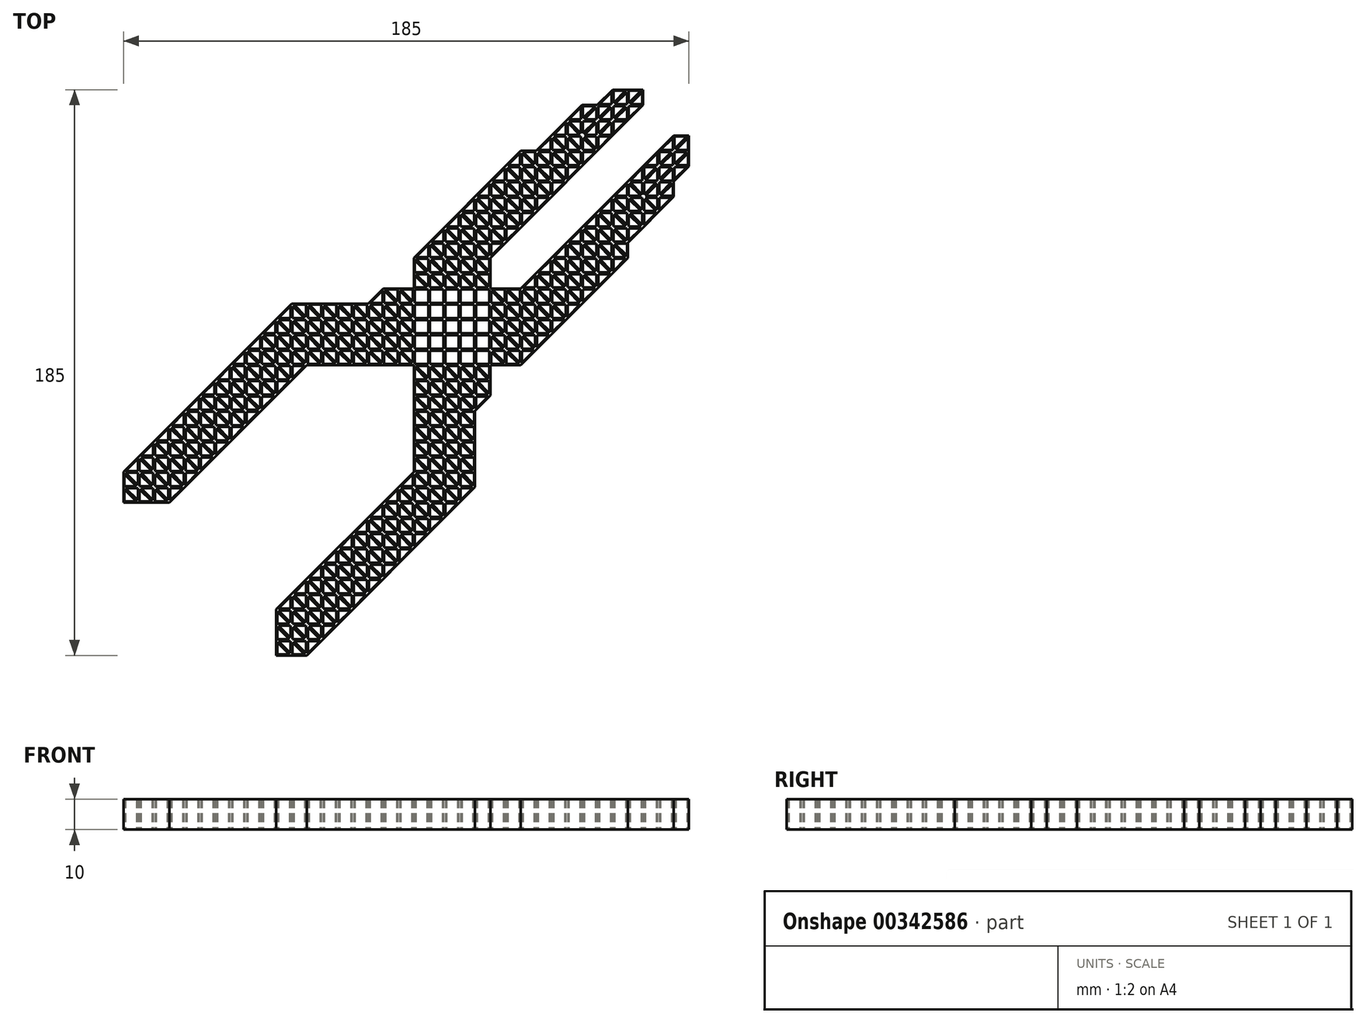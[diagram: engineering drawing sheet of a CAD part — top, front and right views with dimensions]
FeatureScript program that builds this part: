
annotation { "Feature Type Name" : "Feature", "Feature Type Description" : "" }
export const myFeature = defineFeature(function(context is Context, id is Id, definition is map)
    precondition{}
    {
        {
            var Q0;
            Q0=qCreatedBy(makeId("Top.planeOp"),FACE);
            var sketch = newSketch(context, id + "F0", { "sketchPlane" : qUnion([Q0])});
            skLineSegment(sketch, "E0", {"start": v(-41.78, -87.8) * mm, "end": v(-37.8, -87.8) * mm});
            skLineSegment(sketch, "E1", {"start": v(-37.8, -87.8) * mm, "end": v(-37.8, -91.78) * mm});
            skLineSegment(sketch, "E2", {"start": v(-37.8, -91.78) * mm, "end": v(-41.78, -87.8) * mm});
            skLineSegment(sketch, "E3", {"start": v(-86.78, -37.8) * mm, "end": v(-82.8, -37.8) * mm});
            skLineSegment(sketch, "E4", {"start": v(-82.8, -37.8) * mm, "end": v(-82.8, -41.78) * mm});
            skLineSegment(sketch, "E5", {"start": v(-82.8, -41.78) * mm, "end": v(-86.78, -37.8) * mm});
            skLineSegment(sketch, "E6", {"start": v(-91.78, -37.8) * mm, "end": v(-87.8, -37.8) * mm});
            skLineSegment(sketch, "E7", {"start": v(-87.8, -37.8) * mm, "end": v(-87.8, -41.78) * mm});
            skLineSegment(sketch, "E8", {"start": v(-87.8, -41.78) * mm, "end": v(-91.78, -37.8) * mm});
            skLineSegment(sketch, "E9", {"start": v(-33.22, 17.8) * mm, "end": v(-37.2, 17.8) * mm});
            skLineSegment(sketch, "E10", {"start": v(-37.2, 17.8) * mm, "end": v(-37.2, 21.78) * mm});
            skLineSegment(sketch, "E11", {"start": v(-37.2, 21.78) * mm, "end": v(-33.22, 17.8) * mm});
            skLineSegment(sketch, "E12", {"start": v(-18.22, 17.8) * mm, "end": v(-22.2, 17.8) * mm});
            skLineSegment(sketch, "E13", {"start": v(-22.2, 17.8) * mm, "end": v(-22.2, 21.78) * mm});
            skLineSegment(sketch, "E14", {"start": v(-22.2, 21.78) * mm, "end": v(-18.22, 17.8) * mm});
            skLineSegment(sketch, "E15", {"start": v(-3.22, 22.8) * mm, "end": v(-7.2, 22.8) * mm});
            skLineSegment(sketch, "E16", {"start": v(-7.2, 22.8) * mm, "end": v(-7.2, 26.78) * mm});
            skLineSegment(sketch, "E17", {"start": v(-7.2, 26.78) * mm, "end": v(-3.22, 22.8) * mm});
            skLineSegment(sketch, "E18", {"start": v(41.78, 67.8) * mm, "end": v(37.8, 67.8) * mm});
            skLineSegment(sketch, "E19", {"start": v(37.8, 67.8) * mm, "end": v(37.8, 71.78) * mm});
            skLineSegment(sketch, "E20", {"start": v(37.8, 71.78) * mm, "end": v(41.78, 67.8) * mm});
            skLineSegment(sketch, "E21", {"start": v(77.2, 87.8) * mm, "end": v(73.22, 87.8) * mm});
            skLineSegment(sketch, "E22", {"start": v(73.22, 87.8) * mm, "end": v(77.2, 91.78) * mm});
            skLineSegment(sketch, "E23", {"start": v(77.2, 91.78) * mm, "end": v(77.2, 87.8) * mm});
            skLineSegment(sketch, "E24", {"start": v(68.22, 82.8) * mm, "end": v(72.2, 86.78) * mm});
            skLineSegment(sketch, "E25", {"start": v(72.2, 86.78) * mm, "end": v(72.2, 82.8) * mm});
            skLineSegment(sketch, "E26", {"start": v(72.2, 82.8) * mm, "end": v(68.22, 82.8) * mm});
            skLineSegment(sketch, "E27", {"start": v(36.78, 22.8) * mm, "end": v(32.8, 22.8) * mm});
            skLineSegment(sketch, "E28", {"start": v(32.8, 22.8) * mm, "end": v(32.8, 26.78) * mm});
            skLineSegment(sketch, "E29", {"start": v(32.8, 26.78) * mm, "end": v(36.78, 22.8) * mm});
            skLineSegment(sketch, "E30", {"start": v(67.2, 33.22) * mm, "end": v(63.22, 37.2) * mm});
            skLineSegment(sketch, "E31", {"start": v(63.22, 37.2) * mm, "end": v(67.2, 37.2) * mm});
            skLineSegment(sketch, "E32", {"start": v(67.2, 37.2) * mm, "end": v(67.2, 33.22) * mm});
            skLineSegment(sketch, "E33", {"start": v(57.2, 23.22) * mm, "end": v(53.22, 27.2) * mm});
            skLineSegment(sketch, "E34", {"start": v(53.22, 27.2) * mm, "end": v(57.2, 27.2) * mm});
            skLineSegment(sketch, "E35", {"start": v(57.2, 27.2) * mm, "end": v(57.2, 23.22) * mm});
            skLineSegment(sketch, "E36", {"start": v(52.2, 18.22) * mm, "end": v(48.22, 22.2) * mm});
            skLineSegment(sketch, "E37", {"start": v(48.22, 22.2) * mm, "end": v(52.2, 22.2) * mm});
            skLineSegment(sketch, "E38", {"start": v(52.2, 22.2) * mm, "end": v(52.2, 18.22) * mm});
            skLineSegment(sketch, "E39", {"start": v(47.2, 13.22) * mm, "end": v(43.22, 17.2) * mm});
            skLineSegment(sketch, "E40", {"start": v(43.22, 17.2) * mm, "end": v(47.2, 17.2) * mm});
            skLineSegment(sketch, "E41", {"start": v(47.2, 17.2) * mm, "end": v(47.2, 13.22) * mm});
            skLineSegment(sketch, "E42", {"start": v(38.22, 12.2) * mm, "end": v(42.2, 12.2) * mm});
            skLineSegment(sketch, "E43", {"start": v(42.2, 12.2) * mm, "end": v(42.2, 8.22) * mm});
            skLineSegment(sketch, "E44", {"start": v(42.2, 8.22) * mm, "end": v(38.22, 12.2) * mm});
            skLineSegment(sketch, "E45", {"start": v(28.22, 7.2) * mm, "end": v(32.2, 7.2) * mm});
            skLineSegment(sketch, "E46", {"start": v(32.2, 7.2) * mm, "end": v(32.2, 5) * mm});
            skLineSegment(sketch, "E47", {"start": v(32.2, 5) * mm, "end": v(32.2, 3.22) * mm});
            skLineSegment(sketch, "E48", {"start": v(32.2, 3.22) * mm, "end": v(28.22, 7.2) * mm});
            skLineSegment(sketch, "E49", {"start": v(18.22, -32.8) * mm, "end": v(22.2, -32.8) * mm});
            skLineSegment(sketch, "E50", {"start": v(22.2, -32.8) * mm, "end": v(22.2, -36.78) * mm});
            skLineSegment(sketch, "E51", {"start": v(22.2, -36.78) * mm, "end": v(18.22, -32.8) * mm});
            skLineSegment(sketch, "E52", {"start": v(12.2, -46.78) * mm, "end": v(8.22, -42.8) * mm});
            skLineSegment(sketch, "E53", {"start": v(8.22, -42.8) * mm, "end": v(12.2, -42.8) * mm});
            skLineSegment(sketch, "E54", {"start": v(12.2, -42.8) * mm, "end": v(12.2, -46.78) * mm});
            skLineSegment(sketch, "E55", {"start": v(-7.8, -66.78) * mm, "end": v(-11.78, -62.8) * mm});
            skLineSegment(sketch, "E56", {"start": v(-11.78, -62.8) * mm, "end": v(-7.8, -62.8) * mm});
            skLineSegment(sketch, "E57", {"start": v(-7.8, -62.8) * mm, "end": v(-7.8, -66.78) * mm});
            skLineSegment(sketch, "E58", {"start": v(-21.78, -72.8) * mm, "end": v(-20, -72.8) * mm});
            skLineSegment(sketch, "E59", {"start": v(-20, -72.8) * mm, "end": v(-17.8, -72.8) * mm});
            skLineSegment(sketch, "E60", {"start": v(-17.8, -72.8) * mm, "end": v(-17.8, -76.78) * mm});
            skLineSegment(sketch, "E61", {"start": v(-17.8, -76.78) * mm, "end": v(-21.78, -72.8) * mm});
            skLineSegment(sketch, "E62", {"start": v(-27.8, -86.78) * mm, "end": v(-31.78, -82.8) * mm});
            skLineSegment(sketch, "E63", {"start": v(-31.78, -82.8) * mm, "end": v(-27.8, -82.8) * mm});
            skLineSegment(sketch, "E64", {"start": v(-27.8, -82.8) * mm, "end": v(-27.8, -86.78) * mm});
            skLineSegment(sketch, "E65", {"start": v(-32.8, 3.22) * mm, "end": v(-36.78, 7.2) * mm});
            skLineSegment(sketch, "E66", {"start": v(-36.78, 7.2) * mm, "end": v(-32.8, 7.2) * mm});
            skLineSegment(sketch, "E67", {"start": v(-32.8, 7.2) * mm, "end": v(-32.8, 3.22) * mm});
            skLineSegment(sketch, "E68", {"start": v(-47.8, -11.78) * mm, "end": v(-51.78, -7.8) * mm});
            skLineSegment(sketch, "E69", {"start": v(-51.78, -7.8) * mm, "end": v(-47.8, -7.8) * mm});
            skLineSegment(sketch, "E70", {"start": v(-47.8, -7.8) * mm, "end": v(-47.8, -11.78) * mm});
            skLineSegment(sketch, "E71", {"start": v(-92.2, -33.22) * mm, "end": v(-88.22, -37.2) * mm});
            skLineSegment(sketch, "E72", {"start": v(-88.22, -37.2) * mm, "end": v(-92.2, -37.2) * mm});
            skLineSegment(sketch, "E73", {"start": v(-92.2, -37.2) * mm, "end": v(-92.2, -33.22) * mm});
            skLineSegment(sketch, "E74", {"start": v(-83.22, -32.2) * mm, "end": v(-87.2, -32.2) * mm});
            skLineSegment(sketch, "E75", {"start": v(-87.2, -32.2) * mm, "end": v(-87.2, -28.22) * mm});
            skLineSegment(sketch, "E76", {"start": v(-87.2, -28.22) * mm, "end": v(-83.22, -32.2) * mm});
            skLineSegment(sketch, "E77", {"start": v(-77.2, -18.22) * mm, "end": v(-73.22, -22.2) * mm});
            skLineSegment(sketch, "E78", {"start": v(-73.22, -22.2) * mm, "end": v(-77.2, -22.2) * mm});
            skLineSegment(sketch, "E79", {"start": v(-77.2, -22.2) * mm, "end": v(-77.2, -18.22) * mm});
            skLineSegment(sketch, "E80", {"start": v(-63.22, -12.2) * mm, "end": v(-67.2, -12.2) * mm});
            skLineSegment(sketch, "E81", {"start": v(-67.2, -12.2) * mm, "end": v(-67.2, -8.22) * mm});
            skLineSegment(sketch, "E82", {"start": v(-67.2, -8.22) * mm, "end": v(-63.22, -12.2) * mm});
            skLineSegment(sketch, "E83", {"start": v(-43.22, 7.8) * mm, "end": v(-47.2, 7.8) * mm});
            skLineSegment(sketch, "E84", {"start": v(-47.2, 7.8) * mm, "end": v(-47.2, 11.78) * mm});
            skLineSegment(sketch, "E85", {"start": v(-47.2, 11.78) * mm, "end": v(-43.22, 7.8) * mm});
            skLineSegment(sketch, "E86", {"start": v(-38.22, 12.8) * mm, "end": v(-42.2, 12.8) * mm});
            skLineSegment(sketch, "E87", {"start": v(-42.2, 12.8) * mm, "end": v(-42.2, 16.78) * mm});
            skLineSegment(sketch, "E88", {"start": v(-42.2, 16.78) * mm, "end": v(-38.22, 12.8) * mm});
            skLineSegment(sketch, "E89", {"start": v(6.78, 32.8) * mm, "end": v(5, 32.8) * mm});
            skLineSegment(sketch, "E90", {"start": v(5, 32.8) * mm, "end": v(2.8, 32.8) * mm});
            skLineSegment(sketch, "E91", {"start": v(2.8, 32.8) * mm, "end": v(2.8, 36.78) * mm});
            skLineSegment(sketch, "E92", {"start": v(2.8, 36.78) * mm, "end": v(6.78, 32.8) * mm});
            skLineSegment(sketch, "E93", {"start": v(11.78, 37.8) * mm, "end": v(7.8, 37.8) * mm});
            skLineSegment(sketch, "E94", {"start": v(7.8, 37.8) * mm, "end": v(7.8, 41.78) * mm});
            skLineSegment(sketch, "E95", {"start": v(7.8, 41.78) * mm, "end": v(11.78, 37.8) * mm});
            skLineSegment(sketch, "E96", {"start": v(16.78, 42.8) * mm, "end": v(12.8, 42.8) * mm});
            skLineSegment(sketch, "E97", {"start": v(12.8, 42.8) * mm, "end": v(12.8, 46.78) * mm});
            skLineSegment(sketch, "E98", {"start": v(12.8, 46.78) * mm, "end": v(16.78, 42.8) * mm});
            skLineSegment(sketch, "E99", {"start": v(21.78, 47.8) * mm, "end": v(17.8, 47.8) * mm});
            skLineSegment(sketch, "E100", {"start": v(17.8, 47.8) * mm, "end": v(17.8, 51.78) * mm});
            skLineSegment(sketch, "E101", {"start": v(17.8, 51.78) * mm, "end": v(21.78, 47.8) * mm});
            skLineSegment(sketch, "E102", {"start": v(31.78, 57.8) * mm, "end": v(27.8, 57.8) * mm});
            skLineSegment(sketch, "E103", {"start": v(27.8, 57.8) * mm, "end": v(27.8, 61.78) * mm});
            skLineSegment(sketch, "E104", {"start": v(27.8, 61.78) * mm, "end": v(31.78, 57.8) * mm});
            skLineSegment(sketch, "E105", {"start": v(56.78, 77.8) * mm, "end": v(52.8, 77.8) * mm});
            skLineSegment(sketch, "E106", {"start": v(52.8, 77.8) * mm, "end": v(52.8, 81.78) * mm});
            skLineSegment(sketch, "E107", {"start": v(52.8, 81.78) * mm, "end": v(56.78, 77.8) * mm});
            skLineSegment(sketch, "E108", {"start": v(62.2, 73.22) * mm, "end": v(58.22, 77.2) * mm});
            skLineSegment(sketch, "E109", {"start": v(58.22, 77.2) * mm, "end": v(62.2, 77.2) * mm});
            skLineSegment(sketch, "E110", {"start": v(62.2, 77.2) * mm, "end": v(62.2, 73.22) * mm});
            skLineSegment(sketch, "E111", {"start": v(52.2, 63.22) * mm, "end": v(48.22, 67.2) * mm});
            skLineSegment(sketch, "E112", {"start": v(48.22, 67.2) * mm, "end": v(52.2, 67.2) * mm});
            skLineSegment(sketch, "E113", {"start": v(52.2, 67.2) * mm, "end": v(52.2, 63.22) * mm});
            skLineSegment(sketch, "E114", {"start": v(43.22, 62.2) * mm, "end": v(47.2, 62.2) * mm});
            skLineSegment(sketch, "E115", {"start": v(47.2, 62.2) * mm, "end": v(47.2, 58.22) * mm});
            skLineSegment(sketch, "E116", {"start": v(47.2, 58.22) * mm, "end": v(43.22, 62.2) * mm});
            skLineSegment(sketch, "E117", {"start": v(42.2, 53.22) * mm, "end": v(38.22, 57.2) * mm});
            skLineSegment(sketch, "E118", {"start": v(38.22, 57.2) * mm, "end": v(42.2, 57.2) * mm});
            skLineSegment(sketch, "E119", {"start": v(42.2, 57.2) * mm, "end": v(42.2, 53.22) * mm});
            skLineSegment(sketch, "E120", {"start": v(32.2, 43.22) * mm, "end": v(28.22, 47.2) * mm});
            skLineSegment(sketch, "E121", {"start": v(28.22, 47.2) * mm, "end": v(32.2, 47.2) * mm});
            skLineSegment(sketch, "E122", {"start": v(32.2, 47.2) * mm, "end": v(32.2, 43.22) * mm});
            skLineSegment(sketch, "E123", {"start": v(46.78, 27.8) * mm, "end": v(42.8, 27.8) * mm});
            skLineSegment(sketch, "E124", {"start": v(42.8, 27.8) * mm, "end": v(42.8, 31.78) * mm});
            skLineSegment(sketch, "E125", {"start": v(42.8, 31.78) * mm, "end": v(46.78, 27.8) * mm});
            skLineSegment(sketch, "E126", {"start": v(56.78, 37.8) * mm, "end": v(52.8, 37.8) * mm});
            skLineSegment(sketch, "E127", {"start": v(52.8, 37.8) * mm, "end": v(52.8, 41.78) * mm});
            skLineSegment(sketch, "E128", {"start": v(52.8, 41.78) * mm, "end": v(56.78, 37.8) * mm});
            skLineSegment(sketch, "E129", {"start": v(61.78, 42.8) * mm, "end": v(57.8, 42.8) * mm});
            skLineSegment(sketch, "E130", {"start": v(57.8, 42.8) * mm, "end": v(57.8, 46.78) * mm});
            skLineSegment(sketch, "E131", {"start": v(57.8, 46.78) * mm, "end": v(61.78, 42.8) * mm});
            skLineSegment(sketch, "E132", {"start": v(62.8, 51.78) * mm, "end": v(66.78, 47.8) * mm});
            skLineSegment(sketch, "E133", {"start": v(66.78, 47.8) * mm, "end": v(62.8, 47.8) * mm});
            skLineSegment(sketch, "E134", {"start": v(62.8, 47.8) * mm, "end": v(62.8, 51.78) * mm});
            skLineSegment(sketch, "E135", {"start": v(76.78, 57.8) * mm, "end": v(72.8, 57.8) * mm});
            skLineSegment(sketch, "E136", {"start": v(72.8, 57.8) * mm, "end": v(72.8, 61.78) * mm});
            skLineSegment(sketch, "E137", {"start": v(72.8, 61.78) * mm, "end": v(76.78, 57.8) * mm});
            skLineSegment(sketch, "E138", {"start": v(5, -22.8) * mm, "end": v(7.2, -22.8) * mm});
            skLineSegment(sketch, "E139", {"start": v(7.2, -22.8) * mm, "end": v(7.2, -26.78) * mm});
            skLineSegment(sketch, "E140", {"start": v(7.2, -26.78) * mm, "end": v(3.22, -22.8) * mm});
            skLineSegment(sketch, "E141", {"start": v(3.22, -22.8) * mm, "end": v(5, -22.8) * mm});
            skLineSegment(sketch, "E142", {"start": v(5, -7.8) * mm, "end": v(7.2, -7.8) * mm});
            skLineSegment(sketch, "E143", {"start": v(7.2, -7.8) * mm, "end": v(7.2, -11.78) * mm});
            skLineSegment(sketch, "E144", {"start": v(7.2, -11.78) * mm, "end": v(3.22, -7.8) * mm});
            skLineSegment(sketch, "E145", {"start": v(3.22, -7.8) * mm, "end": v(5, -7.8) * mm});
            skLineSegment(sketch, "E146", {"start": v(-2.8, 8.22) * mm, "end": v(-6.78, 12.2) * mm});
            skLineSegment(sketch, "E147", {"start": v(-6.78, 12.2) * mm, "end": v(-2.8, 12.2) * mm});
            skLineSegment(sketch, "E148", {"start": v(-2.8, 12.2) * mm, "end": v(-2.8, 8.22) * mm});
            skLineSegment(sketch, "E149", {"start": v(-17.8, 8.22) * mm, "end": v(-21.78, 12.2) * mm});
            skLineSegment(sketch, "E150", {"start": v(-21.78, 12.2) * mm, "end": v(-17.8, 12.2) * mm});
            skLineSegment(sketch, "E151", {"start": v(-17.8, 12.2) * mm, "end": v(-17.8, 8.22) * mm});
            skLineSegment(sketch, "E152", {"start": v(-77.8, -36.78) * mm, "end": v(-81.78, -32.8) * mm});
            skLineSegment(sketch, "E153", {"start": v(-81.78, -32.8) * mm, "end": v(-77.8, -32.8) * mm});
            skLineSegment(sketch, "E154", {"start": v(-77.8, -32.8) * mm, "end": v(-77.8, -36.78) * mm});
            skLineSegment(sketch, "E155", {"start": v(-86.78, -32.8) * mm, "end": v(-82.8, -32.8) * mm});
            skLineSegment(sketch, "E156", {"start": v(-82.8, -32.8) * mm, "end": v(-82.8, -36.78) * mm});
            skLineSegment(sketch, "E157", {"start": v(-82.8, -36.78) * mm, "end": v(-86.78, -32.8) * mm});
            skLineSegment(sketch, "E158", {"start": v(-82.2, -28.22) * mm, "end": v(-78.22, -32.2) * mm});
            skLineSegment(sketch, "E159", {"start": v(-78.22, -32.2) * mm, "end": v(-82.2, -32.2) * mm});
            skLineSegment(sketch, "E160", {"start": v(-82.2, -32.2) * mm, "end": v(-82.2, -28.22) * mm});
            skLineSegment(sketch, "E161", {"start": v(-62.8, -16.78) * mm, "end": v(-66.78, -12.8) * mm});
            skLineSegment(sketch, "E162", {"start": v(-66.78, -12.8) * mm, "end": v(-62.8, -12.8) * mm});
            skLineSegment(sketch, "E163", {"start": v(-62.8, -12.8) * mm, "end": v(-62.8, -16.78) * mm});
            skLineSegment(sketch, "E164", {"start": v(-63.22, -17.2) * mm, "end": v(-65, -17.2) * mm});
            skLineSegment(sketch, "E165", {"start": v(-65, -17.2) * mm, "end": v(-67.2, -17.2) * mm});
            skLineSegment(sketch, "E166", {"start": v(-67.2, -17.2) * mm, "end": v(-67.2, -13.22) * mm});
            skLineSegment(sketch, "E167", {"start": v(-67.2, -13.22) * mm, "end": v(-63.22, -17.2) * mm});
            skLineSegment(sketch, "E168", {"start": v(-77.8, -31.78) * mm, "end": v(-81.78, -27.8) * mm});
            skLineSegment(sketch, "E169", {"start": v(-81.78, -27.8) * mm, "end": v(-77.8, -27.8) * mm});
            skLineSegment(sketch, "E170", {"start": v(-77.8, -27.8) * mm, "end": v(-77.8, -31.78) * mm});
            skLineSegment(sketch, "E171", {"start": v(-77.2, -32.2) * mm, "end": v(-77.2, -28.22) * mm});
            skLineSegment(sketch, "E172", {"start": v(-77.2, -28.22) * mm, "end": v(-73.23, -32.2) * mm});
            skLineSegment(sketch, "E173", {"start": v(-73.23, -32.2) * mm, "end": v(-77.2, -32.2) * mm});
            skLineSegment(sketch, "E174", {"start": v(-77.2, -23.22) * mm, "end": v(-73.22, -27.2) * mm});
            skLineSegment(sketch, "E175", {"start": v(-73.22, -27.2) * mm, "end": v(-77.2, -27.2) * mm});
            skLineSegment(sketch, "E176", {"start": v(-77.2, -27.2) * mm, "end": v(-77.2, -23.22) * mm});
            skLineSegment(sketch, "E177", {"start": v(-76.78, -22.8) * mm, "end": v(-72.8, -22.8) * mm});
            skLineSegment(sketch, "E178", {"start": v(-72.8, -22.8) * mm, "end": v(-72.8, -26.78) * mm});
            skLineSegment(sketch, "E179", {"start": v(-72.8, -26.78) * mm, "end": v(-76.78, -22.8) * mm});
            skLineSegment(sketch, "E180", {"start": v(-67.2, -22.2) * mm, "end": v(-67.2, -18.22) * mm});
            skLineSegment(sketch, "E181", {"start": v(-67.2, -18.22) * mm, "end": v(-63.22, -22.2) * mm});
            skLineSegment(sketch, "E182", {"start": v(-63.22, -22.2) * mm, "end": v(-67.2, -22.2) * mm});
            skLineSegment(sketch, "E183", {"start": v(-67.8, -16.78) * mm, "end": v(-71.78, -12.8) * mm});
            skLineSegment(sketch, "E184", {"start": v(-71.78, -12.8) * mm, "end": v(-67.8, -12.8) * mm});
            skLineSegment(sketch, "E185", {"start": v(-67.8, -12.8) * mm, "end": v(-67.8, -16.78) * mm});
            skLineSegment(sketch, "E186", {"start": v(-67.8, -17.8) * mm, "end": v(-67.8, -21.78) * mm});
            skLineSegment(sketch, "E187", {"start": v(-67.8, -21.78) * mm, "end": v(-71.78, -17.8) * mm});
            skLineSegment(sketch, "E188", {"start": v(-71.78, -17.8) * mm, "end": v(-67.8, -17.8) * mm});
            skLineSegment(sketch, "E189", {"start": v(-77.8, -26.78) * mm, "end": v(-81.78, -22.8) * mm});
            skLineSegment(sketch, "E190", {"start": v(-81.78, -22.8) * mm, "end": v(-77.8, -22.8) * mm});
            skLineSegment(sketch, "E191", {"start": v(-77.8, -22.8) * mm, "end": v(-77.8, -26.78) * mm});
            skLineSegment(sketch, "E192", {"start": v(-78.22, -27.2) * mm, "end": v(-82.2, -27.2) * mm});
            skLineSegment(sketch, "E193", {"start": v(-82.2, -27.2) * mm, "end": v(-82.2, -23.22) * mm});
            skLineSegment(sketch, "E194", {"start": v(-82.2, -23.22) * mm, "end": v(-78.22, -27.2) * mm});
            skLineSegment(sketch, "E195", {"start": v(-87.8, -36.78) * mm, "end": v(-91.78, -32.8) * mm});
            skLineSegment(sketch, "E196", {"start": v(-91.78, -32.8) * mm, "end": v(-87.8, -32.8) * mm});
            skLineSegment(sketch, "E197", {"start": v(-87.8, -32.8) * mm, "end": v(-87.8, -36.78) * mm});
            skLineSegment(sketch, "E198", {"start": v(-72.8, -31.78) * mm, "end": v(-76.78, -27.8) * mm});
            skLineSegment(sketch, "E199", {"start": v(-76.78, -27.8) * mm, "end": v(-72.8, -27.8) * mm});
            skLineSegment(sketch, "E200", {"start": v(-72.8, -27.8) * mm, "end": v(-72.8, -31.78) * mm});
            skLineSegment(sketch, "E201", {"start": v(-72.2, -23.22) * mm, "end": v(-68.22, -27.2) * mm});
            skLineSegment(sketch, "E202", {"start": v(-68.22, -27.2) * mm, "end": v(-72.2, -27.2) * mm});
            skLineSegment(sketch, "E203", {"start": v(-72.2, -27.2) * mm, "end": v(-72.2, -23.22) * mm});
            skLineSegment(sketch, "E204", {"start": v(-71.78, -22.8) * mm, "end": v(-67.8, -22.8) * mm});
            skLineSegment(sketch, "E205", {"start": v(-67.8, -22.8) * mm, "end": v(-67.8, -26.78) * mm});
            skLineSegment(sketch, "E206", {"start": v(-67.8, -26.78) * mm, "end": v(-71.78, -22.8) * mm});
            skLineSegment(sketch, "E207", {"start": v(-62.8, -22.8) * mm, "end": v(-62.8, -26.78) * mm});
            skLineSegment(sketch, "E208", {"start": v(-62.8, -26.78) * mm, "end": v(-66.78, -22.8) * mm});
            skLineSegment(sketch, "E209", {"start": v(-66.78, -22.8) * mm, "end": v(-62.8, -22.8) * mm});
            skLineSegment(sketch, "E210", {"start": v(-62.8, -21.78) * mm, "end": v(-66.78, -17.8) * mm});
            skLineSegment(sketch, "E211", {"start": v(-66.78, -17.8) * mm, "end": v(-65, -17.8) * mm});
            skLineSegment(sketch, "E212", {"start": v(-65, -17.8) * mm, "end": v(-62.8, -17.8) * mm});
            skLineSegment(sketch, "E213", {"start": v(-62.8, -17.8) * mm, "end": v(-62.8, -21.78) * mm});
            skLineSegment(sketch, "E214", {"start": v(-62.2, -13.22) * mm, "end": v(-58.22, -17.2) * mm});
            skLineSegment(sketch, "E215", {"start": v(-58.22, -17.2) * mm, "end": v(-62.2, -17.2) * mm});
            skLineSegment(sketch, "E216", {"start": v(-62.2, -17.2) * mm, "end": v(-62.2, -13.22) * mm});
            skLineSegment(sketch, "E217", {"start": v(-62.2, -8.22) * mm, "end": v(-58.22, -12.2) * mm});
            skLineSegment(sketch, "E218", {"start": v(-58.22, -12.2) * mm, "end": v(-62.2, -12.2) * mm});
            skLineSegment(sketch, "E219", {"start": v(-62.2, -12.2) * mm, "end": v(-62.2, -8.22) * mm});
            skLineSegment(sketch, "E220", {"start": v(-33.22, 12.8) * mm, "end": v(-37.2, 12.8) * mm});
            skLineSegment(sketch, "E221", {"start": v(-37.2, 12.8) * mm, "end": v(-37.2, 16.78) * mm});
            skLineSegment(sketch, "E222", {"start": v(-37.2, 16.78) * mm, "end": v(-33.22, 12.8) * mm});
            skLineSegment(sketch, "E223", {"start": v(-3.22, 17.8) * mm, "end": v(-7.2, 17.8) * mm});
            skLineSegment(sketch, "E224", {"start": v(-7.2, 17.8) * mm, "end": v(-7.2, 21.78) * mm});
            skLineSegment(sketch, "E225", {"start": v(-7.2, 21.78) * mm, "end": v(-3.22, 17.8) * mm});
            skLineSegment(sketch, "E226", {"start": v(58.22, 77.8) * mm, "end": v(62.2, 81.78) * mm});
            skLineSegment(sketch, "E227", {"start": v(62.2, 81.78) * mm, "end": v(62.2, 77.8) * mm});
            skLineSegment(sketch, "E228", {"start": v(62.2, 77.8) * mm, "end": v(58.22, 77.8) * mm});
            skLineSegment(sketch, "E229", {"start": v(47.8, 71.78) * mm, "end": v(51.78, 67.8) * mm});
            skLineSegment(sketch, "E230", {"start": v(51.78, 67.8) * mm, "end": v(47.8, 67.8) * mm});
            skLineSegment(sketch, "E231", {"start": v(47.8, 67.8) * mm, "end": v(47.8, 71.78) * mm});
            skLineSegment(sketch, "E232", {"start": v(52.8, 76.78) * mm, "end": v(56.78, 72.8) * mm});
            skLineSegment(sketch, "E233", {"start": v(56.78, 72.8) * mm, "end": v(52.8, 72.8) * mm});
            skLineSegment(sketch, "E234", {"start": v(52.8, 72.8) * mm, "end": v(52.8, 76.78) * mm});
            skLineSegment(sketch, "E235", {"start": v(53.22, 77.2) * mm, "end": v(57.2, 77.2) * mm});
            skLineSegment(sketch, "E236", {"start": v(57.2, 77.2) * mm, "end": v(57.2, 73.22) * mm});
            skLineSegment(sketch, "E237", {"start": v(57.2, 73.22) * mm, "end": v(53.22, 77.2) * mm});
            skLineSegment(sketch, "E238", {"start": v(61.78, 82.2) * mm, "end": v(57.8, 78.22) * mm});
            skLineSegment(sketch, "E239", {"start": v(57.8, 78.22) * mm, "end": v(57.8, 82.2) * mm});
            skLineSegment(sketch, "E240", {"start": v(57.8, 82.2) * mm, "end": v(61.78, 82.2) * mm});
            skLineSegment(sketch, "E241", {"start": v(52.2, 73.22) * mm, "end": v(48.22, 77.2) * mm});
            skLineSegment(sketch, "E242", {"start": v(48.22, 77.2) * mm, "end": v(52.2, 77.2) * mm});
            skLineSegment(sketch, "E243", {"start": v(52.2, 77.2) * mm, "end": v(52.2, 73.22) * mm});
            skLineSegment(sketch, "E244", {"start": v(47.2, 68.22) * mm, "end": v(43.22, 72.2) * mm});
            skLineSegment(sketch, "E245", {"start": v(43.22, 72.2) * mm, "end": v(47.2, 72.2) * mm});
            skLineSegment(sketch, "E246", {"start": v(47.2, 72.2) * mm, "end": v(47.2, 68.22) * mm});
            skLineSegment(sketch, "E247", {"start": v(47.2, 63.22) * mm, "end": v(43.22, 67.2) * mm});
            skLineSegment(sketch, "E248", {"start": v(43.22, 67.2) * mm, "end": v(47.2, 67.2) * mm});
            skLineSegment(sketch, "E249", {"start": v(47.2, 67.2) * mm, "end": v(47.2, 63.22) * mm});
            skLineSegment(sketch, "E250", {"start": v(27.8, 51.78) * mm, "end": v(31.78, 47.8) * mm});
            skLineSegment(sketch, "E251", {"start": v(31.78, 47.8) * mm, "end": v(27.8, 47.8) * mm});
            skLineSegment(sketch, "E252", {"start": v(27.8, 47.8) * mm, "end": v(27.8, 51.78) * mm});
            skLineSegment(sketch, "E253", {"start": v(32.8, 56.78) * mm, "end": v(36.78, 52.8) * mm});
            skLineSegment(sketch, "E254", {"start": v(36.78, 52.8) * mm, "end": v(32.8, 52.8) * mm});
            skLineSegment(sketch, "E255", {"start": v(32.8, 52.8) * mm, "end": v(32.8, 56.78) * mm});
            skLineSegment(sketch, "E256", {"start": v(33.22, 57.2) * mm, "end": v(37.2, 57.2) * mm});
            skLineSegment(sketch, "E257", {"start": v(37.2, 57.2) * mm, "end": v(37.2, 53.22) * mm});
            skLineSegment(sketch, "E258", {"start": v(37.2, 53.22) * mm, "end": v(33.22, 57.2) * mm});
            skLineSegment(sketch, "E259", {"start": v(37.8, 61.78) * mm, "end": v(41.78, 57.8) * mm});
            skLineSegment(sketch, "E260", {"start": v(41.78, 57.8) * mm, "end": v(37.8, 57.8) * mm});
            skLineSegment(sketch, "E261", {"start": v(37.8, 57.8) * mm, "end": v(37.8, 61.78) * mm});
            skLineSegment(sketch, "E262", {"start": v(46.78, 62.8) * mm, "end": v(42.8, 62.8) * mm});
            skLineSegment(sketch, "E263", {"start": v(42.8, 62.8) * mm, "end": v(42.8, 66.78) * mm});
            skLineSegment(sketch, "E264", {"start": v(42.8, 66.78) * mm, "end": v(46.78, 62.8) * mm});
            skLineSegment(sketch, "E265", {"start": v(37.2, 62.2) * mm, "end": v(37.2, 58.22) * mm});
            skLineSegment(sketch, "E266", {"start": v(37.2, 58.22) * mm, "end": v(33.22, 62.2) * mm});
            skLineSegment(sketch, "E267", {"start": v(33.22, 62.2) * mm, "end": v(37.2, 62.2) * mm});
            skLineSegment(sketch, "E268", {"start": v(32.2, 53.22) * mm, "end": v(28.22, 57.2) * mm});
            skLineSegment(sketch, "E269", {"start": v(28.22, 57.2) * mm, "end": v(32.2, 57.2) * mm});
            skLineSegment(sketch, "E270", {"start": v(32.2, 57.2) * mm, "end": v(32.2, 53.22) * mm});
            skLineSegment(sketch, "E271", {"start": v(27.2, 52.2) * mm, "end": v(27.2, 48.22) * mm});
            skLineSegment(sketch, "E272", {"start": v(27.2, 48.22) * mm, "end": v(23.22, 52.2) * mm});
            skLineSegment(sketch, "E273", {"start": v(23.22, 52.2) * mm, "end": v(27.2, 52.2) * mm});
            skLineSegment(sketch, "E274", {"start": v(27.2, 43.22) * mm, "end": v(23.22, 47.2) * mm});
            skLineSegment(sketch, "E275", {"start": v(23.22, 47.2) * mm, "end": v(27.2, 47.2) * mm});
            skLineSegment(sketch, "E276", {"start": v(27.2, 47.2) * mm, "end": v(27.2, 43.22) * mm});
            skLineSegment(sketch, "E277", {"start": v(27.2, 38.22) * mm, "end": v(23.22, 42.2) * mm});
            skLineSegment(sketch, "E278", {"start": v(23.22, 42.2) * mm, "end": v(27.2, 42.2) * mm});
            skLineSegment(sketch, "E279", {"start": v(27.2, 42.2) * mm, "end": v(27.2, 38.22) * mm});
            skLineSegment(sketch, "E280", {"start": v(36.78, 17.8) * mm, "end": v(32.8, 17.8) * mm});
            skLineSegment(sketch, "E281", {"start": v(32.8, 17.8) * mm, "end": v(32.8, 21.78) * mm});
            skLineSegment(sketch, "E282", {"start": v(32.8, 21.78) * mm, "end": v(36.78, 17.8) * mm});
            skLineSegment(sketch, "E283", {"start": v(42.2, 23.22) * mm, "end": v(38.22, 27.2) * mm});
            skLineSegment(sketch, "E284", {"start": v(38.22, 27.2) * mm, "end": v(42.2, 27.2) * mm});
            skLineSegment(sketch, "E285", {"start": v(42.2, 27.2) * mm, "end": v(42.2, 23.22) * mm});
            skLineSegment(sketch, "E286", {"start": v(33.22, 17.2) * mm, "end": v(37.2, 17.2) * mm});
            skLineSegment(sketch, "E287", {"start": v(37.2, 17.2) * mm, "end": v(37.2, 13.22) * mm});
            skLineSegment(sketch, "E288", {"start": v(37.2, 13.22) * mm, "end": v(33.22, 17.2) * mm});
            skLineSegment(sketch, "E289", {"start": v(-2.2, -47.2) * mm, "end": v(-2.2, -43.22) * mm});
            skLineSegment(sketch, "E290", {"start": v(-2.2, -43.22) * mm, "end": v(1.78, -47.2) * mm});
            skLineSegment(sketch, "E291", {"start": v(1.78, -47.2) * mm, "end": v(-2.2, -47.2) * mm});
            skLineSegment(sketch, "E292", {"start": v(-2.8, -51.78) * mm, "end": v(-6.78, -47.8) * mm});
            skLineSegment(sketch, "E293", {"start": v(-6.78, -47.8) * mm, "end": v(-2.8, -47.8) * mm});
            skLineSegment(sketch, "E294", {"start": v(-2.8, -47.8) * mm, "end": v(-2.8, -51.78) * mm});
            skLineSegment(sketch, "E295", {"start": v(2.2, -47.8) * mm, "end": v(2.2, -51.78) * mm});
            skLineSegment(sketch, "E296", {"start": v(2.2, -51.78) * mm, "end": v(-1.78, -47.8) * mm});
            skLineSegment(sketch, "E297", {"start": v(-1.78, -47.8) * mm, "end": v(2.2, -47.8) * mm});
            skLineSegment(sketch, "E298", {"start": v(2.8, -47.2) * mm, "end": v(2.8, -43.22) * mm});
            skLineSegment(sketch, "E299", {"start": v(2.8, -43.22) * mm, "end": v(6.78, -47.2) * mm});
            skLineSegment(sketch, "E300", {"start": v(6.78, -47.2) * mm, "end": v(5, -47.2) * mm});
            skLineSegment(sketch, "E301", {"start": v(5, -47.2) * mm, "end": v(2.8, -47.2) * mm});
            skLineSegment(sketch, "E302", {"start": v(3.22, -42.8) * mm, "end": v(7.2, -42.8) * mm});
            skLineSegment(sketch, "E303", {"start": v(7.2, -42.8) * mm, "end": v(7.2, -46.78) * mm});
            skLineSegment(sketch, "E304", {"start": v(7.2, -46.78) * mm, "end": v(3.22, -42.8) * mm});
            skLineSegment(sketch, "E305", {"start": v(7.2, -36.78) * mm, "end": v(3.22, -32.8) * mm});
            skLineSegment(sketch, "E306", {"start": v(3.22, -32.8) * mm, "end": v(7.2, -32.8) * mm});
            skLineSegment(sketch, "E307", {"start": v(7.2, -32.8) * mm, "end": v(7.2, -36.78) * mm});
            skLineSegment(sketch, "E308", {"start": v(7.2, -37.8) * mm, "end": v(7.2, -41.78) * mm});
            skLineSegment(sketch, "E309", {"start": v(7.2, -41.78) * mm, "end": v(3.22, -37.8) * mm});
            skLineSegment(sketch, "E310", {"start": v(3.22, -37.8) * mm, "end": v(7.2, -37.8) * mm});
            skLineSegment(sketch, "E311", {"start": v(7.8, -38.22) * mm, "end": v(11.78, -42.2) * mm});
            skLineSegment(sketch, "E312", {"start": v(11.78, -42.2) * mm, "end": v(7.8, -42.2) * mm});
            skLineSegment(sketch, "E313", {"start": v(7.8, -42.2) * mm, "end": v(7.8, -38.22) * mm});
            skLineSegment(sketch, "E314", {"start": v(-27.2, 16.78) * mm, "end": v(-23.22, 12.8) * mm});
            skLineSegment(sketch, "E315", {"start": v(-23.22, 12.8) * mm, "end": v(-27.2, 12.8) * mm});
            skLineSegment(sketch, "E316", {"start": v(-27.2, 12.8) * mm, "end": v(-27.2, 16.78) * mm});
            skLineSegment(sketch, "E317", {"start": v(-26.78, 17.2) * mm, "end": v(-22.8, 17.2) * mm});
            skLineSegment(sketch, "E318", {"start": v(-22.8, 17.2) * mm, "end": v(-22.8, 13.22) * mm});
            skLineSegment(sketch, "E319", {"start": v(-22.8, 13.22) * mm, "end": v(-26.78, 17.2) * mm});
            skLineSegment(sketch, "E320", {"start": v(-27.8, 13.22) * mm, "end": v(-31.78, 17.2) * mm});
            skLineSegment(sketch, "E321", {"start": v(-31.78, 17.2) * mm, "end": v(-27.8, 17.2) * mm});
            skLineSegment(sketch, "E322", {"start": v(-27.8, 17.2) * mm, "end": v(-27.8, 13.22) * mm});
            skLineSegment(sketch, "E323", {"start": v(-22.2, 16.78) * mm, "end": v(-18.22, 12.8) * mm});
            skLineSegment(sketch, "E324", {"start": v(-18.22, 12.8) * mm, "end": v(-22.2, 12.8) * mm});
            skLineSegment(sketch, "E325", {"start": v(-22.2, 12.8) * mm, "end": v(-22.2, 16.78) * mm});
            skLineSegment(sketch, "E326", {"start": v(-21.78, 17.2) * mm, "end": v(-17.8, 17.2) * mm});
            skLineSegment(sketch, "E327", {"start": v(-17.8, 17.2) * mm, "end": v(-17.8, 13.22) * mm});
            skLineSegment(sketch, "E328", {"start": v(-17.8, 13.22) * mm, "end": v(-21.78, 17.2) * mm});
            skLineSegment(sketch, "E329", {"start": v(-17.2, 16.78) * mm, "end": v(-13.22, 12.8) * mm});
            skLineSegment(sketch, "E330", {"start": v(-13.22, 12.8) * mm, "end": v(-17.2, 12.8) * mm});
            skLineSegment(sketch, "E331", {"start": v(-17.2, 12.8) * mm, "end": v(-17.2, 16.78) * mm});
            skLineSegment(sketch, "E332", {"start": v(12.8, 36.78) * mm, "end": v(16.78, 32.8) * mm});
            skLineSegment(sketch, "E333", {"start": v(16.78, 32.8) * mm, "end": v(12.8, 32.8) * mm});
            skLineSegment(sketch, "E334", {"start": v(12.8, 32.8) * mm, "end": v(12.8, 36.78) * mm});
            skLineSegment(sketch, "E335", {"start": v(-6.78, 17.2) * mm, "end": v(-2.8, 17.2) * mm});
            skLineSegment(sketch, "E336", {"start": v(-2.8, 17.2) * mm, "end": v(-2.8, 13.22) * mm});
            skLineSegment(sketch, "E337", {"start": v(-2.8, 13.22) * mm, "end": v(-6.78, 17.2) * mm});
            skLineSegment(sketch, "E338", {"start": v(-11.78, 17.2) * mm, "end": v(-7.8, 17.2) * mm});
            skLineSegment(sketch, "E339", {"start": v(-7.8, 17.2) * mm, "end": v(-7.8, 13.22) * mm});
            skLineSegment(sketch, "E340", {"start": v(-7.8, 13.22) * mm, "end": v(-11.78, 17.2) * mm});
            skLineSegment(sketch, "E341", {"start": v(2.2, 17.2) * mm, "end": v(2.2, 13.22) * mm});
            skLineSegment(sketch, "E342", {"start": v(2.2, 13.22) * mm, "end": v(-1.78, 17.2) * mm});
            skLineSegment(sketch, "E343", {"start": v(-1.78, 17.2) * mm, "end": v(2.2, 17.2) * mm});
            skLineSegment(sketch, "E344", {"start": v(2.8, 17.2) * mm, "end": v(7.2, 17.2) * mm});
            skLineSegment(sketch, "E345", {"start": v(7.2, 17.2) * mm, "end": v(7.2, 12.8) * mm});
            skLineSegment(sketch, "E346", {"start": v(7.2, 12.8) * mm, "end": v(2.8, 12.8) * mm});
            skLineSegment(sketch, "E347", {"start": v(2.8, 12.8) * mm, "end": v(2.8, 17.2) * mm});
            skLineSegment(sketch, "E348", {"start": v(22.2, 7.8) * mm, "end": v(17.8, 7.8) * mm});
            skLineSegment(sketch, "E349", {"start": v(17.8, 7.8) * mm, "end": v(17.8, 12.2) * mm});
            skLineSegment(sketch, "E350", {"start": v(17.8, 12.2) * mm, "end": v(22.2, 12.2) * mm});
            skLineSegment(sketch, "E351", {"start": v(22.2, 12.2) * mm, "end": v(22.2, 7.8) * mm});
            skLineSegment(sketch, "E352", {"start": v(12.8, -13.22) * mm, "end": v(16.78, -17.2) * mm});
            skLineSegment(sketch, "E353", {"start": v(16.78, -17.2) * mm, "end": v(12.8, -17.2) * mm});
            skLineSegment(sketch, "E354", {"start": v(12.8, -17.2) * mm, "end": v(12.8, -13.22) * mm});
            skLineSegment(sketch, "E355", {"start": v(12.8, -18.22) * mm, "end": v(16.78, -22.2) * mm});
            skLineSegment(sketch, "E356", {"start": v(16.78, -22.2) * mm, "end": v(12.8, -22.2) * mm});
            skLineSegment(sketch, "E357", {"start": v(12.8, -22.2) * mm, "end": v(12.8, -18.22) * mm});
            skLineSegment(sketch, "E358", {"start": v(12.8, -23.22) * mm, "end": v(16.78, -27.2) * mm});
            skLineSegment(sketch, "E359", {"start": v(16.78, -27.2) * mm, "end": v(12.8, -27.2) * mm});
            skLineSegment(sketch, "E360", {"start": v(12.8, -27.2) * mm, "end": v(12.8, -25.27) * mm});
            skLineSegment(sketch, "E361", {"start": v(12.8, -25.27) * mm, "end": v(12.8, -23.22) * mm});
            skLineSegment(sketch, "E362", {"start": v(17.2, -27.8) * mm, "end": v(17.2, -31.78) * mm});
            skLineSegment(sketch, "E363", {"start": v(17.2, -31.78) * mm, "end": v(13.22, -27.8) * mm});
            skLineSegment(sketch, "E364", {"start": v(13.22, -27.8) * mm, "end": v(17.2, -27.8) * mm});
            skLineSegment(sketch, "E365", {"start": v(13.22, -22.8) * mm, "end": v(17.2, -22.8) * mm});
            skLineSegment(sketch, "E366", {"start": v(17.2, -22.8) * mm, "end": v(17.2, -26.78) * mm});
            skLineSegment(sketch, "E367", {"start": v(17.2, -26.78) * mm, "end": v(13.22, -22.8) * mm});
            skLineSegment(sketch, "E368", {"start": v(13.22, -17.8) * mm, "end": v(17.2, -17.8) * mm});
            skLineSegment(sketch, "E369", {"start": v(17.2, -17.8) * mm, "end": v(17.2, -21.78) * mm});
            skLineSegment(sketch, "E370", {"start": v(17.2, -21.78) * mm, "end": v(13.22, -17.8) * mm});
            skLineSegment(sketch, "E371", {"start": v(13.22, -12.8) * mm, "end": v(17.2, -12.8) * mm});
            skLineSegment(sketch, "E372", {"start": v(17.2, -12.8) * mm, "end": v(17.2, -16.78) * mm});
            skLineSegment(sketch, "E373", {"start": v(17.2, -16.78) * mm, "end": v(13.22, -12.8) * mm});
            skLineSegment(sketch, "E374", {"start": v(17.2, -11.78) * mm, "end": v(13.22, -7.8) * mm});
            skLineSegment(sketch, "E375", {"start": v(13.22, -7.8) * mm, "end": v(17.2, -7.8) * mm});
            skLineSegment(sketch, "E376", {"start": v(17.2, -7.8) * mm, "end": v(17.2, -11.78) * mm});
            skLineSegment(sketch, "E377", {"start": v(7.8, 22.2) * mm, "end": v(12.2, 22.2) * mm});
            skLineSegment(sketch, "E378", {"start": v(12.2, 22.2) * mm, "end": v(12.2, 17.8) * mm});
            skLineSegment(sketch, "E379", {"start": v(12.2, 17.8) * mm, "end": v(7.8, 17.8) * mm});
            skLineSegment(sketch, "E380", {"start": v(7.8, 17.8) * mm, "end": v(7.8, 22.2) * mm});
            skLineSegment(sketch, "E381", {"start": v(22.2, 12.8) * mm, "end": v(17.8, 12.8) * mm});
            skLineSegment(sketch, "E382", {"start": v(17.8, 12.8) * mm, "end": v(17.8, 17.2) * mm});
            skLineSegment(sketch, "E383", {"start": v(17.8, 17.2) * mm, "end": v(22.2, 17.2) * mm});
            skLineSegment(sketch, "E384", {"start": v(22.2, 17.2) * mm, "end": v(22.2, 12.8) * mm});
            skLineSegment(sketch, "E385", {"start": v(17.2, 2.8) * mm, "end": v(12.8, 2.8) * mm});
            skLineSegment(sketch, "E386", {"start": v(12.8, 2.8) * mm, "end": v(12.8, 7.2) * mm});
            skLineSegment(sketch, "E387", {"start": v(12.8, 7.2) * mm, "end": v(17.2, 7.2) * mm});
            skLineSegment(sketch, "E388", {"start": v(17.2, 7.2) * mm, "end": v(17.2, 2.8) * mm});
            skLineSegment(sketch, "E389", {"start": v(7.8, 17.2) * mm, "end": v(12.2, 17.2) * mm});
            skLineSegment(sketch, "E390", {"start": v(12.2, 17.2) * mm, "end": v(12.2, 12.8) * mm});
            skLineSegment(sketch, "E391", {"start": v(12.2, 12.8) * mm, "end": v(7.8, 12.8) * mm});
            skLineSegment(sketch, "E392", {"start": v(7.8, 12.8) * mm, "end": v(7.8, 17.2) * mm});
            skLineSegment(sketch, "E393", {"start": v(12.8, 27.2) * mm, "end": v(17.2, 27.2) * mm});
            skLineSegment(sketch, "E394", {"start": v(17.2, 27.2) * mm, "end": v(17.2, 22.8) * mm});
            skLineSegment(sketch, "E395", {"start": v(17.2, 22.8) * mm, "end": v(12.8, 22.8) * mm});
            skLineSegment(sketch, "E396", {"start": v(12.8, 22.8) * mm, "end": v(12.8, 27.2) * mm});
            skLineSegment(sketch, "E397", {"start": v(22.2, 17.8) * mm, "end": v(17.8, 17.8) * mm});
            skLineSegment(sketch, "E398", {"start": v(17.8, 17.8) * mm, "end": v(17.8, 22.2) * mm});
            skLineSegment(sketch, "E399", {"start": v(17.8, 22.2) * mm, "end": v(22.2, 22.2) * mm});
            skLineSegment(sketch, "E400", {"start": v(22.2, 22.2) * mm, "end": v(22.2, 17.8) * mm});
            skLineSegment(sketch, "E401", {"start": v(17.2, 7.8) * mm, "end": v(12.8, 7.8) * mm});
            skLineSegment(sketch, "E402", {"start": v(12.8, 7.8) * mm, "end": v(12.8, 12.2) * mm});
            skLineSegment(sketch, "E403", {"start": v(12.8, 12.2) * mm, "end": v(17.2, 12.2) * mm});
            skLineSegment(sketch, "E404", {"start": v(17.2, 12.2) * mm, "end": v(17.2, 7.8) * mm});
            skLineSegment(sketch, "E405", {"start": v(12.8, 22.2) * mm, "end": v(17.2, 22.2) * mm});
            skLineSegment(sketch, "E406", {"start": v(17.2, 22.2) * mm, "end": v(17.2, 17.8) * mm});
            skLineSegment(sketch, "E407", {"start": v(17.2, 17.8) * mm, "end": v(12.8, 17.8) * mm});
            skLineSegment(sketch, "E408", {"start": v(12.8, 17.8) * mm, "end": v(12.8, 22.2) * mm});
            skLineSegment(sketch, "E409", {"start": v(17.2, 12.8) * mm, "end": v(12.8, 12.8) * mm});
            skLineSegment(sketch, "E410", {"start": v(12.8, 12.8) * mm, "end": v(12.8, 17.2) * mm});
            skLineSegment(sketch, "E411", {"start": v(12.8, 17.2) * mm, "end": v(17.2, 17.2) * mm});
            skLineSegment(sketch, "E412", {"start": v(17.2, 17.2) * mm, "end": v(17.2, 12.8) * mm});
            skLineSegment(sketch, "E413", {"start": v(17.8, 22.8) * mm, "end": v(17.8, 27.2) * mm});
            skLineSegment(sketch, "E414", {"start": v(17.8, 27.2) * mm, "end": v(22.2, 27.2) * mm});
            skLineSegment(sketch, "E415", {"start": v(22.2, 27.2) * mm, "end": v(22.2, 22.8) * mm});
            skLineSegment(sketch, "E416", {"start": v(22.2, 22.8) * mm, "end": v(17.8, 22.8) * mm});
            skLineSegment(sketch, "E417", {"start": v(7.8, 12.2) * mm, "end": v(12.2, 12.2) * mm});
            skLineSegment(sketch, "E418", {"start": v(12.2, 12.2) * mm, "end": v(12.2, 7.8) * mm});
            skLineSegment(sketch, "E419", {"start": v(12.2, 7.8) * mm, "end": v(7.8, 7.8) * mm});
            skLineSegment(sketch, "E420", {"start": v(7.8, 7.8) * mm, "end": v(7.8, 12.2) * mm});
            skLineSegment(sketch, "E421", {"start": v(17.2, 2.2) * mm, "end": v(17.2, -1.78) * mm});
            skLineSegment(sketch, "E422", {"start": v(17.2, -1.78) * mm, "end": v(13.22, 2.2) * mm});
            skLineSegment(sketch, "E423", {"start": v(13.22, 2.2) * mm, "end": v(17.2, 2.2) * mm});
            skLineSegment(sketch, "E424", {"start": v(22.8, 22.2) * mm, "end": v(27.2, 22.2) * mm});
            skLineSegment(sketch, "E425", {"start": v(27.2, 22.2) * mm, "end": v(27.2, 17.8) * mm});
            skLineSegment(sketch, "E426", {"start": v(27.2, 17.8) * mm, "end": v(22.8, 17.8) * mm});
            skLineSegment(sketch, "E427", {"start": v(22.8, 17.8) * mm, "end": v(22.8, 22.2) * mm});
            skLineSegment(sketch, "E428", {"start": v(22.8, 22.8) * mm, "end": v(22.8, 27.2) * mm});
            skLineSegment(sketch, "E429", {"start": v(22.8, 27.2) * mm, "end": v(27.2, 27.2) * mm});
            skLineSegment(sketch, "E430", {"start": v(27.2, 27.2) * mm, "end": v(27.2, 22.8) * mm});
            skLineSegment(sketch, "E431", {"start": v(27.2, 22.8) * mm, "end": v(22.8, 22.8) * mm});
            skLineSegment(sketch, "E432", {"start": v(17.2, 28.22) * mm, "end": v(13.22, 32.2) * mm});
            skLineSegment(sketch, "E433", {"start": v(13.22, 32.2) * mm, "end": v(17.2, 32.2) * mm});
            skLineSegment(sketch, "E434", {"start": v(17.2, 32.2) * mm, "end": v(17.2, 28.22) * mm});
            skLineSegment(sketch, "E435", {"start": v(7.8, 27.2) * mm, "end": v(12.2, 27.2) * mm});
            skLineSegment(sketch, "E436", {"start": v(12.2, 27.2) * mm, "end": v(12.2, 22.8) * mm});
            skLineSegment(sketch, "E437", {"start": v(12.2, 22.8) * mm, "end": v(7.8, 22.8) * mm});
            skLineSegment(sketch, "E438", {"start": v(7.8, 22.8) * mm, "end": v(7.8, 27.2) * mm});
            skLineSegment(sketch, "E439", {"start": v(12.2, 7.2) * mm, "end": v(12.2, 2.8) * mm});
            skLineSegment(sketch, "E440", {"start": v(12.2, 2.8) * mm, "end": v(7.8, 2.8) * mm});
            skLineSegment(sketch, "E441", {"start": v(7.8, 2.8) * mm, "end": v(7.8, 7.2) * mm});
            skLineSegment(sketch, "E442", {"start": v(7.8, 7.2) * mm, "end": v(12.2, 7.2) * mm});
            skLineSegment(sketch, "E443", {"start": v(12.8, 1.78) * mm, "end": v(16.78, -2.2) * mm});
            skLineSegment(sketch, "E444", {"start": v(16.78, -2.2) * mm, "end": v(12.8, -2.2) * mm});
            skLineSegment(sketch, "E445", {"start": v(12.8, -2.2) * mm, "end": v(12.8, 1.78) * mm});
            skLineSegment(sketch, "E446", {"start": v(17.2, -2.8) * mm, "end": v(17.2, -6.78) * mm});
            skLineSegment(sketch, "E447", {"start": v(17.2, -6.78) * mm, "end": v(13.22, -2.8) * mm});
            skLineSegment(sketch, "E448", {"start": v(13.22, -2.8) * mm, "end": v(17.2, -2.8) * mm});
            skLineSegment(sketch, "E449", {"start": v(12.8, -3.22) * mm, "end": v(16.78, -7.2) * mm});
            skLineSegment(sketch, "E450", {"start": v(16.78, -7.2) * mm, "end": v(12.8, -7.2) * mm});
            skLineSegment(sketch, "E451", {"start": v(12.8, -7.2) * mm, "end": v(12.8, -3.22) * mm});
            skLineSegment(sketch, "E452", {"start": v(12.8, -8.22) * mm, "end": v(16.78, -12.2) * mm});
            skLineSegment(sketch, "E453", {"start": v(16.78, -12.2) * mm, "end": v(12.8, -12.2) * mm});
            skLineSegment(sketch, "E454", {"start": v(12.8, -12.2) * mm, "end": v(12.8, -10.27) * mm});
            skLineSegment(sketch, "E455", {"start": v(12.8, -10.27) * mm, "end": v(12.8, -8.22) * mm});
            skLineSegment(sketch, "E456", {"start": v(12.2, -12.8) * mm, "end": v(12.2, -16.78) * mm});
            skLineSegment(sketch, "E457", {"start": v(12.2, -16.78) * mm, "end": v(8.22, -12.8) * mm});
            skLineSegment(sketch, "E458", {"start": v(8.22, -12.8) * mm, "end": v(12.2, -12.8) * mm});
            skLineSegment(sketch, "E459", {"start": v(12.2, -21.78) * mm, "end": v(8.22, -17.8) * mm});
            skLineSegment(sketch, "E460", {"start": v(8.22, -17.8) * mm, "end": v(12.2, -17.8) * mm});
            skLineSegment(sketch, "E461", {"start": v(12.2, -17.8) * mm, "end": v(12.2, -21.78) * mm});
            skLineSegment(sketch, "E462", {"start": v(12.2, -25) * mm, "end": v(12.2, -26.78) * mm});
            skLineSegment(sketch, "E463", {"start": v(12.2, -26.78) * mm, "end": v(8.22, -22.8) * mm});
            skLineSegment(sketch, "E464", {"start": v(8.22, -22.8) * mm, "end": v(12.2, -22.8) * mm});
            skLineSegment(sketch, "E465", {"start": v(12.2, -22.8) * mm, "end": v(12.2, -25) * mm});
            skLineSegment(sketch, "E466", {"start": v(12.8, -28.22) * mm, "end": v(16.78, -32.2) * mm});
            skLineSegment(sketch, "E467", {"start": v(16.78, -32.2) * mm, "end": v(12.8, -32.2) * mm});
            skLineSegment(sketch, "E468", {"start": v(12.8, -32.2) * mm, "end": v(12.8, -30.27) * mm});
            skLineSegment(sketch, "E469", {"start": v(12.8, -30.27) * mm, "end": v(12.8, -28.22) * mm});
            skLineSegment(sketch, "E470", {"start": v(17.8, -8.22) * mm, "end": v(21.78, -12.2) * mm});
            skLineSegment(sketch, "E471", {"start": v(21.78, -12.2) * mm, "end": v(17.8, -12.2) * mm});
            skLineSegment(sketch, "E472", {"start": v(17.8, -12.2) * mm, "end": v(17.8, -8.22) * mm});
            skLineSegment(sketch, "E473", {"start": v(22.2, 2.8) * mm, "end": v(17.8, 2.8) * mm});
            skLineSegment(sketch, "E474", {"start": v(17.8, 2.8) * mm, "end": v(17.8, 7.2) * mm});
            skLineSegment(sketch, "E475", {"start": v(17.8, 7.2) * mm, "end": v(22.2, 7.2) * mm});
            skLineSegment(sketch, "E476", {"start": v(22.2, 7.2) * mm, "end": v(22.2, 2.8) * mm});
            skLineSegment(sketch, "E477", {"start": v(22.8, 17.2) * mm, "end": v(27.2, 17.2) * mm});
            skLineSegment(sketch, "E478", {"start": v(27.2, 17.2) * mm, "end": v(27.2, 12.8) * mm});
            skLineSegment(sketch, "E479", {"start": v(27.2, 12.8) * mm, "end": v(22.8, 12.8) * mm});
            skLineSegment(sketch, "E480", {"start": v(22.8, 12.8) * mm, "end": v(22.8, 17.2) * mm});
            skLineSegment(sketch, "E481", {"start": v(17.8, 27.8) * mm, "end": v(17.8, 31.78) * mm});
            skLineSegment(sketch, "E482", {"start": v(17.8, 31.78) * mm, "end": v(21.78, 27.8) * mm});
            skLineSegment(sketch, "E483", {"start": v(21.78, 27.8) * mm, "end": v(17.8, 27.8) * mm});
            skLineSegment(sketch, "E484", {"start": v(17.8, 36.78) * mm, "end": v(21.78, 32.8) * mm});
            skLineSegment(sketch, "E485", {"start": v(21.78, 32.8) * mm, "end": v(17.8, 32.8) * mm});
            skLineSegment(sketch, "E486", {"start": v(17.8, 32.8) * mm, "end": v(17.8, 36.78) * mm});
            skLineSegment(sketch, "E487", {"start": v(17.8, 41.78) * mm, "end": v(21.78, 37.8) * mm});
            skLineSegment(sketch, "E488", {"start": v(21.78, 37.8) * mm, "end": v(17.8, 37.8) * mm});
            skLineSegment(sketch, "E489", {"start": v(17.8, 37.8) * mm, "end": v(17.8, 41.78) * mm});
            skLineSegment(sketch, "E490", {"start": v(12.8, 31.78) * mm, "end": v(16.78, 27.8) * mm});
            skLineSegment(sketch, "E491", {"start": v(16.78, 27.8) * mm, "end": v(12.8, 27.8) * mm});
            skLineSegment(sketch, "E492", {"start": v(12.8, 27.8) * mm, "end": v(12.8, 29.73) * mm});
            skLineSegment(sketch, "E493", {"start": v(12.8, 29.73) * mm, "end": v(12.8, 31.78) * mm});
            skLineSegment(sketch, "E494", {"start": v(7.2, 17.8) * mm, "end": v(2.8, 17.8) * mm});
            skLineSegment(sketch, "E495", {"start": v(2.8, 17.8) * mm, "end": v(2.8, 22.2) * mm});
            skLineSegment(sketch, "E496", {"start": v(2.8, 22.2) * mm, "end": v(7.2, 22.2) * mm});
            skLineSegment(sketch, "E497", {"start": v(7.2, 22.2) * mm, "end": v(7.2, 17.8) * mm});
            skLineSegment(sketch, "E498", {"start": v(-12.8, 13.22) * mm, "end": v(-16.78, 17.2) * mm});
            skLineSegment(sketch, "E499", {"start": v(-16.78, 17.2) * mm, "end": v(-12.8, 17.2) * mm});
            skLineSegment(sketch, "E500", {"start": v(-12.8, 17.2) * mm, "end": v(-12.8, 13.22) * mm});
            skLineSegment(sketch, "E501", {"start": v(-12.2, 16.78) * mm, "end": v(-8.22, 12.8) * mm});
            skLineSegment(sketch, "E502", {"start": v(-8.22, 12.8) * mm, "end": v(-12.2, 12.8) * mm});
            skLineSegment(sketch, "E503", {"start": v(-12.2, 12.8) * mm, "end": v(-12.2, 16.78) * mm});
            skLineSegment(sketch, "E504", {"start": v(-7.2, 16.78) * mm, "end": v(-3.22, 12.8) * mm});
            skLineSegment(sketch, "E505", {"start": v(-3.22, 12.8) * mm, "end": v(-7.2, 12.8) * mm});
            skLineSegment(sketch, "E506", {"start": v(-7.2, 12.8) * mm, "end": v(-7.2, 16.78) * mm});
            skLineSegment(sketch, "E507", {"start": v(-2.2, 16.78) * mm, "end": v(1.78, 12.8) * mm});
            skLineSegment(sketch, "E508", {"start": v(1.78, 12.8) * mm, "end": v(-2.2, 12.8) * mm});
            skLineSegment(sketch, "E509", {"start": v(-2.2, 12.8) * mm, "end": v(-2.2, 16.78) * mm});
            skLineSegment(sketch, "E510", {"start": v(2.8, 12.2) * mm, "end": v(7.2, 12.2) * mm});
            skLineSegment(sketch, "E511", {"start": v(7.2, 12.2) * mm, "end": v(7.2, 7.8) * mm});
            skLineSegment(sketch, "E512", {"start": v(7.2, 7.8) * mm, "end": v(2.8, 7.8) * mm});
            skLineSegment(sketch, "E513", {"start": v(2.8, 7.8) * mm, "end": v(2.8, 12.2) * mm});
            skLineSegment(sketch, "E514", {"start": v(12.2, 2.2) * mm, "end": v(12.2, -1.78) * mm});
            skLineSegment(sketch, "E515", {"start": v(12.2, -1.78) * mm, "end": v(8.22, 2.2) * mm});
            skLineSegment(sketch, "E516", {"start": v(8.22, 2.2) * mm, "end": v(12.2, 2.2) * mm});
            skLineSegment(sketch, "E517", {"start": v(12.2, -6.78) * mm, "end": v(8.22, -2.8) * mm});
            skLineSegment(sketch, "E518", {"start": v(8.22, -2.8) * mm, "end": v(12.2, -2.8) * mm});
            skLineSegment(sketch, "E519", {"start": v(12.2, -2.8) * mm, "end": v(12.2, -6.78) * mm});
            skLineSegment(sketch, "E520", {"start": v(12.2, -10) * mm, "end": v(12.2, -11.78) * mm});
            skLineSegment(sketch, "E521", {"start": v(12.2, -11.78) * mm, "end": v(8.22, -7.8) * mm});
            skLineSegment(sketch, "E522", {"start": v(8.22, -7.8) * mm, "end": v(12.2, -7.8) * mm});
            skLineSegment(sketch, "E523", {"start": v(12.2, -7.8) * mm, "end": v(12.2, -10) * mm});
            skLineSegment(sketch, "E524", {"start": v(11.78, -12.2) * mm, "end": v(7.8, -12.2) * mm});
            skLineSegment(sketch, "E525", {"start": v(7.8, -12.2) * mm, "end": v(7.8, -8.22) * mm});
            skLineSegment(sketch, "E526", {"start": v(7.8, -8.22) * mm, "end": v(11.78, -12.2) * mm});
            skLineSegment(sketch, "E527", {"start": v(7.8, -13.22) * mm, "end": v(11.78, -17.2) * mm});
            skLineSegment(sketch, "E528", {"start": v(11.78, -17.2) * mm, "end": v(7.8, -17.2) * mm});
            skLineSegment(sketch, "E529", {"start": v(7.8, -17.2) * mm, "end": v(7.8, -13.22) * mm});
            skLineSegment(sketch, "E530", {"start": v(7.8, -18.22) * mm, "end": v(11.78, -22.2) * mm});
            skLineSegment(sketch, "E531", {"start": v(11.78, -22.2) * mm, "end": v(7.8, -22.2) * mm});
            skLineSegment(sketch, "E532", {"start": v(7.8, -22.2) * mm, "end": v(7.8, -18.22) * mm});
            skLineSegment(sketch, "E533", {"start": v(11.78, -27.2) * mm, "end": v(7.8, -27.2) * mm});
            skLineSegment(sketch, "E534", {"start": v(7.8, -27.2) * mm, "end": v(7.8, -23.22) * mm});
            skLineSegment(sketch, "E535", {"start": v(7.8, -23.22) * mm, "end": v(11.78, -27.2) * mm});
            skLineSegment(sketch, "E536", {"start": v(12.2, -27.8) * mm, "end": v(12.2, -30) * mm});
            skLineSegment(sketch, "E537", {"start": v(12.2, -30) * mm, "end": v(12.2, -31.78) * mm});
            skLineSegment(sketch, "E538", {"start": v(12.2, -31.78) * mm, "end": v(8.22, -27.8) * mm});
            skLineSegment(sketch, "E539", {"start": v(8.22, -27.8) * mm, "end": v(12.2, -27.8) * mm});
            skLineSegment(sketch, "E540", {"start": v(11.78, -37.2) * mm, "end": v(7.8, -37.2) * mm});
            skLineSegment(sketch, "E541", {"start": v(7.8, -37.2) * mm, "end": v(7.8, -33.22) * mm});
            skLineSegment(sketch, "E542", {"start": v(7.8, -33.22) * mm, "end": v(11.78, -37.2) * mm});
            skLineSegment(sketch, "E543", {"start": v(8.22, -32.8) * mm, "end": v(12.2, -32.8) * mm});
            skLineSegment(sketch, "E544", {"start": v(12.2, -32.8) * mm, "end": v(12.2, -36.78) * mm});
            skLineSegment(sketch, "E545", {"start": v(12.2, -36.78) * mm, "end": v(8.22, -32.8) * mm});
            skLineSegment(sketch, "E546", {"start": v(12.8, -37.2) * mm, "end": v(12.8, -33.22) * mm});
            skLineSegment(sketch, "E547", {"start": v(12.8, -33.22) * mm, "end": v(16.78, -37.2) * mm});
            skLineSegment(sketch, "E548", {"start": v(16.78, -37.2) * mm, "end": v(12.8, -37.2) * mm});
            skLineSegment(sketch, "E549", {"start": v(18.22, -7.8) * mm, "end": v(22.2, -7.8) * mm});
            skLineSegment(sketch, "E550", {"start": v(22.2, -7.8) * mm, "end": v(22.2, -11.78) * mm});
            skLineSegment(sketch, "E551", {"start": v(22.2, -11.78) * mm, "end": v(18.22, -7.8) * mm});
            skLineSegment(sketch, "E552", {"start": v(22.8, 12.2) * mm, "end": v(27.2, 12.2) * mm});
            skLineSegment(sketch, "E553", {"start": v(27.2, 12.2) * mm, "end": v(27.2, 7.8) * mm});
            skLineSegment(sketch, "E554", {"start": v(27.2, 7.8) * mm, "end": v(22.8, 7.8) * mm});
            skLineSegment(sketch, "E555", {"start": v(22.8, 7.8) * mm, "end": v(22.8, 12.2) * mm});
            skLineSegment(sketch, "E556", {"start": v(27.8, 12.8) * mm, "end": v(27.8, 16.78) * mm});
            skLineSegment(sketch, "E557", {"start": v(27.8, 16.78) * mm, "end": v(31.78, 12.8) * mm});
            skLineSegment(sketch, "E558", {"start": v(31.78, 12.8) * mm, "end": v(30, 12.8) * mm});
            skLineSegment(sketch, "E559", {"start": v(30, 12.8) * mm, "end": v(27.8, 12.8) * mm});
            skLineSegment(sketch, "E560", {"start": v(28.22, 17.2) * mm, "end": v(32.2, 17.2) * mm});
            skLineSegment(sketch, "E561", {"start": v(32.2, 17.2) * mm, "end": v(32.2, 13.22) * mm});
            skLineSegment(sketch, "E562", {"start": v(32.2, 13.22) * mm, "end": v(28.22, 17.2) * mm});
            skLineSegment(sketch, "E563", {"start": v(42.2, 17.2) * mm, "end": v(42.2, 13.22) * mm});
            skLineSegment(sketch, "E564", {"start": v(42.2, 13.22) * mm, "end": v(38.22, 17.2) * mm});
            skLineSegment(sketch, "E565", {"start": v(38.22, 17.2) * mm, "end": v(42.2, 17.2) * mm});
            skLineSegment(sketch, "E566", {"start": v(42.2, 18.22) * mm, "end": v(38.22, 22.2) * mm});
            skLineSegment(sketch, "E567", {"start": v(38.22, 22.2) * mm, "end": v(42.2, 22.2) * mm});
            skLineSegment(sketch, "E568", {"start": v(42.2, 22.2) * mm, "end": v(42.2, 18.22) * mm});
            skLineSegment(sketch, "E569", {"start": v(41.78, 17.8) * mm, "end": v(37.8, 17.8) * mm});
            skLineSegment(sketch, "E570", {"start": v(37.8, 17.8) * mm, "end": v(37.8, 21.78) * mm});
            skLineSegment(sketch, "E571", {"start": v(37.8, 21.78) * mm, "end": v(41.78, 17.8) * mm});
            skLineSegment(sketch, "E572", {"start": v(27.8, 17.8) * mm, "end": v(27.8, 21.78) * mm});
            skLineSegment(sketch, "E573", {"start": v(27.8, 21.78) * mm, "end": v(31.78, 17.8) * mm});
            skLineSegment(sketch, "E574", {"start": v(31.78, 17.8) * mm, "end": v(27.8, 17.8) * mm});
            skLineSegment(sketch, "E575", {"start": v(22.2, 28.22) * mm, "end": v(18.22, 32.2) * mm});
            skLineSegment(sketch, "E576", {"start": v(18.22, 32.2) * mm, "end": v(22.2, 32.2) * mm});
            skLineSegment(sketch, "E577", {"start": v(22.2, 32.2) * mm, "end": v(22.2, 28.22) * mm});
            skLineSegment(sketch, "E578", {"start": v(22.2, 33.22) * mm, "end": v(18.22, 37.2) * mm});
            skLineSegment(sketch, "E579", {"start": v(18.22, 37.2) * mm, "end": v(22.2, 37.2) * mm});
            skLineSegment(sketch, "E580", {"start": v(22.2, 37.2) * mm, "end": v(22.2, 33.22) * mm});
            skLineSegment(sketch, "E581", {"start": v(22.8, 46.78) * mm, "end": v(26.78, 42.8) * mm});
            skLineSegment(sketch, "E582", {"start": v(26.78, 42.8) * mm, "end": v(22.8, 42.8) * mm});
            skLineSegment(sketch, "E583", {"start": v(22.8, 42.8) * mm, "end": v(22.8, 46.78) * mm});
            skLineSegment(sketch, "E584", {"start": v(22.8, 41.78) * mm, "end": v(26.78, 37.8) * mm});
            skLineSegment(sketch, "E585", {"start": v(26.78, 37.8) * mm, "end": v(22.8, 37.8) * mm});
            skLineSegment(sketch, "E586", {"start": v(22.8, 37.8) * mm, "end": v(22.8, 41.78) * mm});
            skLineSegment(sketch, "E587", {"start": v(22.2, 43.22) * mm, "end": v(18.22, 47.2) * mm});
            skLineSegment(sketch, "E588", {"start": v(18.22, 47.2) * mm, "end": v(22.2, 47.2) * mm});
            skLineSegment(sketch, "E589", {"start": v(22.2, 47.2) * mm, "end": v(22.2, 43.22) * mm});
            skLineSegment(sketch, "E590", {"start": v(22.2, 38.22) * mm, "end": v(18.22, 42.2) * mm});
            skLineSegment(sketch, "E591", {"start": v(18.22, 42.2) * mm, "end": v(22.2, 42.2) * mm});
            skLineSegment(sketch, "E592", {"start": v(22.2, 42.2) * mm, "end": v(22.2, 38.22) * mm});
            skLineSegment(sketch, "E593", {"start": v(17.2, 42.2) * mm, "end": v(17.2, 38.22) * mm});
            skLineSegment(sketch, "E594", {"start": v(17.2, 38.22) * mm, "end": v(13.22, 42.2) * mm});
            skLineSegment(sketch, "E595", {"start": v(13.22, 42.2) * mm, "end": v(17.2, 42.2) * mm});
            skLineSegment(sketch, "E596", {"start": v(17.2, 33.22) * mm, "end": v(13.22, 37.2) * mm});
            skLineSegment(sketch, "E597", {"start": v(13.22, 37.2) * mm, "end": v(17.2, 37.2) * mm});
            skLineSegment(sketch, "E598", {"start": v(17.2, 37.2) * mm, "end": v(17.2, 33.22) * mm});
            skLineSegment(sketch, "E599", {"start": v(12.2, 33.22) * mm, "end": v(8.22, 37.2) * mm});
            skLineSegment(sketch, "E600", {"start": v(8.22, 37.2) * mm, "end": v(12.2, 37.2) * mm});
            skLineSegment(sketch, "E601", {"start": v(12.2, 37.2) * mm, "end": v(12.2, 33.22) * mm});
            skLineSegment(sketch, "E602", {"start": v(12.2, 30) * mm, "end": v(12.2, 28.22) * mm});
            skLineSegment(sketch, "E603", {"start": v(12.2, 28.22) * mm, "end": v(8.22, 32.2) * mm});
            skLineSegment(sketch, "E604", {"start": v(8.22, 32.2) * mm, "end": v(12.2, 32.2) * mm});
            skLineSegment(sketch, "E605", {"start": v(12.2, 32.2) * mm, "end": v(12.2, 30) * mm});
            skLineSegment(sketch, "E606", {"start": v(11.78, 27.8) * mm, "end": v(7.8, 27.8) * mm});
            skLineSegment(sketch, "E607", {"start": v(7.8, 27.8) * mm, "end": v(7.8, 31.78) * mm});
            skLineSegment(sketch, "E608", {"start": v(7.8, 31.78) * mm, "end": v(11.78, 27.8) * mm});
            skLineSegment(sketch, "E609", {"start": v(7.2, 27.2) * mm, "end": v(7.2, 22.8) * mm});
            skLineSegment(sketch, "E610", {"start": v(7.2, 22.8) * mm, "end": v(2.8, 22.8) * mm});
            skLineSegment(sketch, "E611", {"start": v(2.8, 22.8) * mm, "end": v(2.8, 27.2) * mm});
            skLineSegment(sketch, "E612", {"start": v(2.8, 27.2) * mm, "end": v(7.2, 27.2) * mm});
            skLineSegment(sketch, "E613", {"start": v(-2.2, 17.8) * mm, "end": v(-2.2, 20) * mm});
            skLineSegment(sketch, "E614", {"start": v(-2.2, 20) * mm, "end": v(-2.2, 21.78) * mm});
            skLineSegment(sketch, "E615", {"start": v(-2.2, 21.78) * mm, "end": v(1.78, 17.8) * mm});
            skLineSegment(sketch, "E616", {"start": v(1.78, 17.8) * mm, "end": v(-2.2, 17.8) * mm});
            skLineSegment(sketch, "E617", {"start": v(-12.2, 17.8) * mm, "end": v(-12.2, 21.78) * mm});
            skLineSegment(sketch, "E618", {"start": v(-12.2, 21.78) * mm, "end": v(-8.22, 17.8) * mm});
            skLineSegment(sketch, "E619", {"start": v(-8.22, 17.8) * mm, "end": v(-12.2, 17.8) * mm});
            skLineSegment(sketch, "E620", {"start": v(-32.2, 16.78) * mm, "end": v(-28.22, 12.8) * mm});
            skLineSegment(sketch, "E621", {"start": v(-28.22, 12.8) * mm, "end": v(-32.2, 12.8) * mm});
            skLineSegment(sketch, "E622", {"start": v(-32.2, 12.8) * mm, "end": v(-32.2, 16.78) * mm});
            skLineSegment(sketch, "E623", {"start": v(-37.8, 12.2) * mm, "end": v(-37.8, 8.22) * mm});
            skLineSegment(sketch, "E624", {"start": v(-37.8, 8.22) * mm, "end": v(-41.78, 12.2) * mm});
            skLineSegment(sketch, "E625", {"start": v(-41.78, 12.2) * mm, "end": v(-37.8, 12.2) * mm});
            skLineSegment(sketch, "E626", {"start": v(-42.8, -1.78) * mm, "end": v(-46.78, 2.2) * mm});
            skLineSegment(sketch, "E627", {"start": v(-46.78, 2.2) * mm, "end": v(-42.8, 2.2) * mm});
            skLineSegment(sketch, "E628", {"start": v(-42.8, 2.2) * mm, "end": v(-42.8, -1.78) * mm});
            skLineSegment(sketch, "E629", {"start": v(-51.78, -2.8) * mm, "end": v(-47.8, -2.8) * mm});
            skLineSegment(sketch, "E630", {"start": v(-47.8, -2.8) * mm, "end": v(-47.8, -6.78) * mm});
            skLineSegment(sketch, "E631", {"start": v(-47.8, -6.78) * mm, "end": v(-51.78, -2.8) * mm});
            skLineSegment(sketch, "E632", {"start": v(-56.78, -2.8) * mm, "end": v(-52.8, -2.8) * mm});
            skLineSegment(sketch, "E633", {"start": v(-52.8, -2.8) * mm, "end": v(-52.8, -6.78) * mm});
            skLineSegment(sketch, "E634", {"start": v(-52.8, -6.78) * mm, "end": v(-56.78, -2.8) * mm});
            skLineSegment(sketch, "E635", {"start": v(-47.8, -1.78) * mm, "end": v(-51.78, 2.2) * mm});
            skLineSegment(sketch, "E636", {"start": v(-51.78, 2.2) * mm, "end": v(-47.8, 2.2) * mm});
            skLineSegment(sketch, "E637", {"start": v(-47.8, 2.2) * mm, "end": v(-47.8, -1.78) * mm});
            skLineSegment(sketch, "E638", {"start": v(-48.23, -2.2) * mm, "end": v(-52.2, -2.2) * mm});
            skLineSegment(sketch, "E639", {"start": v(-52.2, -2.2) * mm, "end": v(-52.2, 1.78) * mm});
            skLineSegment(sketch, "E640", {"start": v(-52.2, 1.78) * mm, "end": v(-48.23, -2.2) * mm});
            skLineSegment(sketch, "E641", {"start": v(-43.22, -2.2) * mm, "end": v(-47.2, -2.2) * mm});
            skLineSegment(sketch, "E642", {"start": v(-47.2, -2.2) * mm, "end": v(-47.2, 1.78) * mm});
            skLineSegment(sketch, "E643", {"start": v(-47.2, 1.78) * mm, "end": v(-43.22, -2.2) * mm});
            skLineSegment(sketch, "E644", {"start": v(-47.2, 2.8) * mm, "end": v(-47.2, 6.78) * mm});
            skLineSegment(sketch, "E645", {"start": v(-47.2, 6.78) * mm, "end": v(-43.22, 2.8) * mm});
            skLineSegment(sketch, "E646", {"start": v(-43.22, 2.8) * mm, "end": v(-47.2, 2.8) * mm});
            skLineSegment(sketch, "E647", {"start": v(-46.78, 7.2) * mm, "end": v(-42.8, 7.2) * mm});
            skLineSegment(sketch, "E648", {"start": v(-42.8, 7.2) * mm, "end": v(-42.8, 3.22) * mm});
            skLineSegment(sketch, "E649", {"start": v(-42.8, 3.22) * mm, "end": v(-46.78, 7.2) * mm});
            skLineSegment(sketch, "E650", {"start": v(-52.8, -1.78) * mm, "end": v(-56.78, 2.2) * mm});
            skLineSegment(sketch, "E651", {"start": v(-56.78, 2.2) * mm, "end": v(-52.8, 2.2) * mm});
            skLineSegment(sketch, "E652", {"start": v(-52.8, 2.2) * mm, "end": v(-52.8, -1.78) * mm});
            skLineSegment(sketch, "E653", {"start": v(-57.8, -6.77) * mm, "end": v(-61.78, -2.8) * mm});
            skLineSegment(sketch, "E654", {"start": v(-61.78, -2.8) * mm, "end": v(-57.8, -2.8) * mm});
            skLineSegment(sketch, "E655", {"start": v(-57.8, -2.8) * mm, "end": v(-57.8, -6.77) * mm});
            skLineSegment(sketch, "E656", {"start": v(-57.8, -11.78) * mm, "end": v(-61.78, -7.8) * mm});
            skLineSegment(sketch, "E657", {"start": v(-61.78, -7.8) * mm, "end": v(-57.8, -7.8) * mm});
            skLineSegment(sketch, "E658", {"start": v(-57.8, -7.8) * mm, "end": v(-57.8, -11.78) * mm});
            skLineSegment(sketch, "E659", {"start": v(-57.2, -12.2) * mm, "end": v(-57.2, -8.22) * mm});
            skLineSegment(sketch, "E660", {"start": v(-57.2, -8.22) * mm, "end": v(-53.22, -12.2) * mm});
            skLineSegment(sketch, "E661", {"start": v(-53.22, -12.2) * mm, "end": v(-57.2, -12.2) * mm});
            skLineSegment(sketch, "E662", {"start": v(-57.2, -3.22) * mm, "end": v(-53.22, -7.2) * mm});
            skLineSegment(sketch, "E663", {"start": v(-53.22, -7.2) * mm, "end": v(-57.2, -7.2) * mm});
            skLineSegment(sketch, "E664", {"start": v(-57.2, -7.2) * mm, "end": v(-57.2, -3.22) * mm});
            skLineSegment(sketch, "E665", {"start": v(-52.2, -3.22) * mm, "end": v(-48.22, -7.2) * mm});
            skLineSegment(sketch, "E666", {"start": v(-48.22, -7.2) * mm, "end": v(-52.2, -7.2) * mm});
            skLineSegment(sketch, "E667", {"start": v(-52.2, -7.2) * mm, "end": v(-52.2, -3.22) * mm});
            skLineSegment(sketch, "E668", {"start": v(-42.2, 1.78) * mm, "end": v(-38.22, -2.2) * mm});
            skLineSegment(sketch, "E669", {"start": v(-38.22, -2.2) * mm, "end": v(-42.2, -2.2) * mm});
            skLineSegment(sketch, "E670", {"start": v(-42.2, -2.2) * mm, "end": v(-42.2, 1.78) * mm});
            skLineSegment(sketch, "E671", {"start": v(-42.2, 6.78) * mm, "end": v(-38.22, 2.8) * mm});
            skLineSegment(sketch, "E672", {"start": v(-38.22, 2.8) * mm, "end": v(-42.2, 2.8) * mm});
            skLineSegment(sketch, "E673", {"start": v(-42.2, 2.8) * mm, "end": v(-42.2, 6.78) * mm});
            skLineSegment(sketch, "E674", {"start": v(-41.78, 7.2) * mm, "end": v(-37.8, 7.2) * mm});
            skLineSegment(sketch, "E675", {"start": v(-37.8, 7.2) * mm, "end": v(-37.8, 3.22) * mm});
            skLineSegment(sketch, "E676", {"start": v(-37.8, 3.22) * mm, "end": v(-41.78, 7.2) * mm});
            skLineSegment(sketch, "E677", {"start": v(-37.2, 11.78) * mm, "end": v(-33.22, 7.8) * mm});
            skLineSegment(sketch, "E678", {"start": v(-33.22, 7.8) * mm, "end": v(-37.2, 7.8) * mm});
            skLineSegment(sketch, "E679", {"start": v(-37.2, 7.8) * mm, "end": v(-37.2, 11.78) * mm});
            skLineSegment(sketch, "E680", {"start": v(-36.78, 12.2) * mm, "end": v(-32.8, 12.2) * mm});
            skLineSegment(sketch, "E681", {"start": v(-32.8, 12.2) * mm, "end": v(-32.8, 8.22) * mm});
            skLineSegment(sketch, "E682", {"start": v(-32.8, 8.22) * mm, "end": v(-36.78, 12.2) * mm});
            skLineSegment(sketch, "E683", {"start": v(-27.8, 12.2) * mm, "end": v(-27.8, 8.22) * mm});
            skLineSegment(sketch, "E684", {"start": v(-27.8, 8.22) * mm, "end": v(-31.78, 12.2) * mm});
            skLineSegment(sketch, "E685", {"start": v(-31.78, 12.2) * mm, "end": v(-27.8, 12.2) * mm});
            skLineSegment(sketch, "E686", {"start": v(-27.2, 11.78) * mm, "end": v(-23.22, 7.8) * mm});
            skLineSegment(sketch, "E687", {"start": v(-23.22, 7.8) * mm, "end": v(-27.2, 7.8) * mm});
            skLineSegment(sketch, "E688", {"start": v(-27.2, 7.8) * mm, "end": v(-27.2, 11.78) * mm});
            skLineSegment(sketch, "E689", {"start": v(-26.78, 12.2) * mm, "end": v(-22.8, 12.2) * mm});
            skLineSegment(sketch, "E690", {"start": v(-22.8, 12.2) * mm, "end": v(-22.8, 8.22) * mm});
            skLineSegment(sketch, "E691", {"start": v(-22.8, 8.22) * mm, "end": v(-26.78, 12.2) * mm});
            skLineSegment(sketch, "E692", {"start": v(-12.8, 12.2) * mm, "end": v(-12.8, 8.22) * mm});
            skLineSegment(sketch, "E693", {"start": v(-12.8, 8.22) * mm, "end": v(-16.78, 12.2) * mm});
            skLineSegment(sketch, "E694", {"start": v(-16.78, 12.2) * mm, "end": v(-12.8, 12.2) * mm});
            skLineSegment(sketch, "E695", {"start": v(-12.2, 11.78) * mm, "end": v(-8.22, 7.8) * mm});
            skLineSegment(sketch, "E696", {"start": v(-8.22, 7.8) * mm, "end": v(-12.2, 7.8) * mm});
            skLineSegment(sketch, "E697", {"start": v(-12.2, 7.8) * mm, "end": v(-12.2, 11.78) * mm});
            skLineSegment(sketch, "E698", {"start": v(-7.8, 8.22) * mm, "end": v(-11.78, 12.2) * mm});
            skLineSegment(sketch, "E699", {"start": v(-11.78, 12.2) * mm, "end": v(-7.8, 12.2) * mm});
            skLineSegment(sketch, "E700", {"start": v(-7.8, 12.2) * mm, "end": v(-7.8, 8.22) * mm});
            skLineSegment(sketch, "E701", {"start": v(2.2, 12.2) * mm, "end": v(2.2, 8.22) * mm});
            skLineSegment(sketch, "E702", {"start": v(2.2, 8.22) * mm, "end": v(-1.78, 12.2) * mm});
            skLineSegment(sketch, "E703", {"start": v(-1.78, 12.2) * mm, "end": v(2.2, 12.2) * mm});
            skLineSegment(sketch, "E704", {"start": v(2.8, 7.2) * mm, "end": v(7.2, 7.2) * mm});
            skLineSegment(sketch, "E705", {"start": v(7.2, 7.2) * mm, "end": v(7.2, 2.8) * mm});
            skLineSegment(sketch, "E706", {"start": v(7.2, 2.8) * mm, "end": v(2.8, 2.8) * mm});
            skLineSegment(sketch, "E707", {"start": v(2.8, 2.8) * mm, "end": v(2.8, 5) * mm});
            skLineSegment(sketch, "E708", {"start": v(2.8, 5) * mm, "end": v(2.8, 7.2) * mm});
            skLineSegment(sketch, "E709", {"start": v(7.8, 1.78) * mm, "end": v(11.78, -2.2) * mm});
            skLineSegment(sketch, "E710", {"start": v(11.78, -2.2) * mm, "end": v(7.8, -2.2) * mm});
            skLineSegment(sketch, "E711", {"start": v(7.8, -2.2) * mm, "end": v(7.8, 1.78) * mm});
            skLineSegment(sketch, "E712", {"start": v(7.8, -3.22) * mm, "end": v(11.78, -7.2) * mm});
            skLineSegment(sketch, "E713", {"start": v(11.78, -7.2) * mm, "end": v(7.8, -7.2) * mm});
            skLineSegment(sketch, "E714", {"start": v(7.8, -7.2) * mm, "end": v(7.8, -3.22) * mm});
            skLineSegment(sketch, "E715", {"start": v(7.2, -12.8) * mm, "end": v(7.2, -16.78) * mm});
            skLineSegment(sketch, "E716", {"start": v(7.2, -16.78) * mm, "end": v(3.22, -12.8) * mm});
            skLineSegment(sketch, "E717", {"start": v(3.22, -12.8) * mm, "end": v(7.2, -12.8) * mm});
            skLineSegment(sketch, "E718", {"start": v(7.2, -21.78) * mm, "end": v(3.22, -17.8) * mm});
            skLineSegment(sketch, "E719", {"start": v(3.22, -17.8) * mm, "end": v(7.2, -17.8) * mm});
            skLineSegment(sketch, "E720", {"start": v(7.2, -17.8) * mm, "end": v(7.2, -21.78) * mm});
            skLineSegment(sketch, "E721", {"start": v(7.8, -28.22) * mm, "end": v(11.78, -32.2) * mm});
            skLineSegment(sketch, "E722", {"start": v(11.78, -32.2) * mm, "end": v(7.8, -32.2) * mm});
            skLineSegment(sketch, "E723", {"start": v(7.8, -32.2) * mm, "end": v(7.8, -28.22) * mm});
            skLineSegment(sketch, "E724", {"start": v(6.78, -37.2) * mm, "end": v(2.8, -37.2) * mm});
            skLineSegment(sketch, "E725", {"start": v(2.8, -37.2) * mm, "end": v(2.8, -33.22) * mm});
            skLineSegment(sketch, "E726", {"start": v(2.8, -33.22) * mm, "end": v(6.78, -37.2) * mm});
            skLineSegment(sketch, "E727", {"start": v(2.8, -38.22) * mm, "end": v(6.78, -42.2) * mm});
            skLineSegment(sketch, "E728", {"start": v(6.78, -42.2) * mm, "end": v(2.8, -42.2) * mm});
            skLineSegment(sketch, "E729", {"start": v(2.8, -42.2) * mm, "end": v(2.8, -38.22) * mm});
            skLineSegment(sketch, "E730", {"start": v(2.2, -46.78) * mm, "end": v(-1.78, -42.8) * mm});
            skLineSegment(sketch, "E731", {"start": v(-1.78, -42.8) * mm, "end": v(2.2, -42.8) * mm});
            skLineSegment(sketch, "E732", {"start": v(2.2, -42.8) * mm, "end": v(2.2, -46.78) * mm});
            skLineSegment(sketch, "E733", {"start": v(-2.8, -46.78) * mm, "end": v(-6.78, -42.8) * mm});
            skLineSegment(sketch, "E734", {"start": v(-6.78, -42.8) * mm, "end": v(-2.8, -42.8) * mm});
            skLineSegment(sketch, "E735", {"start": v(-2.8, -42.8) * mm, "end": v(-2.8, -46.78) * mm});
            skLineSegment(sketch, "E736", {"start": v(-3.22, -47.2) * mm, "end": v(-7.2, -47.2) * mm});
            skLineSegment(sketch, "E737", {"start": v(-7.2, -47.2) * mm, "end": v(-7.2, -43.22) * mm});
            skLineSegment(sketch, "E738", {"start": v(-7.2, -43.22) * mm, "end": v(-3.22, -47.2) * mm});
            skLineSegment(sketch, "E739", {"start": v(-7.2, -48.22) * mm, "end": v(-3.22, -52.2) * mm});
            skLineSegment(sketch, "E740", {"start": v(-3.22, -52.2) * mm, "end": v(-7.2, -52.2) * mm});
            skLineSegment(sketch, "E741", {"start": v(-7.2, -52.2) * mm, "end": v(-7.2, -48.22) * mm});
            skLineSegment(sketch, "E742", {"start": v(-12.2, -53.23) * mm, "end": v(-8.22, -57.2) * mm});
            skLineSegment(sketch, "E743", {"start": v(-8.22, -57.2) * mm, "end": v(-12.2, -57.2) * mm});
            skLineSegment(sketch, "E744", {"start": v(-12.2, -57.2) * mm, "end": v(-12.2, -53.23) * mm});
            skLineSegment(sketch, "E745", {"start": v(-7.8, -56.78) * mm, "end": v(-11.78, -52.8) * mm});
            skLineSegment(sketch, "E746", {"start": v(-11.78, -52.8) * mm, "end": v(-7.8, -52.8) * mm});
            skLineSegment(sketch, "E747", {"start": v(-7.8, -52.8) * mm, "end": v(-7.8, -56.78) * mm});
            skLineSegment(sketch, "E748", {"start": v(-12.2, -58.22) * mm, "end": v(-8.22, -62.2) * mm});
            skLineSegment(sketch, "E749", {"start": v(-8.22, -62.2) * mm, "end": v(-12.2, -62.2) * mm});
            skLineSegment(sketch, "E750", {"start": v(-12.2, -62.2) * mm, "end": v(-12.2, -58.22) * mm});
            skLineSegment(sketch, "E751", {"start": v(-7.2, -57.2) * mm, "end": v(-7.2, -53.22) * mm});
            skLineSegment(sketch, "E752", {"start": v(-7.2, -53.22) * mm, "end": v(-3.22, -57.2) * mm});
            skLineSegment(sketch, "E753", {"start": v(-3.22, -57.2) * mm, "end": v(-7.2, -57.2) * mm});
            skLineSegment(sketch, "E754", {"start": v(-12.2, -52.2) * mm, "end": v(-12.2, -48.22) * mm});
            skLineSegment(sketch, "E755", {"start": v(-12.2, -48.22) * mm, "end": v(-8.22, -52.2) * mm});
            skLineSegment(sketch, "E756", {"start": v(-8.22, -52.2) * mm, "end": v(-12.2, -52.2) * mm});
            skLineSegment(sketch, "E757", {"start": v(-12.8, -56.78) * mm, "end": v(-16.78, -52.8) * mm});
            skLineSegment(sketch, "E758", {"start": v(-16.78, -52.8) * mm, "end": v(-12.8, -52.8) * mm});
            skLineSegment(sketch, "E759", {"start": v(-12.8, -52.8) * mm, "end": v(-12.8, -56.78) * mm});
            skLineSegment(sketch, "E760", {"start": v(-13.22, -57.2) * mm, "end": v(-17.2, -57.2) * mm});
            skLineSegment(sketch, "E761", {"start": v(-17.2, -57.2) * mm, "end": v(-17.2, -53.22) * mm});
            skLineSegment(sketch, "E762", {"start": v(-17.2, -53.22) * mm, "end": v(-13.22, -57.2) * mm});
            skLineSegment(sketch, "E763", {"start": v(-12.8, -61.78) * mm, "end": v(-16.78, -57.8) * mm});
            skLineSegment(sketch, "E764", {"start": v(-16.78, -57.8) * mm, "end": v(-12.8, -57.8) * mm});
            skLineSegment(sketch, "E765", {"start": v(-12.8, -57.8) * mm, "end": v(-12.8, -61.78) * mm});
            skLineSegment(sketch, "E766", {"start": v(-17.2, -58.22) * mm, "end": v(-13.22, -62.2) * mm});
            skLineSegment(sketch, "E767", {"start": v(-13.22, -62.2) * mm, "end": v(-17.2, -62.2) * mm});
            skLineSegment(sketch, "E768", {"start": v(-17.2, -62.2) * mm, "end": v(-17.2, -58.22) * mm});
            skLineSegment(sketch, "E769", {"start": v(-12.8, -62.8) * mm, "end": v(-12.8, -66.78) * mm});
            skLineSegment(sketch, "E770", {"start": v(-12.8, -66.78) * mm, "end": v(-16.78, -62.8) * mm});
            skLineSegment(sketch, "E771", {"start": v(-16.78, -62.8) * mm, "end": v(-12.8, -62.8) * mm});
            skLineSegment(sketch, "E772", {"start": v(-22.8, -71.78) * mm, "end": v(-26.78, -67.8) * mm});
            skLineSegment(sketch, "E773", {"start": v(-26.78, -67.8) * mm, "end": v(-22.8, -67.8) * mm});
            skLineSegment(sketch, "E774", {"start": v(-22.8, -67.8) * mm, "end": v(-22.8, -71.78) * mm});
            skLineSegment(sketch, "E775", {"start": v(-22.2, -63.22) * mm, "end": v(-18.22, -67.2) * mm});
            skLineSegment(sketch, "E776", {"start": v(-18.22, -67.2) * mm, "end": v(-22.2, -67.2) * mm});
            skLineSegment(sketch, "E777", {"start": v(-22.2, -67.2) * mm, "end": v(-22.2, -63.22) * mm});
            skLineSegment(sketch, "E778", {"start": v(-17.8, -66.78) * mm, "end": v(-21.78, -62.8) * mm});
            skLineSegment(sketch, "E779", {"start": v(-21.78, -62.8) * mm, "end": v(-17.8, -62.8) * mm});
            skLineSegment(sketch, "E780", {"start": v(-17.8, -62.8) * mm, "end": v(-17.8, -66.78) * mm});
            skLineSegment(sketch, "E781", {"start": v(-22.8, -66.78) * mm, "end": v(-26.78, -62.8) * mm});
            skLineSegment(sketch, "E782", {"start": v(-26.78, -62.8) * mm, "end": v(-22.8, -62.8) * mm});
            skLineSegment(sketch, "E783", {"start": v(-22.8, -62.8) * mm, "end": v(-22.8, -66.78) * mm});
            skLineSegment(sketch, "E784", {"start": v(-23.22, -67.2) * mm, "end": v(-27.2, -67.2) * mm});
            skLineSegment(sketch, "E785", {"start": v(-27.2, -67.2) * mm, "end": v(-27.2, -63.22) * mm});
            skLineSegment(sketch, "E786", {"start": v(-27.2, -63.22) * mm, "end": v(-23.22, -67.2) * mm});
            skLineSegment(sketch, "E787", {"start": v(-27.2, -68.22) * mm, "end": v(-23.22, -72.2) * mm});
            skLineSegment(sketch, "E788", {"start": v(-23.22, -72.2) * mm, "end": v(-27.2, -72.2) * mm});
            skLineSegment(sketch, "E789", {"start": v(-27.2, -72.2) * mm, "end": v(-27.2, -68.22) * mm});
            skLineSegment(sketch, "E790", {"start": v(-32.2, -73.22) * mm, "end": v(-28.23, -77.2) * mm});
            skLineSegment(sketch, "E791", {"start": v(-28.23, -77.2) * mm, "end": v(-32.2, -77.2) * mm});
            skLineSegment(sketch, "E792", {"start": v(-32.2, -77.2) * mm, "end": v(-32.2, -73.22) * mm});
            skLineSegment(sketch, "E793", {"start": v(-27.8, -76.78) * mm, "end": v(-31.78, -72.8) * mm});
            skLineSegment(sketch, "E794", {"start": v(-31.78, -72.8) * mm, "end": v(-27.8, -72.8) * mm});
            skLineSegment(sketch, "E795", {"start": v(-27.8, -72.8) * mm, "end": v(-27.8, -76.78) * mm});
            skLineSegment(sketch, "E796", {"start": v(-32.2, -78.22) * mm, "end": v(-28.22, -82.2) * mm});
            skLineSegment(sketch, "E797", {"start": v(-28.22, -82.2) * mm, "end": v(-32.2, -82.2) * mm});
            skLineSegment(sketch, "E798", {"start": v(-32.2, -82.2) * mm, "end": v(-32.2, -78.22) * mm});
            skLineSegment(sketch, "E799", {"start": v(-27.2, -77.2) * mm, "end": v(-27.2, -73.22) * mm});
            skLineSegment(sketch, "E800", {"start": v(-27.2, -73.22) * mm, "end": v(-23.22, -77.2) * mm});
            skLineSegment(sketch, "E801", {"start": v(-23.22, -77.2) * mm, "end": v(-27.2, -77.2) * mm});
            skLineSegment(sketch, "E802", {"start": v(-32.2, -72.2) * mm, "end": v(-32.2, -68.22) * mm});
            skLineSegment(sketch, "E803", {"start": v(-32.2, -68.22) * mm, "end": v(-28.22, -72.2) * mm});
            skLineSegment(sketch, "E804", {"start": v(-28.22, -72.2) * mm, "end": v(-32.2, -72.2) * mm});
            skLineSegment(sketch, "E805", {"start": v(-32.8, -76.78) * mm, "end": v(-36.78, -72.8) * mm});
            skLineSegment(sketch, "E806", {"start": v(-36.78, -72.8) * mm, "end": v(-32.8, -72.8) * mm});
            skLineSegment(sketch, "E807", {"start": v(-32.8, -72.8) * mm, "end": v(-32.8, -76.78) * mm});
            skLineSegment(sketch, "E808", {"start": v(-33.22, -77.2) * mm, "end": v(-37.2, -77.2) * mm});
            skLineSegment(sketch, "E809", {"start": v(-37.2, -77.2) * mm, "end": v(-37.2, -73.22) * mm});
            skLineSegment(sketch, "E810", {"start": v(-37.2, -73.22) * mm, "end": v(-33.22, -77.2) * mm});
            skLineSegment(sketch, "E811", {"start": v(-33.23, -87.2) * mm, "end": v(-37.2, -87.2) * mm});
            skLineSegment(sketch, "E812", {"start": v(-37.2, -87.2) * mm, "end": v(-37.2, -83.22) * mm});
            skLineSegment(sketch, "E813", {"start": v(-37.2, -83.22) * mm, "end": v(-33.23, -87.2) * mm});
            skLineSegment(sketch, "E814", {"start": v(-36.78, -82.8) * mm, "end": v(-32.8, -82.8) * mm});
            skLineSegment(sketch, "E815", {"start": v(-32.8, -82.8) * mm, "end": v(-32.8, -86.78) * mm});
            skLineSegment(sketch, "E816", {"start": v(-32.8, -86.78) * mm, "end": v(-36.78, -82.8) * mm});
            skLineSegment(sketch, "E817", {"start": v(-32.8, -81.78) * mm, "end": v(-36.78, -77.8) * mm});
            skLineSegment(sketch, "E818", {"start": v(-36.78, -77.8) * mm, "end": v(-32.8, -77.8) * mm});
            skLineSegment(sketch, "E819", {"start": v(-32.8, -77.8) * mm, "end": v(-32.8, -81.78) * mm});
            skLineSegment(sketch, "E820", {"start": v(-37.2, -78.22) * mm, "end": v(-33.22, -82.2) * mm});
            skLineSegment(sketch, "E821", {"start": v(-33.22, -82.2) * mm, "end": v(-37.2, -82.2) * mm});
            skLineSegment(sketch, "E822", {"start": v(-37.2, -82.2) * mm, "end": v(-37.2, -78.22) * mm});
            skLineSegment(sketch, "E823", {"start": v(-37.8, -82.8) * mm, "end": v(-37.8, -86.78) * mm});
            skLineSegment(sketch, "E824", {"start": v(-37.8, -86.78) * mm, "end": v(-41.78, -82.8) * mm});
            skLineSegment(sketch, "E825", {"start": v(-41.78, -82.8) * mm, "end": v(-37.8, -82.8) * mm});
            skLineSegment(sketch, "E826", {"start": v(-31.78, -77.8) * mm, "end": v(-27.8, -77.8) * mm});
            skLineSegment(sketch, "E827", {"start": v(-27.8, -77.8) * mm, "end": v(-27.8, -81.78) * mm});
            skLineSegment(sketch, "E828", {"start": v(-27.8, -81.78) * mm, "end": v(-31.78, -77.8) * mm});
            skLineSegment(sketch, "E829", {"start": v(-22.8, -77.8) * mm, "end": v(-22.8, -81.78) * mm});
            skLineSegment(sketch, "E830", {"start": v(-22.8, -81.78) * mm, "end": v(-26.78, -77.8) * mm});
            skLineSegment(sketch, "E831", {"start": v(-26.78, -77.8) * mm, "end": v(-22.8, -77.8) * mm});
            skLineSegment(sketch, "E832", {"start": v(-26.78, -72.8) * mm, "end": v(-22.8, -72.8) * mm});
            skLineSegment(sketch, "E833", {"start": v(-22.8, -72.8) * mm, "end": v(-22.8, -76.78) * mm});
            skLineSegment(sketch, "E834", {"start": v(-22.8, -76.78) * mm, "end": v(-26.78, -72.8) * mm});
            skLineSegment(sketch, "E835", {"start": v(-22.2, -72.2) * mm, "end": v(-22.2, -68.22) * mm});
            skLineSegment(sketch, "E836", {"start": v(-22.2, -68.22) * mm, "end": v(-18.22, -72.2) * mm});
            skLineSegment(sketch, "E837", {"start": v(-18.22, -72.2) * mm, "end": v(-20, -72.2) * mm});
            skLineSegment(sketch, "E838", {"start": v(-20, -72.2) * mm, "end": v(-22.2, -72.2) * mm});
            skLineSegment(sketch, "E839", {"start": v(-21.78, -67.8) * mm, "end": v(-17.8, -67.8) * mm});
            skLineSegment(sketch, "E840", {"start": v(-17.8, -67.8) * mm, "end": v(-17.8, -71.78) * mm});
            skLineSegment(sketch, "E841", {"start": v(-17.8, -71.78) * mm, "end": v(-21.78, -67.8) * mm});
            skLineSegment(sketch, "E842", {"start": v(-17.2, -67.2) * mm, "end": v(-17.2, -63.22) * mm});
            skLineSegment(sketch, "E843", {"start": v(-17.2, -63.22) * mm, "end": v(-13.22, -67.2) * mm});
            skLineSegment(sketch, "E844", {"start": v(-13.22, -67.2) * mm, "end": v(-15, -67.2) * mm});
            skLineSegment(sketch, "E845", {"start": v(-15, -67.2) * mm, "end": v(-17.2, -67.2) * mm});
            skLineSegment(sketch, "E846", {"start": v(-11.78, -57.8) * mm, "end": v(-7.8, -57.8) * mm});
            skLineSegment(sketch, "E847", {"start": v(-7.8, -57.8) * mm, "end": v(-7.8, -61.78) * mm});
            skLineSegment(sketch, "E848", {"start": v(-7.8, -61.78) * mm, "end": v(-11.78, -57.8) * mm});
            skLineSegment(sketch, "E849", {"start": v(-2.8, -57.8) * mm, "end": v(-2.8, -61.78) * mm});
            skLineSegment(sketch, "E850", {"start": v(-2.8, -61.78) * mm, "end": v(-6.78, -57.8) * mm});
            skLineSegment(sketch, "E851", {"start": v(-6.78, -57.8) * mm, "end": v(-2.8, -57.8) * mm});
            skLineSegment(sketch, "E852", {"start": v(-6.78, -52.8) * mm, "end": v(-2.8, -52.8) * mm});
            skLineSegment(sketch, "E853", {"start": v(-2.8, -52.8) * mm, "end": v(-2.8, -56.78) * mm});
            skLineSegment(sketch, "E854", {"start": v(-2.8, -56.78) * mm, "end": v(-6.78, -52.8) * mm});
            skLineSegment(sketch, "E855", {"start": v(-2.2, -52.2) * mm, "end": v(-2.2, -48.22) * mm});
            skLineSegment(sketch, "E856", {"start": v(-2.2, -48.22) * mm, "end": v(1.78, -52.2) * mm});
            skLineSegment(sketch, "E857", {"start": v(1.78, -52.2) * mm, "end": v(0, -52.2) * mm});
            skLineSegment(sketch, "E858", {"start": v(0, -52.2) * mm, "end": v(-2.2, -52.2) * mm});
            skLineSegment(sketch, "E859", {"start": v(2.8, -48.22) * mm, "end": v(6.78, -52.2) * mm});
            skLineSegment(sketch, "E860", {"start": v(6.78, -52.2) * mm, "end": v(2.8, -52.2) * mm});
            skLineSegment(sketch, "E861", {"start": v(2.8, -52.2) * mm, "end": v(2.8, -48.22) * mm});
            skLineSegment(sketch, "E862", {"start": v(3.22, -47.8) * mm, "end": v(5, -47.8) * mm});
            skLineSegment(sketch, "E863", {"start": v(5, -47.8) * mm, "end": v(7.2, -47.8) * mm});
            skLineSegment(sketch, "E864", {"start": v(7.2, -47.8) * mm, "end": v(7.2, -51.78) * mm});
            skLineSegment(sketch, "E865", {"start": v(7.2, -51.78) * mm, "end": v(3.22, -47.8) * mm});
            skLineSegment(sketch, "E866", {"start": v(8.22, -37.8) * mm, "end": v(12.2, -37.8) * mm});
            skLineSegment(sketch, "E867", {"start": v(12.2, -37.8) * mm, "end": v(12.2, -41.78) * mm});
            skLineSegment(sketch, "E868", {"start": v(12.2, -41.78) * mm, "end": v(8.22, -37.8) * mm});
            skLineSegment(sketch, "E869", {"start": v(13.22, -32.8) * mm, "end": v(17.2, -32.8) * mm});
            skLineSegment(sketch, "E870", {"start": v(17.2, -32.8) * mm, "end": v(17.2, -36.78) * mm});
            skLineSegment(sketch, "E871", {"start": v(17.2, -36.78) * mm, "end": v(13.22, -32.8) * mm});
            skLineSegment(sketch, "E872", {"start": v(17.8, -32.2) * mm, "end": v(17.8, -28.22) * mm});
            skLineSegment(sketch, "E873", {"start": v(17.8, -28.22) * mm, "end": v(21.78, -32.2) * mm});
            skLineSegment(sketch, "E874", {"start": v(21.78, -32.2) * mm, "end": v(17.8, -32.2) * mm});
            skLineSegment(sketch, "E875", {"start": v(17.8, -27.2) * mm, "end": v(17.8, -23.22) * mm});
            skLineSegment(sketch, "E876", {"start": v(17.8, -23.22) * mm, "end": v(21.78, -27.2) * mm});
            skLineSegment(sketch, "E877", {"start": v(21.78, -27.2) * mm, "end": v(17.8, -27.2) * mm});
            skLineSegment(sketch, "E878", {"start": v(17.8, -18.22) * mm, "end": v(21.78, -22.2) * mm});
            skLineSegment(sketch, "E879", {"start": v(21.78, -22.2) * mm, "end": v(17.8, -22.2) * mm});
            skLineSegment(sketch, "E880", {"start": v(17.8, -22.2) * mm, "end": v(17.8, -18.22) * mm});
            skLineSegment(sketch, "E881", {"start": v(17.8, -13.22) * mm, "end": v(21.78, -17.2) * mm});
            skLineSegment(sketch, "E882", {"start": v(21.78, -17.2) * mm, "end": v(17.8, -17.2) * mm});
            skLineSegment(sketch, "E883", {"start": v(17.8, -17.2) * mm, "end": v(17.8, -13.22) * mm});
            skLineSegment(sketch, "E884", {"start": v(17.8, -7.2) * mm, "end": v(17.8, -3.22) * mm});
            skLineSegment(sketch, "E885", {"start": v(17.8, -3.22) * mm, "end": v(21.78, -7.2) * mm});
            skLineSegment(sketch, "E886", {"start": v(21.78, -7.2) * mm, "end": v(17.8, -7.2) * mm});
            skLineSegment(sketch, "E887", {"start": v(17.8, 1.78) * mm, "end": v(21.78, -2.2) * mm});
            skLineSegment(sketch, "E888", {"start": v(21.78, -2.2) * mm, "end": v(17.8, -2.2) * mm});
            skLineSegment(sketch, "E889", {"start": v(17.8, -2.2) * mm, "end": v(17.8, 1.78) * mm});
            skLineSegment(sketch, "E890", {"start": v(18.22, 2.2) * mm, "end": v(22.2, 2.2) * mm});
            skLineSegment(sketch, "E891", {"start": v(22.2, 2.2) * mm, "end": v(22.2, -1.78) * mm});
            skLineSegment(sketch, "E892", {"start": v(22.2, -1.78) * mm, "end": v(18.22, 2.2) * mm});
            skLineSegment(sketch, "E893", {"start": v(22.8, 2.8) * mm, "end": v(22.8, 7.2) * mm});
            skLineSegment(sketch, "E894", {"start": v(22.8, 7.2) * mm, "end": v(27.2, 7.2) * mm});
            skLineSegment(sketch, "E895", {"start": v(27.2, 7.2) * mm, "end": v(27.2, 2.8) * mm});
            skLineSegment(sketch, "E896", {"start": v(27.2, 2.8) * mm, "end": v(22.8, 2.8) * mm});
            skLineSegment(sketch, "E897", {"start": v(27.8, 11.78) * mm, "end": v(31.78, 7.8) * mm});
            skLineSegment(sketch, "E898", {"start": v(31.78, 7.8) * mm, "end": v(27.8, 7.8) * mm});
            skLineSegment(sketch, "E899", {"start": v(27.8, 7.8) * mm, "end": v(27.8, 11.78) * mm});
            skLineSegment(sketch, "E900", {"start": v(32.2, 8.22) * mm, "end": v(28.22, 12.2) * mm});
            skLineSegment(sketch, "E901", {"start": v(28.22, 12.2) * mm, "end": v(30, 12.2) * mm});
            skLineSegment(sketch, "E902", {"start": v(30, 12.2) * mm, "end": v(32.2, 12.2) * mm});
            skLineSegment(sketch, "E903", {"start": v(32.2, 12.2) * mm, "end": v(32.2, 8.22) * mm});
            skLineSegment(sketch, "E904", {"start": v(32.8, 16.78) * mm, "end": v(36.78, 12.8) * mm});
            skLineSegment(sketch, "E905", {"start": v(36.78, 12.8) * mm, "end": v(32.8, 12.8) * mm});
            skLineSegment(sketch, "E906", {"start": v(32.8, 12.8) * mm, "end": v(32.8, 16.78) * mm});
            skLineSegment(sketch, "E907", {"start": v(37.8, 16.78) * mm, "end": v(41.78, 12.8) * mm});
            skLineSegment(sketch, "E908", {"start": v(41.78, 12.8) * mm, "end": v(37.8, 12.8) * mm});
            skLineSegment(sketch, "E909", {"start": v(37.8, 12.8) * mm, "end": v(37.8, 16.78) * mm});
            skLineSegment(sketch, "E910", {"start": v(42.8, 21.78) * mm, "end": v(46.78, 17.8) * mm});
            skLineSegment(sketch, "E911", {"start": v(46.78, 17.8) * mm, "end": v(42.8, 17.8) * mm});
            skLineSegment(sketch, "E912", {"start": v(42.8, 17.8) * mm, "end": v(42.8, 21.78) * mm});
            skLineSegment(sketch, "E913", {"start": v(47.2, 23.22) * mm, "end": v(43.22, 27.2) * mm});
            skLineSegment(sketch, "E914", {"start": v(43.22, 27.2) * mm, "end": v(47.2, 27.2) * mm});
            skLineSegment(sketch, "E915", {"start": v(47.2, 27.2) * mm, "end": v(47.2, 23.22) * mm});
            skLineSegment(sketch, "E916", {"start": v(52.2, 27.2) * mm, "end": v(52.2, 23.22) * mm});
            skLineSegment(sketch, "E917", {"start": v(52.2, 23.22) * mm, "end": v(48.22, 27.2) * mm});
            skLineSegment(sketch, "E918", {"start": v(48.22, 27.2) * mm, "end": v(52.2, 27.2) * mm});
            skLineSegment(sketch, "E919", {"start": v(52.2, 33.22) * mm, "end": v(48.22, 37.2) * mm});
            skLineSegment(sketch, "E920", {"start": v(48.22, 37.2) * mm, "end": v(52.2, 37.2) * mm});
            skLineSegment(sketch, "E921", {"start": v(52.2, 37.2) * mm, "end": v(52.2, 33.22) * mm});
            skLineSegment(sketch, "E922", {"start": v(52.2, 28.22) * mm, "end": v(48.22, 32.2) * mm});
            skLineSegment(sketch, "E923", {"start": v(48.22, 32.2) * mm, "end": v(52.2, 32.2) * mm});
            skLineSegment(sketch, "E924", {"start": v(52.2, 32.2) * mm, "end": v(52.2, 28.22) * mm});
            skLineSegment(sketch, "E925", {"start": v(42.8, 26.78) * mm, "end": v(46.78, 22.8) * mm});
            skLineSegment(sketch, "E926", {"start": v(46.78, 22.8) * mm, "end": v(42.8, 22.8) * mm});
            skLineSegment(sketch, "E927", {"start": v(42.8, 22.8) * mm, "end": v(42.8, 26.78) * mm});
            skLineSegment(sketch, "E928", {"start": v(47.8, 26.78) * mm, "end": v(51.78, 22.8) * mm});
            skLineSegment(sketch, "E929", {"start": v(51.78, 22.8) * mm, "end": v(47.8, 22.8) * mm});
            skLineSegment(sketch, "E930", {"start": v(47.8, 22.8) * mm, "end": v(47.8, 26.78) * mm});
            skLineSegment(sketch, "E931", {"start": v(52.8, 31.78) * mm, "end": v(56.78, 27.8) * mm});
            skLineSegment(sketch, "E932", {"start": v(56.78, 27.8) * mm, "end": v(52.8, 27.8) * mm});
            skLineSegment(sketch, "E933", {"start": v(52.8, 27.8) * mm, "end": v(52.8, 31.78) * mm});
            skLineSegment(sketch, "E934", {"start": v(72.2, 53.22) * mm, "end": v(68.22, 57.2) * mm});
            skLineSegment(sketch, "E935", {"start": v(68.22, 57.2) * mm, "end": v(72.2, 57.2) * mm});
            skLineSegment(sketch, "E936", {"start": v(72.2, 57.2) * mm, "end": v(72.2, 53.22) * mm});
            skLineSegment(sketch, "E937", {"start": v(72.2, 47.2) * mm, "end": v(72.2, 43.22) * mm});
            skLineSegment(sketch, "E938", {"start": v(72.2, 43.22) * mm, "end": v(68.22, 47.2) * mm});
            skLineSegment(sketch, "E939", {"start": v(68.22, 47.2) * mm, "end": v(72.2, 47.2) * mm});
            skLineSegment(sketch, "E940", {"start": v(67.2, 43.22) * mm, "end": v(63.22, 47.2) * mm});
            skLineSegment(sketch, "E941", {"start": v(63.22, 47.2) * mm, "end": v(67.2, 47.2) * mm});
            skLineSegment(sketch, "E942", {"start": v(67.2, 47.2) * mm, "end": v(67.2, 43.22) * mm});
            skLineSegment(sketch, "E943", {"start": v(57.2, 37.2) * mm, "end": v(57.2, 33.22) * mm});
            skLineSegment(sketch, "E944", {"start": v(57.2, 33.22) * mm, "end": v(53.22, 37.2) * mm});
            skLineSegment(sketch, "E945", {"start": v(53.22, 37.2) * mm, "end": v(57.2, 37.2) * mm});
            skLineSegment(sketch, "E946", {"start": v(62.2, 38.22) * mm, "end": v(58.22, 42.2) * mm});
            skLineSegment(sketch, "E947", {"start": v(58.22, 42.2) * mm, "end": v(62.2, 42.2) * mm});
            skLineSegment(sketch, "E948", {"start": v(62.2, 42.2) * mm, "end": v(62.2, 38.22) * mm});
            skLineSegment(sketch, "E949", {"start": v(62.2, 37.2) * mm, "end": v(62.2, 33.22) * mm});
            skLineSegment(sketch, "E950", {"start": v(62.2, 33.22) * mm, "end": v(58.22, 37.2) * mm});
            skLineSegment(sketch, "E951", {"start": v(58.22, 37.2) * mm, "end": v(62.2, 37.2) * mm});
            skLineSegment(sketch, "E952", {"start": v(52.8, 36.78) * mm, "end": v(56.78, 32.8) * mm});
            skLineSegment(sketch, "E953", {"start": v(56.78, 32.8) * mm, "end": v(52.8, 32.8) * mm});
            skLineSegment(sketch, "E954", {"start": v(52.8, 32.8) * mm, "end": v(52.8, 36.78) * mm});
            skLineSegment(sketch, "E955", {"start": v(57.8, 36.78) * mm, "end": v(61.78, 32.8) * mm});
            skLineSegment(sketch, "E956", {"start": v(61.78, 32.8) * mm, "end": v(57.8, 32.8) * mm});
            skLineSegment(sketch, "E957", {"start": v(57.8, 32.8) * mm, "end": v(57.8, 36.78) * mm});
            skLineSegment(sketch, "E958", {"start": v(62.8, 41.78) * mm, "end": v(66.78, 37.8) * mm});
            skLineSegment(sketch, "E959", {"start": v(66.78, 37.8) * mm, "end": v(62.8, 37.8) * mm});
            skLineSegment(sketch, "E960", {"start": v(62.8, 37.8) * mm, "end": v(62.8, 41.78) * mm});
            skLineSegment(sketch, "E961", {"start": v(62.8, 46.78) * mm, "end": v(66.78, 42.8) * mm});
            skLineSegment(sketch, "E962", {"start": v(66.78, 42.8) * mm, "end": v(62.8, 42.8) * mm});
            skLineSegment(sketch, "E963", {"start": v(62.8, 42.8) * mm, "end": v(62.8, 46.78) * mm});
            skLineSegment(sketch, "E964", {"start": v(67.8, 46.78) * mm, "end": v(71.78, 42.8) * mm});
            skLineSegment(sketch, "E965", {"start": v(71.78, 42.8) * mm, "end": v(67.8, 42.8) * mm});
            skLineSegment(sketch, "E966", {"start": v(67.8, 42.8) * mm, "end": v(67.8, 46.78) * mm});
            skLineSegment(sketch, "E967", {"start": v(72.2, 48.22) * mm, "end": v(68.22, 52.2) * mm});
            skLineSegment(sketch, "E968", {"start": v(68.22, 52.2) * mm, "end": v(72.2, 52.2) * mm});
            skLineSegment(sketch, "E969", {"start": v(72.2, 52.2) * mm, "end": v(72.2, 48.22) * mm});
            skLineSegment(sketch, "E970", {"start": v(78.22, 57.8) * mm, "end": v(82.2, 61.78) * mm});
            skLineSegment(sketch, "E971", {"start": v(82.2, 61.78) * mm, "end": v(82.2, 57.8) * mm});
            skLineSegment(sketch, "E972", {"start": v(82.2, 57.8) * mm, "end": v(78.22, 57.8) * mm});
            skLineSegment(sketch, "E973", {"start": v(77.8, 58.22) * mm, "end": v(77.8, 62.2) * mm});
            skLineSegment(sketch, "E974", {"start": v(77.8, 62.2) * mm, "end": v(81.78, 62.2) * mm});
            skLineSegment(sketch, "E975", {"start": v(81.78, 62.2) * mm, "end": v(77.8, 58.22) * mm});
            skLineSegment(sketch, "E976", {"start": v(72.8, 56.78) * mm, "end": v(76.78, 52.8) * mm});
            skLineSegment(sketch, "E977", {"start": v(76.78, 52.8) * mm, "end": v(72.8, 52.8) * mm});
            skLineSegment(sketch, "E978", {"start": v(72.8, 52.8) * mm, "end": v(72.8, 56.78) * mm});
            skLineSegment(sketch, "E979", {"start": v(73.22, 57.2) * mm, "end": v(77.2, 57.2) * mm});
            skLineSegment(sketch, "E980", {"start": v(77.2, 57.2) * mm, "end": v(77.2, 53.22) * mm});
            skLineSegment(sketch, "E981", {"start": v(77.2, 53.22) * mm, "end": v(73.22, 57.2) * mm});
            skLineSegment(sketch, "E982", {"start": v(82.8, 67.2) * mm, "end": v(86.78, 67.2) * mm});
            skLineSegment(sketch, "E983", {"start": v(86.78, 67.2) * mm, "end": v(82.8, 63.22) * mm});
            skLineSegment(sketch, "E984", {"start": v(82.8, 63.22) * mm, "end": v(82.8, 67.2) * mm});
            skLineSegment(sketch, "E985", {"start": v(83.22, 67.8) * mm, "end": v(87.2, 71.78) * mm});
            skLineSegment(sketch, "E986", {"start": v(87.2, 71.78) * mm, "end": v(87.2, 67.8) * mm});
            skLineSegment(sketch, "E987", {"start": v(87.2, 67.8) * mm, "end": v(83.22, 67.8) * mm});
            skLineSegment(sketch, "E988", {"start": v(82.2, 62.8) * mm, "end": v(78.22, 62.8) * mm});
            skLineSegment(sketch, "E989", {"start": v(78.22, 62.8) * mm, "end": v(82.2, 66.78) * mm});
            skLineSegment(sketch, "E990", {"start": v(82.2, 66.78) * mm, "end": v(82.2, 62.8) * mm});
            skLineSegment(sketch, "E991", {"start": v(71.78, 52.8) * mm, "end": v(67.8, 52.8) * mm});
            skLineSegment(sketch, "E992", {"start": v(67.8, 52.8) * mm, "end": v(67.8, 56.78) * mm});
            skLineSegment(sketch, "E993", {"start": v(67.8, 56.78) * mm, "end": v(71.78, 52.8) * mm});
            skLineSegment(sketch, "E994", {"start": v(71.78, 47.8) * mm, "end": v(67.8, 47.8) * mm});
            skLineSegment(sketch, "E995", {"start": v(67.8, 47.8) * mm, "end": v(67.8, 51.78) * mm});
            skLineSegment(sketch, "E996", {"start": v(67.8, 51.78) * mm, "end": v(71.78, 47.8) * mm});
            skLineSegment(sketch, "E997", {"start": v(57.8, 41.78) * mm, "end": v(61.78, 37.8) * mm});
            skLineSegment(sketch, "E998", {"start": v(61.78, 37.8) * mm, "end": v(57.8, 37.8) * mm});
            skLineSegment(sketch, "E999", {"start": v(57.8, 37.8) * mm, "end": v(57.8, 41.78) * mm});
            skLineSegment(sketch, "E1000", {"start": v(51.78, 32.8) * mm, "end": v(47.8, 32.8) * mm});
            skLineSegment(sketch, "E1001", {"start": v(47.8, 32.8) * mm, "end": v(47.8, 36.78) * mm});
            skLineSegment(sketch, "E1002", {"start": v(47.8, 36.78) * mm, "end": v(51.78, 32.8) * mm});
            skLineSegment(sketch, "E1003", {"start": v(51.78, 27.8) * mm, "end": v(47.8, 27.8) * mm});
            skLineSegment(sketch, "E1004", {"start": v(47.8, 27.8) * mm, "end": v(47.8, 31.78) * mm});
            skLineSegment(sketch, "E1005", {"start": v(47.8, 31.78) * mm, "end": v(51.78, 27.8) * mm});
            skLineSegment(sketch, "E1006", {"start": v(37.8, 26.78) * mm, "end": v(41.78, 22.8) * mm});
            skLineSegment(sketch, "E1007", {"start": v(41.78, 22.8) * mm, "end": v(37.8, 22.8) * mm});
            skLineSegment(sketch, "E1008", {"start": v(37.8, 22.8) * mm, "end": v(37.8, 26.78) * mm});
            skLineSegment(sketch, "E1009", {"start": v(37.2, 18.22) * mm, "end": v(33.22, 22.2) * mm});
            skLineSegment(sketch, "E1010", {"start": v(33.22, 22.2) * mm, "end": v(37.2, 22.2) * mm});
            skLineSegment(sketch, "E1011", {"start": v(37.2, 22.2) * mm, "end": v(37.2, 18.22) * mm});
            skLineSegment(sketch, "E1012", {"start": v(32.2, 18.22) * mm, "end": v(28.22, 22.2) * mm});
            skLineSegment(sketch, "E1013", {"start": v(28.22, 22.2) * mm, "end": v(32.2, 22.2) * mm});
            skLineSegment(sketch, "E1014", {"start": v(32.2, 22.2) * mm, "end": v(32.2, 18.22) * mm});
            skLineSegment(sketch, "E1015", {"start": v(22.8, 27.8) * mm, "end": v(22.8, 31.78) * mm});
            skLineSegment(sketch, "E1016", {"start": v(22.8, 31.78) * mm, "end": v(26.78, 27.8) * mm});
            skLineSegment(sketch, "E1017", {"start": v(26.78, 27.8) * mm, "end": v(22.8, 27.8) * mm});
            skLineSegment(sketch, "E1018", {"start": v(22.8, 36.78) * mm, "end": v(26.78, 32.8) * mm});
            skLineSegment(sketch, "E1019", {"start": v(26.78, 32.8) * mm, "end": v(22.8, 32.8) * mm});
            skLineSegment(sketch, "E1020", {"start": v(22.8, 32.8) * mm, "end": v(22.8, 36.78) * mm});
            skLineSegment(sketch, "E1021", {"start": v(23.22, 37.2) * mm, "end": v(27.2, 37.2) * mm});
            skLineSegment(sketch, "E1022", {"start": v(27.2, 37.2) * mm, "end": v(27.2, 33.22) * mm});
            skLineSegment(sketch, "E1023", {"start": v(27.2, 33.22) * mm, "end": v(23.22, 37.2) * mm});
            skLineSegment(sketch, "E1024", {"start": v(28.22, 52.2) * mm, "end": v(32.2, 52.2) * mm});
            skLineSegment(sketch, "E1025", {"start": v(32.2, 52.2) * mm, "end": v(32.2, 48.22) * mm});
            skLineSegment(sketch, "E1026", {"start": v(32.2, 48.22) * mm, "end": v(28.22, 52.2) * mm});
            skLineSegment(sketch, "E1027", {"start": v(37.2, 52.2) * mm, "end": v(37.2, 48.22) * mm});
            skLineSegment(sketch, "E1028", {"start": v(37.2, 48.22) * mm, "end": v(33.22, 52.2) * mm});
            skLineSegment(sketch, "E1029", {"start": v(33.22, 52.2) * mm, "end": v(37.2, 52.2) * mm});
            skLineSegment(sketch, "E1030", {"start": v(38.22, 62.2) * mm, "end": v(42.2, 62.2) * mm});
            skLineSegment(sketch, "E1031", {"start": v(42.2, 62.2) * mm, "end": v(42.2, 58.22) * mm});
            skLineSegment(sketch, "E1032", {"start": v(42.2, 58.22) * mm, "end": v(38.22, 62.2) * mm});
            skLineSegment(sketch, "E1033", {"start": v(48.22, 72.2) * mm, "end": v(52.2, 72.2) * mm});
            skLineSegment(sketch, "E1034", {"start": v(52.2, 72.2) * mm, "end": v(52.2, 68.22) * mm});
            skLineSegment(sketch, "E1035", {"start": v(52.2, 68.22) * mm, "end": v(48.22, 72.2) * mm});
            skLineSegment(sketch, "E1036", {"start": v(57.2, 72.2) * mm, "end": v(57.2, 68.22) * mm});
            skLineSegment(sketch, "E1037", {"start": v(57.2, 68.22) * mm, "end": v(53.22, 72.2) * mm});
            skLineSegment(sketch, "E1038", {"start": v(53.22, 72.2) * mm, "end": v(57.2, 72.2) * mm});
            skLineSegment(sketch, "E1039", {"start": v(62.8, 82.2) * mm, "end": v(66.78, 82.2) * mm});
            skLineSegment(sketch, "E1040", {"start": v(66.78, 82.2) * mm, "end": v(62.8, 78.22) * mm});
            skLineSegment(sketch, "E1041", {"start": v(62.8, 78.22) * mm, "end": v(62.8, 82.2) * mm});
            skLineSegment(sketch, "E1042", {"start": v(67.8, 87.2) * mm, "end": v(71.78, 87.2) * mm});
            skLineSegment(sketch, "E1043", {"start": v(71.78, 87.2) * mm, "end": v(67.8, 83.22) * mm});
            skLineSegment(sketch, "E1044", {"start": v(67.8, 83.22) * mm, "end": v(67.8, 87.2) * mm});
            skLineSegment(sketch, "E1045", {"start": v(67.2, 82.8) * mm, "end": v(63.22, 82.8) * mm});
            skLineSegment(sketch, "E1046", {"start": v(63.22, 82.8) * mm, "end": v(67.2, 86.78) * mm});
            skLineSegment(sketch, "E1047", {"start": v(67.2, 86.78) * mm, "end": v(67.2, 82.8) * mm});
            skLineSegment(sketch, "E1048", {"start": v(58.22, 82.8) * mm, "end": v(62.2, 86.78) * mm});
            skLineSegment(sketch, "E1049", {"start": v(62.2, 86.78) * mm, "end": v(62.2, 82.8) * mm});
            skLineSegment(sketch, "E1050", {"start": v(62.2, 82.8) * mm, "end": v(58.22, 82.8) * mm});
            skLineSegment(sketch, "E1051", {"start": v(51.78, 72.8) * mm, "end": v(47.8, 72.8) * mm});
            skLineSegment(sketch, "E1052", {"start": v(47.8, 72.8) * mm, "end": v(47.8, 76.78) * mm});
            skLineSegment(sketch, "E1053", {"start": v(47.8, 76.78) * mm, "end": v(51.78, 72.8) * mm});
            skLineSegment(sketch, "E1054", {"start": v(42.8, 71.78) * mm, "end": v(46.78, 67.8) * mm});
            skLineSegment(sketch, "E1055", {"start": v(46.78, 67.8) * mm, "end": v(42.8, 67.8) * mm});
            skLineSegment(sketch, "E1056", {"start": v(42.8, 67.8) * mm, "end": v(42.8, 71.78) * mm});
            skLineSegment(sketch, "E1057", {"start": v(42.2, 63.22) * mm, "end": v(38.22, 67.2) * mm});
            skLineSegment(sketch, "E1058", {"start": v(38.22, 67.2) * mm, "end": v(42.2, 67.2) * mm});
            skLineSegment(sketch, "E1059", {"start": v(42.2, 67.2) * mm, "end": v(42.2, 63.22) * mm});
            skLineSegment(sketch, "E1060", {"start": v(41.78, 62.8) * mm, "end": v(37.8, 62.8) * mm});
            skLineSegment(sketch, "E1061", {"start": v(37.8, 62.8) * mm, "end": v(37.8, 66.78) * mm});
            skLineSegment(sketch, "E1062", {"start": v(37.8, 66.78) * mm, "end": v(41.78, 62.8) * mm});
            skLineSegment(sketch, "E1063", {"start": v(32.8, 62.8) * mm, "end": v(32.8, 66.78) * mm});
            skLineSegment(sketch, "E1064", {"start": v(32.8, 66.78) * mm, "end": v(36.78, 62.8) * mm});
            skLineSegment(sketch, "E1065", {"start": v(36.78, 62.8) * mm, "end": v(32.8, 62.8) * mm});
            skLineSegment(sketch, "E1066", {"start": v(36.78, 57.8) * mm, "end": v(32.8, 57.8) * mm});
            skLineSegment(sketch, "E1067", {"start": v(32.8, 57.8) * mm, "end": v(32.8, 61.78) * mm});
            skLineSegment(sketch, "E1068", {"start": v(32.8, 61.78) * mm, "end": v(36.78, 57.8) * mm});
            skLineSegment(sketch, "E1069", {"start": v(31.78, 52.8) * mm, "end": v(27.8, 52.8) * mm});
            skLineSegment(sketch, "E1070", {"start": v(27.8, 52.8) * mm, "end": v(27.8, 56.78) * mm});
            skLineSegment(sketch, "E1071", {"start": v(27.8, 56.78) * mm, "end": v(31.78, 52.8) * mm});
            skLineSegment(sketch, "E1072", {"start": v(22.8, 52.8) * mm, "end": v(22.8, 56.78) * mm});
            skLineSegment(sketch, "E1073", {"start": v(22.8, 56.78) * mm, "end": v(26.78, 52.8) * mm});
            skLineSegment(sketch, "E1074", {"start": v(26.78, 52.8) * mm, "end": v(22.8, 52.8) * mm});
            skLineSegment(sketch, "E1075", {"start": v(22.8, 51.78) * mm, "end": v(26.78, 47.8) * mm});
            skLineSegment(sketch, "E1076", {"start": v(26.78, 47.8) * mm, "end": v(22.8, 47.8) * mm});
            skLineSegment(sketch, "E1077", {"start": v(22.8, 47.8) * mm, "end": v(22.8, 51.78) * mm});
            skLineSegment(sketch, "E1078", {"start": v(17.8, 46.78) * mm, "end": v(21.78, 42.8) * mm});
            skLineSegment(sketch, "E1079", {"start": v(21.78, 42.8) * mm, "end": v(17.8, 42.8) * mm});
            skLineSegment(sketch, "E1080", {"start": v(17.8, 42.8) * mm, "end": v(17.8, 46.78) * mm});
            skLineSegment(sketch, "E1081", {"start": v(12.8, 41.78) * mm, "end": v(16.78, 37.8) * mm});
            skLineSegment(sketch, "E1082", {"start": v(16.78, 37.8) * mm, "end": v(12.8, 37.8) * mm});
            skLineSegment(sketch, "E1083", {"start": v(12.8, 37.8) * mm, "end": v(12.8, 41.78) * mm});
            skLineSegment(sketch, "E1084", {"start": v(7.8, 36.78) * mm, "end": v(11.78, 32.8) * mm});
            skLineSegment(sketch, "E1085", {"start": v(11.78, 32.8) * mm, "end": v(7.8, 32.8) * mm});
            skLineSegment(sketch, "E1086", {"start": v(7.8, 32.8) * mm, "end": v(7.8, 36.78) * mm});
            skLineSegment(sketch, "E1087", {"start": v(5, 32.2) * mm, "end": v(7.2, 32.2) * mm});
            skLineSegment(sketch, "E1088", {"start": v(7.2, 32.2) * mm, "end": v(7.2, 28.22) * mm});
            skLineSegment(sketch, "E1089", {"start": v(7.2, 28.22) * mm, "end": v(3.22, 32.2) * mm});
            skLineSegment(sketch, "E1090", {"start": v(3.22, 32.2) * mm, "end": v(5, 32.2) * mm});
            skLineSegment(sketch, "E1091", {"start": v(2.2, 18.22) * mm, "end": v(-1.78, 22.2) * mm});
            skLineSegment(sketch, "E1092", {"start": v(-1.78, 22.2) * mm, "end": v(2.2, 22.2) * mm});
            skLineSegment(sketch, "E1093", {"start": v(2.2, 22.2) * mm, "end": v(2.2, 18.22) * mm});
            skLineSegment(sketch, "E1094", {"start": v(-2.8, 20) * mm, "end": v(-2.8, 18.22) * mm});
            skLineSegment(sketch, "E1095", {"start": v(-2.8, 18.22) * mm, "end": v(-6.78, 22.2) * mm});
            skLineSegment(sketch, "E1096", {"start": v(-6.78, 22.2) * mm, "end": v(-2.8, 22.2) * mm});
            skLineSegment(sketch, "E1097", {"start": v(-2.8, 22.2) * mm, "end": v(-2.8, 20) * mm});
            skLineSegment(sketch, "E1098", {"start": v(-7.8, 18.22) * mm, "end": v(-11.78, 22.2) * mm});
            skLineSegment(sketch, "E1099", {"start": v(-11.78, 22.2) * mm, "end": v(-7.8, 22.2) * mm});
            skLineSegment(sketch, "E1100", {"start": v(-7.8, 22.2) * mm, "end": v(-7.8, 18.22) * mm});
            skLineSegment(sketch, "E1101", {"start": v(-32.8, 13.22) * mm, "end": v(-36.78, 17.2) * mm});
            skLineSegment(sketch, "E1102", {"start": v(-36.78, 17.2) * mm, "end": v(-32.8, 17.2) * mm});
            skLineSegment(sketch, "E1103", {"start": v(-32.8, 17.2) * mm, "end": v(-32.8, 13.22) * mm});
            skLineSegment(sketch, "E1104", {"start": v(-42.2, 11.78) * mm, "end": v(-38.22, 7.8) * mm});
            skLineSegment(sketch, "E1105", {"start": v(-38.22, 7.8) * mm, "end": v(-42.2, 7.8) * mm});
            skLineSegment(sketch, "E1106", {"start": v(-42.2, 7.8) * mm, "end": v(-42.2, 11.78) * mm});
            skLineSegment(sketch, "E1107", {"start": v(-52.2, 2.8) * mm, "end": v(-52.2, 6.78) * mm});
            skLineSegment(sketch, "E1108", {"start": v(-52.2, 6.78) * mm, "end": v(-48.22, 2.8) * mm});
            skLineSegment(sketch, "E1109", {"start": v(-48.22, 2.8) * mm, "end": v(-52.2, 2.8) * mm});
            skLineSegment(sketch, "E1110", {"start": v(-53.22, -2.2) * mm, "end": v(-57.2, -2.2) * mm});
            skLineSegment(sketch, "E1111", {"start": v(-57.2, -2.2) * mm, "end": v(-57.2, 1.78) * mm});
            skLineSegment(sketch, "E1112", {"start": v(-57.2, 1.78) * mm, "end": v(-53.22, -2.2) * mm});
            skLineSegment(sketch, "E1113", {"start": v(-58.22, -7.2) * mm, "end": v(-62.2, -7.2) * mm});
            skLineSegment(sketch, "E1114", {"start": v(-62.2, -7.2) * mm, "end": v(-62.2, -3.22) * mm});
            skLineSegment(sketch, "E1115", {"start": v(-62.2, -3.22) * mm, "end": v(-58.22, -7.2) * mm});
            skLineSegment(sketch, "E1116", {"start": v(-72.2, -13.22) * mm, "end": v(-68.22, -17.2) * mm});
            skLineSegment(sketch, "E1117", {"start": v(-68.22, -17.2) * mm, "end": v(-72.2, -17.2) * mm});
            skLineSegment(sketch, "E1118", {"start": v(-72.2, -17.2) * mm, "end": v(-72.2, -13.22) * mm});
            skLineSegment(sketch, "E1119", {"start": v(-68.22, -22.2) * mm, "end": v(-72.2, -22.2) * mm});
            skLineSegment(sketch, "E1120", {"start": v(-72.2, -22.2) * mm, "end": v(-72.2, -18.22) * mm});
            skLineSegment(sketch, "E1121", {"start": v(-72.2, -18.22) * mm, "end": v(-68.22, -22.2) * mm});
            skLineSegment(sketch, "E1122", {"start": v(-87.2, -33.23) * mm, "end": v(-83.22, -37.2) * mm});
            skLineSegment(sketch, "E1123", {"start": v(-83.22, -37.2) * mm, "end": v(-87.2, -37.2) * mm});
            skLineSegment(sketch, "E1124", {"start": v(-87.2, -37.2) * mm, "end": v(-87.2, -33.23) * mm});
            skLineSegment(sketch, "E1125", {"start": v(-82.2, -33.22) * mm, "end": v(-78.22, -37.2) * mm});
            skLineSegment(sketch, "E1126", {"start": v(-78.22, -37.2) * mm, "end": v(-82.2, -37.2) * mm});
            skLineSegment(sketch, "E1127", {"start": v(-82.2, -37.2) * mm, "end": v(-82.2, -33.22) * mm});
            skLineSegment(sketch, "E1128", {"start": v(-77.2, -37.2) * mm, "end": v(-77.2, -33.22) * mm});
            skLineSegment(sketch, "E1129", {"start": v(-77.2, -33.22) * mm, "end": v(-73.22, -37.2) * mm});
            skLineSegment(sketch, "E1130", {"start": v(-73.22, -37.2) * mm, "end": v(-77.2, -37.2) * mm});
            skLineSegment(sketch, "E1131", {"start": v(-72.8, -32.8) * mm, "end": v(-72.8, -36.78) * mm});
            skLineSegment(sketch, "E1132", {"start": v(-72.8, -36.78) * mm, "end": v(-76.78, -32.8) * mm});
            skLineSegment(sketch, "E1133", {"start": v(-76.78, -32.8) * mm, "end": v(-72.8, -32.8) * mm});
            skLineSegment(sketch, "E1134", {"start": v(-72.2, -28.22) * mm, "end": v(-68.22, -32.2) * mm});
            skLineSegment(sketch, "E1135", {"start": v(-68.22, -32.2) * mm, "end": v(-72.2, -32.2) * mm});
            skLineSegment(sketch, "E1136", {"start": v(-72.2, -32.2) * mm, "end": v(-72.2, -28.22) * mm});
            skLineSegment(sketch, "E1137", {"start": v(-67.8, -31.78) * mm, "end": v(-71.78, -27.8) * mm});
            skLineSegment(sketch, "E1138", {"start": v(-71.78, -27.8) * mm, "end": v(-67.8, -27.8) * mm});
            skLineSegment(sketch, "E1139", {"start": v(-67.8, -27.8) * mm, "end": v(-67.8, -31.78) * mm});
            skLineSegment(sketch, "E1140", {"start": v(-67.2, -23.22) * mm, "end": v(-63.22, -27.2) * mm});
            skLineSegment(sketch, "E1141", {"start": v(-63.22, -27.2) * mm, "end": v(-67.2, -27.2) * mm});
            skLineSegment(sketch, "E1142", {"start": v(-67.2, -27.2) * mm, "end": v(-67.2, -23.22) * mm});
            skLineSegment(sketch, "E1143", {"start": v(-62.2, -18.22) * mm, "end": v(-58.22, -22.2) * mm});
            skLineSegment(sketch, "E1144", {"start": v(-58.22, -22.2) * mm, "end": v(-62.2, -22.2) * mm});
            skLineSegment(sketch, "E1145", {"start": v(-62.2, -22.2) * mm, "end": v(-62.2, -18.22) * mm});
            skLineSegment(sketch, "E1146", {"start": v(-61.78, -17.8) * mm, "end": v(-57.8, -17.8) * mm});
            skLineSegment(sketch, "E1147", {"start": v(-57.8, -17.8) * mm, "end": v(-57.8, -21.78) * mm});
            skLineSegment(sketch, "E1148", {"start": v(-57.8, -21.78) * mm, "end": v(-61.78, -17.8) * mm});
            skLineSegment(sketch, "E1149", {"start": v(-57.8, -16.78) * mm, "end": v(-61.78, -12.8) * mm});
            skLineSegment(sketch, "E1150", {"start": v(-61.78, -12.8) * mm, "end": v(-57.8, -12.8) * mm});
            skLineSegment(sketch, "E1151", {"start": v(-57.8, -12.8) * mm, "end": v(-57.8, -16.78) * mm});
            skLineSegment(sketch, "E1152", {"start": v(-52.8, -12.8) * mm, "end": v(-52.8, -16.78) * mm});
            skLineSegment(sketch, "E1153", {"start": v(-52.8, -16.78) * mm, "end": v(-56.78, -12.8) * mm});
            skLineSegment(sketch, "E1154", {"start": v(-56.78, -12.8) * mm, "end": v(-52.8, -12.8) * mm});
            skLineSegment(sketch, "E1155", {"start": v(-52.8, -11.78) * mm, "end": v(-56.78, -7.8) * mm});
            skLineSegment(sketch, "E1156", {"start": v(-56.78, -7.8) * mm, "end": v(-52.8, -7.8) * mm});
            skLineSegment(sketch, "E1157", {"start": v(-52.8, -7.8) * mm, "end": v(-52.8, -11.78) * mm});
            skLineSegment(sketch, "E1158", {"start": v(-47.2, -3.22) * mm, "end": v(-43.22, -7.2) * mm});
            skLineSegment(sketch, "E1159", {"start": v(-43.22, -7.2) * mm, "end": v(-47.2, -7.2) * mm});
            skLineSegment(sketch, "E1160", {"start": v(-47.2, -7.2) * mm, "end": v(-47.2, -3.22) * mm});
            skLineSegment(sketch, "E1161", {"start": v(-46.78, -2.8) * mm, "end": v(-42.8, -2.8) * mm});
            skLineSegment(sketch, "E1162", {"start": v(-42.8, -2.8) * mm, "end": v(-42.8, -6.78) * mm});
            skLineSegment(sketch, "E1163", {"start": v(-42.8, -6.78) * mm, "end": v(-46.78, -2.8) * mm});
            skLineSegment(sketch, "E1164", {"start": v(-37.8, -1.78) * mm, "end": v(-41.78, 2.2) * mm});
            skLineSegment(sketch, "E1165", {"start": v(-41.78, 2.2) * mm, "end": v(-37.8, 2.2) * mm});
            skLineSegment(sketch, "E1166", {"start": v(-37.8, 2.2) * mm, "end": v(-37.8, -1.78) * mm});
            skLineSegment(sketch, "E1167", {"start": v(-32.2, 11.78) * mm, "end": v(-28.22, 7.8) * mm});
            skLineSegment(sketch, "E1168", {"start": v(-28.22, 7.8) * mm, "end": v(-32.2, 7.8) * mm});
            skLineSegment(sketch, "E1169", {"start": v(-32.2, 7.8) * mm, "end": v(-32.2, 11.78) * mm});
            skLineSegment(sketch, "E1170", {"start": v(-22.8, 7.2) * mm, "end": v(-22.8, 3.22) * mm});
            skLineSegment(sketch, "E1171", {"start": v(-22.8, 3.22) * mm, "end": v(-26.78, 7.2) * mm});
            skLineSegment(sketch, "E1172", {"start": v(-26.78, 7.2) * mm, "end": v(-22.8, 7.2) * mm});
            skLineSegment(sketch, "E1173", {"start": v(-22.2, 11.78) * mm, "end": v(-18.22, 7.8) * mm});
            skLineSegment(sketch, "E1174", {"start": v(-18.22, 7.8) * mm, "end": v(-22.2, 7.8) * mm});
            skLineSegment(sketch, "E1175", {"start": v(-22.2, 7.8) * mm, "end": v(-22.2, 11.78) * mm});
            skLineSegment(sketch, "E1176", {"start": v(-17.2, 11.78) * mm, "end": v(-13.22, 7.8) * mm});
            skLineSegment(sketch, "E1177", {"start": v(-13.22, 7.8) * mm, "end": v(-17.2, 7.8) * mm});
            skLineSegment(sketch, "E1178", {"start": v(-17.2, 7.8) * mm, "end": v(-17.2, 11.78) * mm});
            skLineSegment(sketch, "E1179", {"start": v(-7.8, 7.2) * mm, "end": v(-7.8, 3.22) * mm});
            skLineSegment(sketch, "E1180", {"start": v(-7.8, 3.22) * mm, "end": v(-11.78, 7.2) * mm});
            skLineSegment(sketch, "E1181", {"start": v(-11.78, 7.2) * mm, "end": v(-7.8, 7.2) * mm});
            skLineSegment(sketch, "E1182", {"start": v(-7.2, 11.78) * mm, "end": v(-3.22, 7.8) * mm});
            skLineSegment(sketch, "E1183", {"start": v(-3.22, 7.8) * mm, "end": v(-7.2, 7.8) * mm});
            skLineSegment(sketch, "E1184", {"start": v(-7.2, 7.8) * mm, "end": v(-7.2, 11.78) * mm});
            skLineSegment(sketch, "E1185", {"start": v(-2.2, 11.78) * mm, "end": v(1.78, 7.8) * mm});
            skLineSegment(sketch, "E1186", {"start": v(1.78, 7.8) * mm, "end": v(-2.2, 7.8) * mm});
            skLineSegment(sketch, "E1187", {"start": v(-2.2, 7.8) * mm, "end": v(-2.2, 11.78) * mm});
            skLineSegment(sketch, "E1188", {"start": v(7.2, 2.2) * mm, "end": v(7.2, -1.78) * mm});
            skLineSegment(sketch, "E1189", {"start": v(7.2, -1.78) * mm, "end": v(3.22, 2.2) * mm});
            skLineSegment(sketch, "E1190", {"start": v(3.22, 2.2) * mm, "end": v(7.2, 2.2) * mm});
            skLineSegment(sketch, "E1191", {"start": v(7.2, -6.78) * mm, "end": v(3.22, -2.8) * mm});
            skLineSegment(sketch, "E1192", {"start": v(3.22, -2.8) * mm, "end": v(7.2, -2.8) * mm});
            skLineSegment(sketch, "E1193", {"start": v(7.2, -2.8) * mm, "end": v(7.2, -6.78) * mm});
            skLineSegment(sketch, "E1194", {"start": v(6.78, -7.2) * mm, "end": v(5, -7.2) * mm});
            skLineSegment(sketch, "E1195", {"start": v(5, -7.2) * mm, "end": v(2.8, -7.2) * mm});
            skLineSegment(sketch, "E1196", {"start": v(2.8, -7.2) * mm, "end": v(2.8, -3.22) * mm});
            skLineSegment(sketch, "E1197", {"start": v(2.8, -3.22) * mm, "end": v(6.78, -7.2) * mm});
            skLineSegment(sketch, "E1198", {"start": v(6.78, -12.2) * mm, "end": v(2.8, -12.2) * mm});
            skLineSegment(sketch, "E1199", {"start": v(2.8, -12.2) * mm, "end": v(2.8, -8.22) * mm});
            skLineSegment(sketch, "E1200", {"start": v(2.8, -8.22) * mm, "end": v(6.78, -12.2) * mm});
            skLineSegment(sketch, "E1201", {"start": v(6.78, -17.2) * mm, "end": v(2.8, -17.2) * mm});
            skLineSegment(sketch, "E1202", {"start": v(2.8, -17.2) * mm, "end": v(2.8, -13.22) * mm});
            skLineSegment(sketch, "E1203", {"start": v(2.8, -13.22) * mm, "end": v(6.78, -17.2) * mm});
            skLineSegment(sketch, "E1204", {"start": v(6.78, -22.2) * mm, "end": v(5, -22.2) * mm});
            skLineSegment(sketch, "E1205", {"start": v(5, -22.2) * mm, "end": v(2.8, -22.2) * mm});
            skLineSegment(sketch, "E1206", {"start": v(2.8, -22.2) * mm, "end": v(2.8, -18.22) * mm});
            skLineSegment(sketch, "E1207", {"start": v(2.8, -18.22) * mm, "end": v(6.78, -22.2) * mm});
            skLineSegment(sketch, "E1208", {"start": v(6.78, -27.2) * mm, "end": v(2.8, -27.2) * mm});
            skLineSegment(sketch, "E1209", {"start": v(2.8, -27.2) * mm, "end": v(2.8, -23.22) * mm});
            skLineSegment(sketch, "E1210", {"start": v(2.8, -23.22) * mm, "end": v(6.78, -27.2) * mm});
            skLineSegment(sketch, "E1211", {"start": v(7.2, -27.8) * mm, "end": v(7.2, -31.78) * mm});
            skLineSegment(sketch, "E1212", {"start": v(7.2, -31.78) * mm, "end": v(3.22, -27.8) * mm});
            skLineSegment(sketch, "E1213", {"start": v(3.22, -27.8) * mm, "end": v(7.2, -27.8) * mm});
            skLineSegment(sketch, "E1214", {"start": v(2.2, -41.78) * mm, "end": v(-1.78, -37.8) * mm});
            skLineSegment(sketch, "E1215", {"start": v(-1.78, -37.8) * mm, "end": v(2.2, -37.8) * mm});
            skLineSegment(sketch, "E1216", {"start": v(2.2, -37.8) * mm, "end": v(2.2, -41.78) * mm});
            skLineSegment(sketch, "E1217", {"start": v(1.78, -42.2) * mm, "end": v(-2.2, -42.2) * mm});
            skLineSegment(sketch, "E1218", {"start": v(-2.2, -42.2) * mm, "end": v(-2.2, -38.22) * mm});
            skLineSegment(sketch, "E1219", {"start": v(-2.2, -38.22) * mm, "end": v(1.78, -42.2) * mm});
            skLineSegment(sketch, "E1220", {"start": v(-7.8, -51.78) * mm, "end": v(-11.78, -47.8) * mm});
            skLineSegment(sketch, "E1221", {"start": v(-11.78, -47.8) * mm, "end": v(-7.8, -47.8) * mm});
            skLineSegment(sketch, "E1222", {"start": v(-7.8, -47.8) * mm, "end": v(-7.8, -51.78) * mm});
            skLineSegment(sketch, "E1223", {"start": v(-17.8, -61.78) * mm, "end": v(-21.78, -57.8) * mm});
            skLineSegment(sketch, "E1224", {"start": v(-21.78, -57.8) * mm, "end": v(-17.8, -57.8) * mm});
            skLineSegment(sketch, "E1225", {"start": v(-17.8, -57.8) * mm, "end": v(-17.8, -61.78) * mm});
            skLineSegment(sketch, "E1226", {"start": v(-18.22, -62.2) * mm, "end": v(-22.2, -62.2) * mm});
            skLineSegment(sketch, "E1227", {"start": v(-22.2, -62.2) * mm, "end": v(-22.2, -58.23) * mm});
            skLineSegment(sketch, "E1228", {"start": v(-22.2, -58.23) * mm, "end": v(-18.22, -62.2) * mm});
            skLineSegment(sketch, "E1229", {"start": v(-27.8, -71.78) * mm, "end": v(-31.78, -67.8) * mm});
            skLineSegment(sketch, "E1230", {"start": v(-31.78, -67.8) * mm, "end": v(-27.8, -67.8) * mm});
            skLineSegment(sketch, "E1231", {"start": v(-27.8, -67.8) * mm, "end": v(-27.8, -71.78) * mm});
            skLineSegment(sketch, "E1232", {"start": v(-37.8, -81.78) * mm, "end": v(-41.78, -77.8) * mm});
            skLineSegment(sketch, "E1233", {"start": v(-41.78, -77.8) * mm, "end": v(-37.8, -77.8) * mm});
            skLineSegment(sketch, "E1234", {"start": v(-37.8, -77.8) * mm, "end": v(-37.8, -81.78) * mm});
            skLineSegment(sketch, "E1235", {"start": v(-38.22, -82.2) * mm, "end": v(-42.2, -82.2) * mm});
            skLineSegment(sketch, "E1236", {"start": v(-42.2, -82.2) * mm, "end": v(-42.2, -78.22) * mm});
            skLineSegment(sketch, "E1237", {"start": v(-42.2, -78.22) * mm, "end": v(-38.22, -82.2) * mm});
            skLineSegment(sketch, "E1238", {"start": v(-42.2, -83.22) * mm, "end": v(-38.22, -87.2) * mm});
            skLineSegment(sketch, "E1239", {"start": v(-38.22, -87.2) * mm, "end": v(-42.2, -87.2) * mm});
            skLineSegment(sketch, "E1240", {"start": v(-42.2, -87.2) * mm, "end": v(-42.2, -83.22) * mm});
            skLineSegment(sketch, "E1241", {"start": v(-27.2, -78.22) * mm, "end": v(-23.22, -82.2) * mm});
            skLineSegment(sketch, "E1242", {"start": v(-23.22, -82.2) * mm, "end": v(-27.2, -82.2) * mm});
            skLineSegment(sketch, "E1243", {"start": v(-27.2, -82.2) * mm, "end": v(-27.2, -78.22) * mm});
            skLineSegment(sketch, "E1244", {"start": v(-15, -67.8) * mm, "end": v(-12.8, -67.8) * mm});
            skLineSegment(sketch, "E1245", {"start": v(-12.8, -67.8) * mm, "end": v(-12.8, -71.78) * mm});
            skLineSegment(sketch, "E1246", {"start": v(-12.8, -71.78) * mm, "end": v(-16.78, -67.8) * mm});
            skLineSegment(sketch, "E1247", {"start": v(-16.78, -67.8) * mm, "end": v(-15, -67.8) * mm});
            skLineSegment(sketch, "E1248", {"start": v(-7.2, -58.22) * mm, "end": v(-3.22, -62.2) * mm});
            skLineSegment(sketch, "E1249", {"start": v(-3.22, -62.2) * mm, "end": v(-7.2, -62.2) * mm});
            skLineSegment(sketch, "E1250", {"start": v(-7.2, -62.2) * mm, "end": v(-7.2, -58.22) * mm});
            skLineSegment(sketch, "E1251", {"start": v(0, -52.8) * mm, "end": v(2.2, -52.8) * mm});
            skLineSegment(sketch, "E1252", {"start": v(2.2, -52.8) * mm, "end": v(2.2, -56.78) * mm});
            skLineSegment(sketch, "E1253", {"start": v(2.2, -56.78) * mm, "end": v(-1.78, -52.8) * mm});
            skLineSegment(sketch, "E1254", {"start": v(-1.78, -52.8) * mm, "end": v(0, -52.8) * mm});
            skLineSegment(sketch, "E1255", {"start": v(17.2, -37.8) * mm, "end": v(17.2, -41.78) * mm});
            skLineSegment(sketch, "E1256", {"start": v(17.2, -41.78) * mm, "end": v(13.22, -37.8) * mm});
            skLineSegment(sketch, "E1257", {"start": v(13.22, -37.8) * mm, "end": v(17.2, -37.8) * mm});
            skLineSegment(sketch, "E1258", {"start": v(18.22, -27.8) * mm, "end": v(22.2, -27.8) * mm});
            skLineSegment(sketch, "E1259", {"start": v(22.2, -27.8) * mm, "end": v(22.2, -31.78) * mm});
            skLineSegment(sketch, "E1260", {"start": v(22.2, -31.78) * mm, "end": v(18.22, -27.8) * mm});
            skLineSegment(sketch, "E1261", {"start": v(18.22, -22.8) * mm, "end": v(22.2, -22.8) * mm});
            skLineSegment(sketch, "E1262", {"start": v(22.2, -22.8) * mm, "end": v(22.2, -26.78) * mm});
            skLineSegment(sketch, "E1263", {"start": v(22.2, -26.78) * mm, "end": v(18.22, -22.8) * mm});
            skLineSegment(sketch, "E1264", {"start": v(18.22, -17.8) * mm, "end": v(22.2, -17.8) * mm});
            skLineSegment(sketch, "E1265", {"start": v(22.2, -17.8) * mm, "end": v(22.2, -21.78) * mm});
            skLineSegment(sketch, "E1266", {"start": v(22.2, -21.78) * mm, "end": v(18.22, -17.8) * mm});
            skLineSegment(sketch, "E1267", {"start": v(18.22, -12.8) * mm, "end": v(22.2, -12.8) * mm});
            skLineSegment(sketch, "E1268", {"start": v(22.2, -12.8) * mm, "end": v(22.2, -16.78) * mm});
            skLineSegment(sketch, "E1269", {"start": v(22.2, -16.78) * mm, "end": v(18.22, -12.8) * mm});
            skLineSegment(sketch, "E1270", {"start": v(22.2, -6.78) * mm, "end": v(18.22, -2.8) * mm});
            skLineSegment(sketch, "E1271", {"start": v(18.22, -2.8) * mm, "end": v(22.2, -2.8) * mm});
            skLineSegment(sketch, "E1272", {"start": v(22.2, -2.8) * mm, "end": v(22.2, -6.78) * mm});
            skLineSegment(sketch, "E1273", {"start": v(27.2, -6.78) * mm, "end": v(23.22, -2.8) * mm});
            skLineSegment(sketch, "E1274", {"start": v(23.22, -2.8) * mm, "end": v(27.2, -2.8) * mm});
            skLineSegment(sketch, "E1275", {"start": v(27.2, -2.8) * mm, "end": v(27.2, -6.78) * mm});
            skLineSegment(sketch, "E1276", {"start": v(22.8, -2.2) * mm, "end": v(22.8, 1.78) * mm});
            skLineSegment(sketch, "E1277", {"start": v(22.8, 1.78) * mm, "end": v(26.78, -2.2) * mm});
            skLineSegment(sketch, "E1278", {"start": v(26.78, -2.2) * mm, "end": v(22.8, -2.2) * mm});
            skLineSegment(sketch, "E1279", {"start": v(32.8, 11.78) * mm, "end": v(36.78, 7.8) * mm});
            skLineSegment(sketch, "E1280", {"start": v(36.78, 7.8) * mm, "end": v(32.8, 7.8) * mm});
            skLineSegment(sketch, "E1281", {"start": v(32.8, 7.8) * mm, "end": v(32.8, 11.78) * mm});
            skLineSegment(sketch, "E1282", {"start": v(37.2, 8.22) * mm, "end": v(33.22, 12.2) * mm});
            skLineSegment(sketch, "E1283", {"start": v(33.22, 12.2) * mm, "end": v(37.2, 12.2) * mm});
            skLineSegment(sketch, "E1284", {"start": v(37.2, 12.2) * mm, "end": v(37.2, 8.22) * mm});
            skLineSegment(sketch, "E1285", {"start": v(47.2, 18.22) * mm, "end": v(43.22, 22.2) * mm});
            skLineSegment(sketch, "E1286", {"start": v(43.22, 22.2) * mm, "end": v(47.2, 22.2) * mm});
            skLineSegment(sketch, "E1287", {"start": v(47.2, 22.2) * mm, "end": v(47.2, 18.22) * mm});
            skLineSegment(sketch, "E1288", {"start": v(52.8, 22.8) * mm, "end": v(52.8, 26.78) * mm});
            skLineSegment(sketch, "E1289", {"start": v(52.8, 26.78) * mm, "end": v(56.78, 22.8) * mm});
            skLineSegment(sketch, "E1290", {"start": v(56.78, 22.8) * mm, "end": v(52.8, 22.8) * mm});
            skLineSegment(sketch, "E1291", {"start": v(57.2, 28.22) * mm, "end": v(53.22, 32.2) * mm});
            skLineSegment(sketch, "E1292", {"start": v(53.22, 32.2) * mm, "end": v(57.2, 32.2) * mm});
            skLineSegment(sketch, "E1293", {"start": v(57.2, 32.2) * mm, "end": v(57.2, 28.22) * mm});
            skLineSegment(sketch, "E1294", {"start": v(62.2, 32.2) * mm, "end": v(62.2, 28.22) * mm});
            skLineSegment(sketch, "E1295", {"start": v(62.2, 28.22) * mm, "end": v(58.22, 32.2) * mm});
            skLineSegment(sketch, "E1296", {"start": v(58.22, 32.2) * mm, "end": v(62.2, 32.2) * mm});
            skLineSegment(sketch, "E1297", {"start": v(62.8, 32.8) * mm, "end": v(62.8, 36.78) * mm});
            skLineSegment(sketch, "E1298", {"start": v(62.8, 36.78) * mm, "end": v(66.78, 32.8) * mm});
            skLineSegment(sketch, "E1299", {"start": v(66.78, 32.8) * mm, "end": v(62.8, 32.8) * mm});
            skLineSegment(sketch, "E1300", {"start": v(67.2, 38.22) * mm, "end": v(63.22, 42.2) * mm});
            skLineSegment(sketch, "E1301", {"start": v(63.22, 42.2) * mm, "end": v(67.2, 42.2) * mm});
            skLineSegment(sketch, "E1302", {"start": v(67.2, 42.2) * mm, "end": v(67.2, 38.22) * mm});
            skLineSegment(sketch, "E1303", {"start": v(72.2, 42.2) * mm, "end": v(72.2, 38.22) * mm});
            skLineSegment(sketch, "E1304", {"start": v(72.2, 38.22) * mm, "end": v(68.22, 42.2) * mm});
            skLineSegment(sketch, "E1305", {"start": v(68.22, 42.2) * mm, "end": v(72.2, 42.2) * mm});
            skLineSegment(sketch, "E1306", {"start": v(77.2, 52.2) * mm, "end": v(77.2, 48.22) * mm});
            skLineSegment(sketch, "E1307", {"start": v(77.2, 48.22) * mm, "end": v(73.22, 52.2) * mm});
            skLineSegment(sketch, "E1308", {"start": v(73.22, 52.2) * mm, "end": v(77.2, 52.2) * mm});
            skLineSegment(sketch, "E1309", {"start": v(82.2, 57.2) * mm, "end": v(82.2, 53.22) * mm});
            skLineSegment(sketch, "E1310", {"start": v(82.2, 53.22) * mm, "end": v(78.22, 57.2) * mm});
            skLineSegment(sketch, "E1311", {"start": v(78.22, 57.2) * mm, "end": v(82.2, 57.2) * mm});
            skLineSegment(sketch, "E1312", {"start": v(82.8, 62.2) * mm, "end": v(86.78, 62.2) * mm});
            skLineSegment(sketch, "E1313", {"start": v(86.78, 62.2) * mm, "end": v(82.8, 58.22) * mm});
            skLineSegment(sketch, "E1314", {"start": v(82.8, 58.22) * mm, "end": v(82.8, 62.2) * mm});
            skLineSegment(sketch, "E1315", {"start": v(87.2, 62.8) * mm, "end": v(83.22, 62.8) * mm});
            skLineSegment(sketch, "E1316", {"start": v(83.22, 62.8) * mm, "end": v(87.2, 66.78) * mm});
            skLineSegment(sketch, "E1317", {"start": v(87.2, 66.78) * mm, "end": v(87.2, 62.8) * mm});
            skLineSegment(sketch, "E1318", {"start": v(87.8, 72.2) * mm, "end": v(91.78, 72.2) * mm});
            skLineSegment(sketch, "E1319", {"start": v(91.78, 72.2) * mm, "end": v(87.8, 68.22) * mm});
            skLineSegment(sketch, "E1320", {"start": v(87.8, 68.22) * mm, "end": v(87.8, 72.2) * mm});
            skLineSegment(sketch, "E1321", {"start": v(92.2, 72.8) * mm, "end": v(88.22, 72.8) * mm});
            skLineSegment(sketch, "E1322", {"start": v(88.22, 72.8) * mm, "end": v(92.2, 76.78) * mm});
            skLineSegment(sketch, "E1323", {"start": v(92.2, 76.78) * mm, "end": v(92.2, 72.8) * mm});
            skLineSegment(sketch, "E1324", {"start": v(87.8, 73.22) * mm, "end": v(87.8, 77.2) * mm});
            skLineSegment(sketch, "E1325", {"start": v(87.8, 77.2) * mm, "end": v(91.78, 77.2) * mm});
            skLineSegment(sketch, "E1326", {"start": v(91.78, 77.2) * mm, "end": v(87.8, 73.22) * mm});
            skLineSegment(sketch, "E1327", {"start": v(82.8, 68.22) * mm, "end": v(82.8, 72.2) * mm});
            skLineSegment(sketch, "E1328", {"start": v(82.8, 72.2) * mm, "end": v(86.78, 72.2) * mm});
            skLineSegment(sketch, "E1329", {"start": v(86.78, 72.2) * mm, "end": v(82.8, 68.22) * mm});
            skLineSegment(sketch, "E1330", {"start": v(77.8, 63.22) * mm, "end": v(77.8, 67.2) * mm});
            skLineSegment(sketch, "E1331", {"start": v(77.8, 67.2) * mm, "end": v(81.78, 67.2) * mm});
            skLineSegment(sketch, "E1332", {"start": v(81.78, 67.2) * mm, "end": v(77.8, 63.22) * mm});
            skLineSegment(sketch, "E1333", {"start": v(77.2, 58.22) * mm, "end": v(73.22, 62.2) * mm});
            skLineSegment(sketch, "E1334", {"start": v(73.22, 62.2) * mm, "end": v(77.2, 62.2) * mm});
            skLineSegment(sketch, "E1335", {"start": v(77.2, 62.2) * mm, "end": v(77.2, 58.22) * mm});
            skLineSegment(sketch, "E1336", {"start": v(67.2, 48.22) * mm, "end": v(63.22, 52.2) * mm});
            skLineSegment(sketch, "E1337", {"start": v(63.22, 52.2) * mm, "end": v(67.2, 52.2) * mm});
            skLineSegment(sketch, "E1338", {"start": v(67.2, 52.2) * mm, "end": v(67.2, 48.22) * mm});
            skLineSegment(sketch, "E1339", {"start": v(62.2, 43.22) * mm, "end": v(58.22, 47.2) * mm});
            skLineSegment(sketch, "E1340", {"start": v(58.22, 47.2) * mm, "end": v(62.2, 47.2) * mm});
            skLineSegment(sketch, "E1341", {"start": v(62.2, 47.2) * mm, "end": v(62.2, 43.22) * mm});
            skLineSegment(sketch, "E1342", {"start": v(57.2, 38.22) * mm, "end": v(53.22, 42.2) * mm});
            skLineSegment(sketch, "E1343", {"start": v(53.22, 42.2) * mm, "end": v(57.2, 42.2) * mm});
            skLineSegment(sketch, "E1344", {"start": v(57.2, 42.2) * mm, "end": v(57.2, 38.22) * mm});
            skLineSegment(sketch, "E1345", {"start": v(47.2, 28.22) * mm, "end": v(43.22, 32.2) * mm});
            skLineSegment(sketch, "E1346", {"start": v(43.22, 32.2) * mm, "end": v(47.2, 32.2) * mm});
            skLineSegment(sketch, "E1347", {"start": v(47.2, 32.2) * mm, "end": v(47.2, 28.22) * mm});
            skLineSegment(sketch, "E1348", {"start": v(27.8, 22.8) * mm, "end": v(27.8, 26.78) * mm});
            skLineSegment(sketch, "E1349", {"start": v(27.8, 26.78) * mm, "end": v(31.78, 22.8) * mm});
            skLineSegment(sketch, "E1350", {"start": v(31.78, 22.8) * mm, "end": v(27.8, 22.8) * mm});
            skLineSegment(sketch, "E1351", {"start": v(23.22, 32.2) * mm, "end": v(27.2, 32.2) * mm});
            skLineSegment(sketch, "E1352", {"start": v(27.2, 32.2) * mm, "end": v(27.2, 28.22) * mm});
            skLineSegment(sketch, "E1353", {"start": v(27.2, 28.22) * mm, "end": v(23.22, 32.2) * mm});
            skLineSegment(sketch, "E1354", {"start": v(27.8, 46.78) * mm, "end": v(31.78, 42.8) * mm});
            skLineSegment(sketch, "E1355", {"start": v(31.78, 42.8) * mm, "end": v(27.8, 42.8) * mm});
            skLineSegment(sketch, "E1356", {"start": v(27.8, 42.8) * mm, "end": v(27.8, 46.78) * mm});
            skLineSegment(sketch, "E1357", {"start": v(32.8, 51.78) * mm, "end": v(36.78, 47.8) * mm});
            skLineSegment(sketch, "E1358", {"start": v(36.78, 47.8) * mm, "end": v(32.8, 47.8) * mm});
            skLineSegment(sketch, "E1359", {"start": v(32.8, 47.8) * mm, "end": v(32.8, 51.78) * mm});
            skLineSegment(sketch, "E1360", {"start": v(37.8, 56.78) * mm, "end": v(41.78, 52.8) * mm});
            skLineSegment(sketch, "E1361", {"start": v(41.78, 52.8) * mm, "end": v(37.8, 52.8) * mm});
            skLineSegment(sketch, "E1362", {"start": v(37.8, 52.8) * mm, "end": v(37.8, 56.78) * mm});
            skLineSegment(sketch, "E1363", {"start": v(42.8, 61.78) * mm, "end": v(46.78, 57.8) * mm});
            skLineSegment(sketch, "E1364", {"start": v(46.78, 57.8) * mm, "end": v(42.8, 57.8) * mm});
            skLineSegment(sketch, "E1365", {"start": v(42.8, 57.8) * mm, "end": v(42.8, 61.78) * mm});
            skLineSegment(sketch, "E1366", {"start": v(47.8, 66.78) * mm, "end": v(51.78, 62.8) * mm});
            skLineSegment(sketch, "E1367", {"start": v(51.78, 62.8) * mm, "end": v(47.8, 62.8) * mm});
            skLineSegment(sketch, "E1368", {"start": v(47.8, 62.8) * mm, "end": v(47.8, 66.78) * mm});
            skLineSegment(sketch, "E1369", {"start": v(52.8, 71.78) * mm, "end": v(56.78, 67.8) * mm});
            skLineSegment(sketch, "E1370", {"start": v(56.78, 67.8) * mm, "end": v(52.8, 67.8) * mm});
            skLineSegment(sketch, "E1371", {"start": v(52.8, 67.8) * mm, "end": v(52.8, 71.78) * mm});
            skLineSegment(sketch, "E1372", {"start": v(57.8, 76.78) * mm, "end": v(61.78, 72.8) * mm});
            skLineSegment(sketch, "E1373", {"start": v(61.78, 72.8) * mm, "end": v(57.8, 72.8) * mm});
            skLineSegment(sketch, "E1374", {"start": v(57.8, 72.8) * mm, "end": v(57.8, 76.78) * mm});
            skLineSegment(sketch, "E1375", {"start": v(67.2, 81.78) * mm, "end": v(67.2, 77.8) * mm});
            skLineSegment(sketch, "E1376", {"start": v(67.2, 77.8) * mm, "end": v(63.22, 77.8) * mm});
            skLineSegment(sketch, "E1377", {"start": v(63.22, 77.8) * mm, "end": v(67.2, 81.78) * mm});
            skLineSegment(sketch, "E1378", {"start": v(72.8, 88.22) * mm, "end": v(72.8, 92.2) * mm});
            skLineSegment(sketch, "E1379", {"start": v(72.8, 92.2) * mm, "end": v(76.78, 92.2) * mm});
            skLineSegment(sketch, "E1380", {"start": v(76.78, 92.2) * mm, "end": v(72.8, 88.22) * mm});
            skLineSegment(sketch, "E1381", {"start": v(72.2, 87.8) * mm, "end": v(68.22, 87.8) * mm});
            skLineSegment(sketch, "E1382", {"start": v(68.22, 87.8) * mm, "end": v(72.2, 91.78) * mm});
            skLineSegment(sketch, "E1383", {"start": v(72.2, 91.78) * mm, "end": v(72.2, 87.8) * mm});
            skLineSegment(sketch, "E1384", {"start": v(67.8, 88.22) * mm, "end": v(67.8, 92.2) * mm});
            skLineSegment(sketch, "E1385", {"start": v(67.8, 92.2) * mm, "end": v(71.78, 92.2) * mm});
            skLineSegment(sketch, "E1386", {"start": v(71.78, 92.2) * mm, "end": v(67.8, 88.22) * mm});
            skLineSegment(sketch, "E1387", {"start": v(62.8, 83.22) * mm, "end": v(62.8, 87.2) * mm});
            skLineSegment(sketch, "E1388", {"start": v(62.8, 87.2) * mm, "end": v(66.78, 87.2) * mm});
            skLineSegment(sketch, "E1389", {"start": v(66.78, 87.2) * mm, "end": v(62.8, 83.22) * mm});
            skLineSegment(sketch, "E1390", {"start": v(57.8, 83.22) * mm, "end": v(57.8, 87.2) * mm});
            skLineSegment(sketch, "E1391", {"start": v(57.8, 87.2) * mm, "end": v(61.78, 87.2) * mm});
            skLineSegment(sketch, "E1392", {"start": v(61.78, 87.2) * mm, "end": v(57.8, 83.22) * mm});
            skLineSegment(sketch, "E1393", {"start": v(57.2, 78.22) * mm, "end": v(53.22, 82.2) * mm});
            skLineSegment(sketch, "E1394", {"start": v(53.22, 82.2) * mm, "end": v(57.2, 82.2) * mm});
            skLineSegment(sketch, "E1395", {"start": v(57.2, 82.2) * mm, "end": v(57.2, 78.22) * mm});
            skLineSegment(sketch, "E1396", {"start": v(37.2, 63.22) * mm, "end": v(33.22, 67.2) * mm});
            skLineSegment(sketch, "E1397", {"start": v(33.22, 67.2) * mm, "end": v(37.2, 67.2) * mm});
            skLineSegment(sketch, "E1398", {"start": v(37.2, 67.2) * mm, "end": v(37.2, 63.22) * mm});
            skLineSegment(sketch, "E1399", {"start": v(32.2, 58.22) * mm, "end": v(28.22, 62.2) * mm});
            skLineSegment(sketch, "E1400", {"start": v(28.22, 62.2) * mm, "end": v(32.2, 62.2) * mm});
            skLineSegment(sketch, "E1401", {"start": v(32.2, 62.2) * mm, "end": v(32.2, 58.22) * mm});
            skLineSegment(sketch, "E1402", {"start": v(27.2, 53.22) * mm, "end": v(23.22, 57.2) * mm});
            skLineSegment(sketch, "E1403", {"start": v(23.22, 57.2) * mm, "end": v(27.2, 57.2) * mm});
            skLineSegment(sketch, "E1404", {"start": v(27.2, 57.2) * mm, "end": v(27.2, 53.22) * mm});
            skLineSegment(sketch, "E1405", {"start": v(22.2, 52.2) * mm, "end": v(22.2, 48.22) * mm});
            skLineSegment(sketch, "E1406", {"start": v(22.2, 48.22) * mm, "end": v(18.22, 52.2) * mm});
            skLineSegment(sketch, "E1407", {"start": v(18.22, 52.2) * mm, "end": v(22.2, 52.2) * mm});
            skLineSegment(sketch, "E1408", {"start": v(17.2, 43.22) * mm, "end": v(13.22, 47.2) * mm});
            skLineSegment(sketch, "E1409", {"start": v(13.22, 47.2) * mm, "end": v(17.2, 47.2) * mm});
            skLineSegment(sketch, "E1410", {"start": v(17.2, 47.2) * mm, "end": v(17.2, 43.22) * mm});
            skLineSegment(sketch, "E1411", {"start": v(12.2, 38.22) * mm, "end": v(8.22, 42.2) * mm});
            skLineSegment(sketch, "E1412", {"start": v(8.22, 42.2) * mm, "end": v(12.2, 42.2) * mm});
            skLineSegment(sketch, "E1413", {"start": v(12.2, 42.2) * mm, "end": v(12.2, 38.22) * mm});
            skLineSegment(sketch, "E1414", {"start": v(7.2, 33.22) * mm, "end": v(3.22, 37.2) * mm});
            skLineSegment(sketch, "E1415", {"start": v(3.22, 37.2) * mm, "end": v(7.2, 37.2) * mm});
            skLineSegment(sketch, "E1416", {"start": v(7.2, 37.2) * mm, "end": v(7.2, 33.22) * mm});
            skLineSegment(sketch, "E1417", {"start": v(6.78, 27.8) * mm, "end": v(2.8, 27.8) * mm});
            skLineSegment(sketch, "E1418", {"start": v(2.8, 27.8) * mm, "end": v(2.8, 31.78) * mm});
            skLineSegment(sketch, "E1419", {"start": v(2.8, 31.78) * mm, "end": v(6.78, 27.8) * mm});
            skLineSegment(sketch, "E1420", {"start": v(2.2, 23.22) * mm, "end": v(-1.78, 27.2) * mm});
            skLineSegment(sketch, "E1421", {"start": v(-1.78, 27.2) * mm, "end": v(2.2, 27.2) * mm});
            skLineSegment(sketch, "E1422", {"start": v(2.2, 27.2) * mm, "end": v(2.2, 23.22) * mm});
            skLineSegment(sketch, "E1423", {"start": v(1.78, 22.8) * mm, "end": v(-2.2, 22.8) * mm});
            skLineSegment(sketch, "E1424", {"start": v(-2.2, 22.8) * mm, "end": v(-2.2, 26.78) * mm});
            skLineSegment(sketch, "E1425", {"start": v(-2.2, 26.78) * mm, "end": v(1.78, 22.8) * mm});
            skLineSegment(sketch, "E1426", {"start": v(-12.8, 18.22) * mm, "end": v(-16.78, 22.2) * mm});
            skLineSegment(sketch, "E1427", {"start": v(-16.78, 22.2) * mm, "end": v(-12.8, 22.2) * mm});
            skLineSegment(sketch, "E1428", {"start": v(-12.8, 22.2) * mm, "end": v(-12.8, 18.22) * mm});
            skLineSegment(sketch, "E1429", {"start": v(-13.22, 17.8) * mm, "end": v(-17.2, 17.8) * mm});
            skLineSegment(sketch, "E1430", {"start": v(-17.2, 17.8) * mm, "end": v(-17.2, 21.78) * mm});
            skLineSegment(sketch, "E1431", {"start": v(-17.2, 21.78) * mm, "end": v(-13.22, 17.8) * mm});
            skLineSegment(sketch, "E1432", {"start": v(-27.2, 17.8) * mm, "end": v(-27.2, 21.78) * mm});
            skLineSegment(sketch, "E1433", {"start": v(-27.2, 21.78) * mm, "end": v(-23.22, 17.8) * mm});
            skLineSegment(sketch, "E1434", {"start": v(-23.22, 17.8) * mm, "end": v(-27.2, 17.8) * mm});
            skLineSegment(sketch, "E1435", {"start": v(-27.8, 18.22) * mm, "end": v(-31.78, 22.2) * mm});
            skLineSegment(sketch, "E1436", {"start": v(-31.78, 22.2) * mm, "end": v(-27.8, 22.2) * mm});
            skLineSegment(sketch, "E1437", {"start": v(-27.8, 22.2) * mm, "end": v(-27.8, 18.22) * mm});
            skLineSegment(sketch, "E1438", {"start": v(-28.22, 17.8) * mm, "end": v(-32.2, 17.8) * mm});
            skLineSegment(sketch, "E1439", {"start": v(-32.2, 17.8) * mm, "end": v(-32.2, 21.78) * mm});
            skLineSegment(sketch, "E1440", {"start": v(-32.2, 21.78) * mm, "end": v(-28.22, 17.8) * mm});
            skLineSegment(sketch, "E1441", {"start": v(-37.8, 13.22) * mm, "end": v(-41.78, 17.2) * mm});
            skLineSegment(sketch, "E1442", {"start": v(-41.78, 17.2) * mm, "end": v(-37.8, 17.2) * mm});
            skLineSegment(sketch, "E1443", {"start": v(-37.8, 17.2) * mm, "end": v(-37.8, 13.22) * mm});
            skLineSegment(sketch, "E1444", {"start": v(-42.8, 8.22) * mm, "end": v(-46.78, 12.2) * mm});
            skLineSegment(sketch, "E1445", {"start": v(-46.78, 12.2) * mm, "end": v(-42.8, 12.2) * mm});
            skLineSegment(sketch, "E1446", {"start": v(-42.8, 12.2) * mm, "end": v(-42.8, 8.22) * mm});
            skLineSegment(sketch, "E1447", {"start": v(-47.8, 3.22) * mm, "end": v(-51.78, 7.2) * mm});
            skLineSegment(sketch, "E1448", {"start": v(-51.78, 7.2) * mm, "end": v(-47.8, 7.2) * mm});
            skLineSegment(sketch, "E1449", {"start": v(-47.8, 7.2) * mm, "end": v(-47.8, 3.22) * mm});
            skLineSegment(sketch, "E1450", {"start": v(-52.8, 2.8) * mm, "end": v(-56.78, 2.8) * mm});
            skLineSegment(sketch, "E1451", {"start": v(-56.78, 2.8) * mm, "end": v(-52.8, 6.78) * mm});
            skLineSegment(sketch, "E1452", {"start": v(-52.8, 6.78) * mm, "end": v(-52.8, 2.8) * mm});
            skLineSegment(sketch, "E1453", {"start": v(-62.8, -11.78) * mm, "end": v(-66.78, -7.8) * mm});
            skLineSegment(sketch, "E1454", {"start": v(-66.78, -7.8) * mm, "end": v(-62.8, -7.8) * mm});
            skLineSegment(sketch, "E1455", {"start": v(-62.8, -7.8) * mm, "end": v(-62.8, -11.78) * mm});
            skLineSegment(sketch, "E1456", {"start": v(-72.8, -21.78) * mm, "end": v(-76.78, -17.8) * mm});
            skLineSegment(sketch, "E1457", {"start": v(-76.78, -17.8) * mm, "end": v(-72.8, -17.8) * mm});
            skLineSegment(sketch, "E1458", {"start": v(-72.8, -17.8) * mm, "end": v(-72.8, -21.78) * mm});
            skLineSegment(sketch, "E1459", {"start": v(-82.8, -31.78) * mm, "end": v(-86.78, -27.8) * mm});
            skLineSegment(sketch, "E1460", {"start": v(-86.78, -27.8) * mm, "end": v(-82.8, -27.8) * mm});
            skLineSegment(sketch, "E1461", {"start": v(-82.8, -27.8) * mm, "end": v(-82.8, -31.78) * mm});
            skLineSegment(sketch, "E1462", {"start": v(-77.8, -37.8) * mm, "end": v(-77.8, -41.78) * mm});
            skLineSegment(sketch, "E1463", {"start": v(-77.8, -41.78) * mm, "end": v(-81.78, -37.8) * mm});
            skLineSegment(sketch, "E1464", {"start": v(-81.78, -37.8) * mm, "end": v(-77.8, -37.8) * mm});
            skLineSegment(sketch, "E1465", {"start": v(-57.2, -13.22) * mm, "end": v(-53.22, -17.2) * mm});
            skLineSegment(sketch, "E1466", {"start": v(-53.22, -17.2) * mm, "end": v(-57.2, -17.2) * mm});
            skLineSegment(sketch, "E1467", {"start": v(-57.2, -17.2) * mm, "end": v(-57.2, -13.22) * mm});
            skLineSegment(sketch, "E1468", {"start": v(-52.2, -12.2) * mm, "end": v(-52.2, -8.22) * mm});
            skLineSegment(sketch, "E1469", {"start": v(-52.2, -8.22) * mm, "end": v(-48.22, -12.2) * mm});
            skLineSegment(sketch, "E1470", {"start": v(-48.22, -12.2) * mm, "end": v(-52.2, -12.2) * mm});
            skLineSegment(sketch, "E1471", {"start": v(-37.2, 2.8) * mm, "end": v(-37.2, 6.78) * mm});
            skLineSegment(sketch, "E1472", {"start": v(-37.2, 6.78) * mm, "end": v(-33.22, 2.8) * mm});
            skLineSegment(sketch, "E1473", {"start": v(-33.22, 2.8) * mm, "end": v(-37.2, 2.8) * mm});
            skLineSegment(sketch, "E1474", {"start": v(-27.8, 7.2) * mm, "end": v(-27.8, 3.22) * mm});
            skLineSegment(sketch, "E1475", {"start": v(-27.8, 3.22) * mm, "end": v(-31.78, 7.2) * mm});
            skLineSegment(sketch, "E1476", {"start": v(-31.78, 7.2) * mm, "end": v(-27.8, 7.2) * mm});
            skLineSegment(sketch, "E1477", {"start": v(-27.2, 6.78) * mm, "end": v(-23.22, 2.8) * mm});
            skLineSegment(sketch, "E1478", {"start": v(-23.22, 2.8) * mm, "end": v(-27.2, 2.8) * mm});
            skLineSegment(sketch, "E1479", {"start": v(-27.2, 2.8) * mm, "end": v(-27.2, 6.78) * mm});
            skLineSegment(sketch, "E1480", {"start": v(-22.2, 6.78) * mm, "end": v(-18.22, 2.8) * mm});
            skLineSegment(sketch, "E1481", {"start": v(-18.22, 2.8) * mm, "end": v(-22.2, 2.8) * mm});
            skLineSegment(sketch, "E1482", {"start": v(-22.2, 2.8) * mm, "end": v(-22.2, 6.78) * mm});
            skLineSegment(sketch, "E1483", {"start": v(-21.78, 7.2) * mm, "end": v(-17.8, 7.2) * mm});
            skLineSegment(sketch, "E1484", {"start": v(-17.8, 7.2) * mm, "end": v(-17.8, 3.22) * mm});
            skLineSegment(sketch, "E1485", {"start": v(-17.8, 3.22) * mm, "end": v(-21.78, 7.2) * mm});
            skLineSegment(sketch, "E1486", {"start": v(-12.8, 7.2) * mm, "end": v(-12.8, 3.22) * mm});
            skLineSegment(sketch, "E1487", {"start": v(-12.8, 3.22) * mm, "end": v(-16.78, 7.2) * mm});
            skLineSegment(sketch, "E1488", {"start": v(-16.78, 7.2) * mm, "end": v(-12.8, 7.2) * mm});
            skLineSegment(sketch, "E1489", {"start": v(-12.2, 6.78) * mm, "end": v(-8.22, 2.8) * mm});
            skLineSegment(sketch, "E1490", {"start": v(-8.22, 2.8) * mm, "end": v(-12.2, 2.8) * mm});
            skLineSegment(sketch, "E1491", {"start": v(-12.2, 2.8) * mm, "end": v(-12.2, 6.78) * mm});
            skLineSegment(sketch, "E1492", {"start": v(-7.2, 6.78) * mm, "end": v(-3.22, 2.8) * mm});
            skLineSegment(sketch, "E1493", {"start": v(-3.22, 2.8) * mm, "end": v(-7.2, 2.8) * mm});
            skLineSegment(sketch, "E1494", {"start": v(-7.2, 2.8) * mm, "end": v(-7.2, 6.78) * mm});
            skLineSegment(sketch, "E1495", {"start": v(-6.78, 7.2) * mm, "end": v(-2.8, 7.2) * mm});
            skLineSegment(sketch, "E1496", {"start": v(-2.8, 7.2) * mm, "end": v(-2.8, 3.22) * mm});
            skLineSegment(sketch, "E1497", {"start": v(-2.8, 3.22) * mm, "end": v(-6.78, 7.2) * mm});
            skLineSegment(sketch, "E1498", {"start": v(2.2, 7.2) * mm, "end": v(2.2, 3.22) * mm});
            skLineSegment(sketch, "E1499", {"start": v(2.2, 3.22) * mm, "end": v(-1.78, 7.2) * mm});
            skLineSegment(sketch, "E1500", {"start": v(-1.78, 7.2) * mm, "end": v(2.2, 7.2) * mm});
            skLineSegment(sketch, "E1501", {"start": v(6.78, -2.2) * mm, "end": v(2.8, -2.2) * mm});
            skLineSegment(sketch, "E1502", {"start": v(2.8, -2.2) * mm, "end": v(2.8, 1.78) * mm});
            skLineSegment(sketch, "E1503", {"start": v(2.8, 1.78) * mm, "end": v(6.78, -2.2) * mm});
            skLineSegment(sketch, "E1504", {"start": v(6.78, -32.2) * mm, "end": v(2.8, -32.2) * mm});
            skLineSegment(sketch, "E1505", {"start": v(2.8, -32.2) * mm, "end": v(2.8, -28.22) * mm});
            skLineSegment(sketch, "E1506", {"start": v(2.8, -28.22) * mm, "end": v(6.78, -32.2) * mm});
            skLineSegment(sketch, "E1507", {"start": v(-12.8, -52.2) * mm, "end": v(-16.78, -52.2) * mm});
            skLineSegment(sketch, "E1508", {"start": v(-16.78, -52.2) * mm, "end": v(-12.8, -48.22) * mm});
            skLineSegment(sketch, "E1509", {"start": v(-12.8, -48.22) * mm, "end": v(-12.8, -52.2) * mm});
            skLineSegment(sketch, "E1510", {"start": v(-32.8, -72.2) * mm, "end": v(-36.78, -72.2) * mm});
            skLineSegment(sketch, "E1511", {"start": v(-36.78, -72.2) * mm, "end": v(-32.8, -68.22) * mm});
            skLineSegment(sketch, "E1512", {"start": v(-32.8, -68.22) * mm, "end": v(-32.8, -72.2) * mm});
            skLineSegment(sketch, "E1513", {"start": v(-32.8, -87.8) * mm, "end": v(-32.8, -91.78) * mm});
            skLineSegment(sketch, "E1514", {"start": v(-32.8, -91.78) * mm, "end": v(-36.77, -87.8) * mm});
            skLineSegment(sketch, "E1515", {"start": v(-36.77, -87.8) * mm, "end": v(-32.8, -87.8) * mm});
            skLineSegment(sketch, "E1516", {"start": v(-32.2, -87.2) * mm, "end": v(-32.2, -83.22) * mm});
            skLineSegment(sketch, "E1517", {"start": v(-32.2, -83.22) * mm, "end": v(-28.22, -87.2) * mm});
            skLineSegment(sketch, "E1518", {"start": v(-28.22, -87.2) * mm, "end": v(-32.2, -87.2) * mm});
            skLineSegment(sketch, "E1519", {"start": v(-22.2, -77.2) * mm, "end": v(-22.2, -73.22) * mm});
            skLineSegment(sketch, "E1520", {"start": v(-22.2, -73.22) * mm, "end": v(-18.22, -77.2) * mm});
            skLineSegment(sketch, "E1521", {"start": v(-18.22, -77.2) * mm, "end": v(-22.2, -77.2) * mm});
            skLineSegment(sketch, "E1522", {"start": v(-17.2, -68.22) * mm, "end": v(-13.22, -72.2) * mm});
            skLineSegment(sketch, "E1523", {"start": v(-13.22, -72.2) * mm, "end": v(-17.2, -72.2) * mm});
            skLineSegment(sketch, "E1524", {"start": v(-17.2, -72.2) * mm, "end": v(-17.2, -68.22) * mm});
            skLineSegment(sketch, "E1525", {"start": v(-12.2, -67.2) * mm, "end": v(-12.2, -63.22) * mm});
            skLineSegment(sketch, "E1526", {"start": v(-12.2, -63.22) * mm, "end": v(-8.22, -67.2) * mm});
            skLineSegment(sketch, "E1527", {"start": v(-8.22, -67.2) * mm, "end": v(-12.2, -67.2) * mm});
            skLineSegment(sketch, "E1528", {"start": v(-2.2, -57.2) * mm, "end": v(-2.2, -53.22) * mm});
            skLineSegment(sketch, "E1529", {"start": v(-2.2, -53.22) * mm, "end": v(1.78, -57.2) * mm});
            skLineSegment(sketch, "E1530", {"start": v(1.78, -57.2) * mm, "end": v(-2.2, -57.2) * mm});
            skLineSegment(sketch, "E1531", {"start": v(2.8, -52.8) * mm, "end": v(6.78, -52.8) * mm});
            skLineSegment(sketch, "E1532", {"start": v(6.78, -52.8) * mm, "end": v(2.8, -56.78) * mm});
            skLineSegment(sketch, "E1533", {"start": v(2.8, -56.78) * mm, "end": v(2.8, -52.8) * mm});
            skLineSegment(sketch, "E1534", {"start": v(7.8, -43.22) * mm, "end": v(11.78, -47.2) * mm});
            skLineSegment(sketch, "E1535", {"start": v(11.78, -47.2) * mm, "end": v(7.8, -47.2) * mm});
            skLineSegment(sketch, "E1536", {"start": v(7.8, -47.2) * mm, "end": v(7.8, -43.22) * mm});
            skLineSegment(sketch, "E1537", {"start": v(12.8, -38.22) * mm, "end": v(16.78, -42.2) * mm});
            skLineSegment(sketch, "E1538", {"start": v(16.78, -42.2) * mm, "end": v(12.8, -42.2) * mm});
            skLineSegment(sketch, "E1539", {"start": v(12.8, -42.2) * mm, "end": v(12.8, -38.22) * mm});
            skLineSegment(sketch, "E1540", {"start": v(17.8, -33.22) * mm, "end": v(21.78, -37.2) * mm});
            skLineSegment(sketch, "E1541", {"start": v(21.78, -37.2) * mm, "end": v(17.8, -37.2) * mm});
            skLineSegment(sketch, "E1542", {"start": v(17.8, -37.2) * mm, "end": v(17.8, -33.22) * mm});
            skLineSegment(sketch, "E1543", {"start": v(22.8, -3.22) * mm, "end": v(26.78, -7.2) * mm});
            skLineSegment(sketch, "E1544", {"start": v(26.78, -7.2) * mm, "end": v(22.8, -7.2) * mm});
            skLineSegment(sketch, "E1545", {"start": v(22.8, -7.2) * mm, "end": v(22.8, -3.22) * mm});
            skLineSegment(sketch, "E1546", {"start": v(23.22, 2.2) * mm, "end": v(27.2, 2.2) * mm});
            skLineSegment(sketch, "E1547", {"start": v(27.2, 2.2) * mm, "end": v(27.2, -1.78) * mm});
            skLineSegment(sketch, "E1548", {"start": v(27.2, -1.78) * mm, "end": v(23.22, 2.2) * mm});
            skLineSegment(sketch, "E1549", {"start": v(27.8, 6.78) * mm, "end": v(31.78, 2.8) * mm});
            skLineSegment(sketch, "E1550", {"start": v(31.78, 2.8) * mm, "end": v(27.8, 2.8) * mm});
            skLineSegment(sketch, "E1551", {"start": v(27.8, 2.8) * mm, "end": v(27.8, 6.78) * mm});
            skLineSegment(sketch, "E1552", {"start": v(32.8, 5) * mm, "end": v(32.8, 6.78) * mm});
            skLineSegment(sketch, "E1553", {"start": v(32.8, 6.78) * mm, "end": v(36.78, 2.8) * mm});
            skLineSegment(sketch, "E1554", {"start": v(36.78, 2.8) * mm, "end": v(32.8, 2.8) * mm});
            skLineSegment(sketch, "E1555", {"start": v(32.8, 2.8) * mm, "end": v(32.8, 5) * mm});
            skLineSegment(sketch, "E1556", {"start": v(33.22, 7.2) * mm, "end": v(37.2, 7.2) * mm});
            skLineSegment(sketch, "E1557", {"start": v(37.2, 7.2) * mm, "end": v(37.2, 3.22) * mm});
            skLineSegment(sketch, "E1558", {"start": v(37.2, 3.22) * mm, "end": v(33.22, 7.2) * mm});
            skLineSegment(sketch, "E1559", {"start": v(37.8, 11.78) * mm, "end": v(41.78, 7.8) * mm});
            skLineSegment(sketch, "E1560", {"start": v(41.78, 7.8) * mm, "end": v(37.8, 7.8) * mm});
            skLineSegment(sketch, "E1561", {"start": v(37.8, 7.8) * mm, "end": v(37.8, 11.78) * mm});
            skLineSegment(sketch, "E1562", {"start": v(42.8, 16.78) * mm, "end": v(46.78, 12.8) * mm});
            skLineSegment(sketch, "E1563", {"start": v(46.78, 12.8) * mm, "end": v(42.8, 12.8) * mm});
            skLineSegment(sketch, "E1564", {"start": v(42.8, 12.8) * mm, "end": v(42.8, 16.78) * mm});
            skLineSegment(sketch, "E1565", {"start": v(47.8, 21.78) * mm, "end": v(51.78, 17.8) * mm});
            skLineSegment(sketch, "E1566", {"start": v(51.78, 17.8) * mm, "end": v(47.8, 17.8) * mm});
            skLineSegment(sketch, "E1567", {"start": v(47.8, 17.8) * mm, "end": v(47.8, 21.78) * mm});
            skLineSegment(sketch, "E1568", {"start": v(57.8, 31.78) * mm, "end": v(61.78, 27.8) * mm});
            skLineSegment(sketch, "E1569", {"start": v(61.78, 27.8) * mm, "end": v(57.8, 27.8) * mm});
            skLineSegment(sketch, "E1570", {"start": v(57.8, 27.8) * mm, "end": v(57.8, 31.78) * mm});
            skLineSegment(sketch, "E1571", {"start": v(67.8, 41.78) * mm, "end": v(71.78, 37.8) * mm});
            skLineSegment(sketch, "E1572", {"start": v(71.78, 37.8) * mm, "end": v(67.8, 37.8) * mm});
            skLineSegment(sketch, "E1573", {"start": v(67.8, 37.8) * mm, "end": v(67.8, 41.78) * mm});
            skLineSegment(sketch, "E1574", {"start": v(72.8, 51.78) * mm, "end": v(76.78, 47.8) * mm});
            skLineSegment(sketch, "E1575", {"start": v(76.78, 47.8) * mm, "end": v(72.8, 47.8) * mm});
            skLineSegment(sketch, "E1576", {"start": v(72.8, 47.8) * mm, "end": v(72.8, 51.78) * mm});
            skLineSegment(sketch, "E1577", {"start": v(77.8, 56.78) * mm, "end": v(81.78, 52.8) * mm});
            skLineSegment(sketch, "E1578", {"start": v(81.78, 52.8) * mm, "end": v(77.8, 52.8) * mm});
            skLineSegment(sketch, "E1579", {"start": v(77.8, 52.8) * mm, "end": v(77.8, 56.78) * mm});
            skLineSegment(sketch, "E1580", {"start": v(83.22, 57.8) * mm, "end": v(87.2, 61.78) * mm});
            skLineSegment(sketch, "E1581", {"start": v(87.2, 61.78) * mm, "end": v(87.2, 57.8) * mm});
            skLineSegment(sketch, "E1582", {"start": v(87.2, 57.8) * mm, "end": v(83.22, 57.8) * mm});
            skLineSegment(sketch, "E1583", {"start": v(88.22, 67.8) * mm, "end": v(92.2, 71.78) * mm});
            skLineSegment(sketch, "E1584", {"start": v(92.2, 71.78) * mm, "end": v(92.2, 67.8) * mm});
            skLineSegment(sketch, "E1585", {"start": v(92.2, 67.8) * mm, "end": v(88.22, 67.8) * mm});
            skLineSegment(sketch, "E1586", {"start": v(87.2, 76.78) * mm, "end": v(87.2, 72.8) * mm});
            skLineSegment(sketch, "E1587", {"start": v(87.2, 72.8) * mm, "end": v(83.22, 72.8) * mm});
            skLineSegment(sketch, "E1588", {"start": v(83.22, 72.8) * mm, "end": v(87.2, 76.78) * mm});
            skLineSegment(sketch, "E1589", {"start": v(82.2, 71.78) * mm, "end": v(82.2, 67.8) * mm});
            skLineSegment(sketch, "E1590", {"start": v(82.2, 67.8) * mm, "end": v(78.22, 67.8) * mm});
            skLineSegment(sketch, "E1591", {"start": v(78.22, 67.8) * mm, "end": v(82.2, 71.78) * mm});
            skLineSegment(sketch, "E1592", {"start": v(77.2, 66.78) * mm, "end": v(77.2, 62.8) * mm});
            skLineSegment(sketch, "E1593", {"start": v(77.2, 62.8) * mm, "end": v(73.22, 62.8) * mm});
            skLineSegment(sketch, "E1594", {"start": v(73.22, 62.8) * mm, "end": v(77.2, 66.78) * mm});
            skLineSegment(sketch, "E1595", {"start": v(72.2, 61.78) * mm, "end": v(72.2, 57.8) * mm});
            skLineSegment(sketch, "E1596", {"start": v(72.2, 57.8) * mm, "end": v(68.22, 57.8) * mm});
            skLineSegment(sketch, "E1597", {"start": v(68.22, 57.8) * mm, "end": v(72.2, 61.78) * mm});
            skLineSegment(sketch, "E1598", {"start": v(67.2, 56.78) * mm, "end": v(67.2, 52.8) * mm});
            skLineSegment(sketch, "E1599", {"start": v(67.2, 52.8) * mm, "end": v(63.22, 52.8) * mm});
            skLineSegment(sketch, "E1600", {"start": v(63.22, 52.8) * mm, "end": v(67.2, 56.78) * mm});
            skLineSegment(sketch, "E1601", {"start": v(62.2, 51.78) * mm, "end": v(62.2, 47.8) * mm});
            skLineSegment(sketch, "E1602", {"start": v(62.2, 47.8) * mm, "end": v(58.22, 47.8) * mm});
            skLineSegment(sketch, "E1603", {"start": v(58.22, 47.8) * mm, "end": v(62.2, 51.78) * mm});
            skLineSegment(sketch, "E1604", {"start": v(57.2, 46.78) * mm, "end": v(57.2, 42.8) * mm});
            skLineSegment(sketch, "E1605", {"start": v(57.2, 42.8) * mm, "end": v(53.22, 42.8) * mm});
            skLineSegment(sketch, "E1606", {"start": v(53.22, 42.8) * mm, "end": v(57.2, 46.78) * mm});
            skLineSegment(sketch, "E1607", {"start": v(52.2, 41.78) * mm, "end": v(52.2, 37.8) * mm});
            skLineSegment(sketch, "E1608", {"start": v(52.2, 37.8) * mm, "end": v(48.22, 37.8) * mm});
            skLineSegment(sketch, "E1609", {"start": v(48.22, 37.8) * mm, "end": v(52.2, 41.78) * mm});
            skLineSegment(sketch, "E1610", {"start": v(47.2, 36.78) * mm, "end": v(47.2, 32.8) * mm});
            skLineSegment(sketch, "E1611", {"start": v(47.2, 32.8) * mm, "end": v(43.22, 32.8) * mm});
            skLineSegment(sketch, "E1612", {"start": v(43.22, 32.8) * mm, "end": v(47.2, 36.78) * mm});
            skLineSegment(sketch, "E1613", {"start": v(42.2, 31.78) * mm, "end": v(42.2, 27.8) * mm});
            skLineSegment(sketch, "E1614", {"start": v(42.2, 27.8) * mm, "end": v(38.22, 27.8) * mm});
            skLineSegment(sketch, "E1615", {"start": v(38.22, 27.8) * mm, "end": v(42.2, 31.78) * mm});
            skLineSegment(sketch, "E1616", {"start": v(37.2, 23.22) * mm, "end": v(33.22, 27.2) * mm});
            skLineSegment(sketch, "E1617", {"start": v(33.22, 27.2) * mm, "end": v(37.2, 27.2) * mm});
            skLineSegment(sketch, "E1618", {"start": v(37.2, 27.2) * mm, "end": v(37.2, 23.22) * mm});
            skLineSegment(sketch, "E1619", {"start": v(32.2, 23.22) * mm, "end": v(28.22, 27.2) * mm});
            skLineSegment(sketch, "E1620", {"start": v(28.22, 27.2) * mm, "end": v(32.2, 27.2) * mm});
            skLineSegment(sketch, "E1621", {"start": v(32.2, 27.2) * mm, "end": v(32.2, 23.22) * mm});
            skLineSegment(sketch, "E1622", {"start": v(27.8, 38.22) * mm, "end": v(27.8, 42.2) * mm});
            skLineSegment(sketch, "E1623", {"start": v(27.8, 42.2) * mm, "end": v(31.78, 42.2) * mm});
            skLineSegment(sketch, "E1624", {"start": v(31.78, 42.2) * mm, "end": v(27.8, 38.22) * mm});
            skLineSegment(sketch, "E1625", {"start": v(32.8, 43.22) * mm, "end": v(32.8, 47.2) * mm});
            skLineSegment(sketch, "E1626", {"start": v(32.8, 47.2) * mm, "end": v(36.78, 47.2) * mm});
            skLineSegment(sketch, "E1627", {"start": v(36.78, 47.2) * mm, "end": v(32.8, 43.22) * mm});
            skLineSegment(sketch, "E1628", {"start": v(37.8, 48.22) * mm, "end": v(37.8, 52.2) * mm});
            skLineSegment(sketch, "E1629", {"start": v(37.8, 52.2) * mm, "end": v(41.78, 52.2) * mm});
            skLineSegment(sketch, "E1630", {"start": v(41.78, 52.2) * mm, "end": v(37.8, 48.22) * mm});
            skLineSegment(sketch, "E1631", {"start": v(42.8, 53.22) * mm, "end": v(42.8, 57.2) * mm});
            skLineSegment(sketch, "E1632", {"start": v(42.8, 57.2) * mm, "end": v(46.78, 57.2) * mm});
            skLineSegment(sketch, "E1633", {"start": v(46.78, 57.2) * mm, "end": v(42.8, 53.22) * mm});
            skLineSegment(sketch, "E1634", {"start": v(47.8, 58.22) * mm, "end": v(47.8, 62.2) * mm});
            skLineSegment(sketch, "E1635", {"start": v(47.8, 62.2) * mm, "end": v(51.78, 62.2) * mm});
            skLineSegment(sketch, "E1636", {"start": v(51.78, 62.2) * mm, "end": v(47.8, 58.22) * mm});
            skLineSegment(sketch, "E1637", {"start": v(52.8, 63.22) * mm, "end": v(52.8, 67.2) * mm});
            skLineSegment(sketch, "E1638", {"start": v(52.8, 67.2) * mm, "end": v(56.78, 67.2) * mm});
            skLineSegment(sketch, "E1639", {"start": v(56.78, 67.2) * mm, "end": v(52.8, 63.22) * mm});
            skLineSegment(sketch, "E1640", {"start": v(57.8, 68.22) * mm, "end": v(57.8, 72.2) * mm});
            skLineSegment(sketch, "E1641", {"start": v(57.8, 72.2) * mm, "end": v(61.78, 72.2) * mm});
            skLineSegment(sketch, "E1642", {"start": v(61.78, 72.2) * mm, "end": v(57.8, 68.22) * mm});
            skLineSegment(sketch, "E1643", {"start": v(62.8, 73.22) * mm, "end": v(62.8, 77.2) * mm});
            skLineSegment(sketch, "E1644", {"start": v(62.8, 77.2) * mm, "end": v(66.78, 77.2) * mm});
            skLineSegment(sketch, "E1645", {"start": v(66.78, 77.2) * mm, "end": v(62.8, 73.22) * mm});
            skLineSegment(sketch, "E1646", {"start": v(67.8, 78.22) * mm, "end": v(67.8, 82.2) * mm});
            skLineSegment(sketch, "E1647", {"start": v(67.8, 82.2) * mm, "end": v(71.78, 82.2) * mm});
            skLineSegment(sketch, "E1648", {"start": v(71.78, 82.2) * mm, "end": v(67.8, 78.22) * mm});
            skLineSegment(sketch, "E1649", {"start": v(72.8, 83.22) * mm, "end": v(72.8, 87.2) * mm});
            skLineSegment(sketch, "E1650", {"start": v(72.8, 87.2) * mm, "end": v(76.78, 87.2) * mm});
            skLineSegment(sketch, "E1651", {"start": v(76.78, 87.2) * mm, "end": v(72.8, 83.22) * mm});
            skLineSegment(sketch, "E1652", {"start": v(67.2, 91.78) * mm, "end": v(67.2, 87.8) * mm});
            skLineSegment(sketch, "E1653", {"start": v(67.2, 87.8) * mm, "end": v(63.22, 87.8) * mm});
            skLineSegment(sketch, "E1654", {"start": v(63.22, 87.8) * mm, "end": v(67.2, 91.78) * mm});
            skLineSegment(sketch, "E1655", {"start": v(57.2, 86.78) * mm, "end": v(57.2, 82.8) * mm});
            skLineSegment(sketch, "E1656", {"start": v(57.2, 82.8) * mm, "end": v(53.22, 82.8) * mm});
            skLineSegment(sketch, "E1657", {"start": v(53.22, 82.8) * mm, "end": v(57.2, 86.78) * mm});
            skLineSegment(sketch, "E1658", {"start": v(52.2, 81.78) * mm, "end": v(52.2, 77.8) * mm});
            skLineSegment(sketch, "E1659", {"start": v(52.2, 77.8) * mm, "end": v(48.22, 77.8) * mm});
            skLineSegment(sketch, "E1660", {"start": v(48.22, 77.8) * mm, "end": v(52.2, 81.78) * mm});
            skLineSegment(sketch, "E1661", {"start": v(47.2, 72.8) * mm, "end": v(43.22, 72.8) * mm});
            skLineSegment(sketch, "E1662", {"start": v(43.22, 72.8) * mm, "end": v(47.2, 76.78) * mm});
            skLineSegment(sketch, "E1663", {"start": v(47.2, 76.78) * mm, "end": v(47.2, 72.8) * mm});
            skLineSegment(sketch, "E1664", {"start": v(42.2, 68.22) * mm, "end": v(38.22, 72.2) * mm});
            skLineSegment(sketch, "E1665", {"start": v(38.22, 72.2) * mm, "end": v(42.2, 72.2) * mm});
            skLineSegment(sketch, "E1666", {"start": v(42.2, 72.2) * mm, "end": v(42.2, 68.22) * mm});
            skLineSegment(sketch, "E1667", {"start": v(37.2, 71.78) * mm, "end": v(37.2, 67.8) * mm});
            skLineSegment(sketch, "E1668", {"start": v(37.2, 67.8) * mm, "end": v(33.22, 67.8) * mm});
            skLineSegment(sketch, "E1669", {"start": v(33.22, 67.8) * mm, "end": v(37.2, 71.78) * mm});
            skLineSegment(sketch, "E1670", {"start": v(32.2, 66.78) * mm, "end": v(32.2, 62.8) * mm});
            skLineSegment(sketch, "E1671", {"start": v(32.2, 62.8) * mm, "end": v(28.22, 62.8) * mm});
            skLineSegment(sketch, "E1672", {"start": v(28.22, 62.8) * mm, "end": v(32.2, 66.78) * mm});
            skLineSegment(sketch, "E1673", {"start": v(27.2, 61.78) * mm, "end": v(27.2, 57.8) * mm});
            skLineSegment(sketch, "E1674", {"start": v(27.2, 57.8) * mm, "end": v(23.22, 57.8) * mm});
            skLineSegment(sketch, "E1675", {"start": v(23.22, 57.8) * mm, "end": v(27.2, 61.78) * mm});
            skLineSegment(sketch, "E1676", {"start": v(22.2, 56.78) * mm, "end": v(22.2, 52.8) * mm});
            skLineSegment(sketch, "E1677", {"start": v(22.2, 52.8) * mm, "end": v(18.22, 52.8) * mm});
            skLineSegment(sketch, "E1678", {"start": v(18.22, 52.8) * mm, "end": v(22.2, 56.78) * mm});
            skLineSegment(sketch, "E1679", {"start": v(17.2, 51.78) * mm, "end": v(17.2, 47.8) * mm});
            skLineSegment(sketch, "E1680", {"start": v(17.2, 47.8) * mm, "end": v(13.22, 47.8) * mm});
            skLineSegment(sketch, "E1681", {"start": v(13.22, 47.8) * mm, "end": v(17.2, 51.78) * mm});
            skLineSegment(sketch, "E1682", {"start": v(12.2, 46.78) * mm, "end": v(12.2, 42.8) * mm});
            skLineSegment(sketch, "E1683", {"start": v(12.2, 42.8) * mm, "end": v(8.22, 42.8) * mm});
            skLineSegment(sketch, "E1684", {"start": v(8.22, 42.8) * mm, "end": v(12.2, 46.78) * mm});
            skLineSegment(sketch, "E1685", {"start": v(7.2, 41.78) * mm, "end": v(7.2, 37.8) * mm});
            skLineSegment(sketch, "E1686", {"start": v(7.2, 37.8) * mm, "end": v(3.22, 37.8) * mm});
            skLineSegment(sketch, "E1687", {"start": v(3.22, 37.8) * mm, "end": v(7.2, 41.78) * mm});
            skLineSegment(sketch, "E1688", {"start": v(-2.8, 23.22) * mm, "end": v(-6.78, 27.2) * mm});
            skLineSegment(sketch, "E1689", {"start": v(-6.78, 27.2) * mm, "end": v(-2.8, 27.2) * mm});
            skLineSegment(sketch, "E1690", {"start": v(-2.8, 27.2) * mm, "end": v(-2.8, 23.22) * mm});
            skLineSegment(sketch, "E1691", {"start": v(-7.8, 22.8) * mm, "end": v(-11.78, 22.8) * mm});
            skLineSegment(sketch, "E1692", {"start": v(-11.78, 22.8) * mm, "end": v(-7.8, 26.78) * mm});
            skLineSegment(sketch, "E1693", {"start": v(-7.8, 26.78) * mm, "end": v(-7.8, 22.8) * mm});
            skLineSegment(sketch, "E1694", {"start": v(-17.8, 18.22) * mm, "end": v(-21.78, 22.2) * mm});
            skLineSegment(sketch, "E1695", {"start": v(-21.78, 22.2) * mm, "end": v(-17.8, 22.2) * mm});
            skLineSegment(sketch, "E1696", {"start": v(-17.8, 22.2) * mm, "end": v(-17.8, 18.22) * mm});
            skLineSegment(sketch, "E1697", {"start": v(-22.8, 18.22) * mm, "end": v(-26.78, 22.2) * mm});
            skLineSegment(sketch, "E1698", {"start": v(-26.78, 22.2) * mm, "end": v(-22.8, 22.2) * mm});
            skLineSegment(sketch, "E1699", {"start": v(-22.8, 22.2) * mm, "end": v(-22.8, 18.22) * mm});
            skLineSegment(sketch, "E1700", {"start": v(-32.8, 18.22) * mm, "end": v(-36.78, 22.2) * mm});
            skLineSegment(sketch, "E1701", {"start": v(-36.78, 22.2) * mm, "end": v(-32.8, 22.2) * mm});
            skLineSegment(sketch, "E1702", {"start": v(-32.8, 22.2) * mm, "end": v(-32.8, 18.22) * mm});
            skLineSegment(sketch, "E1703", {"start": v(-37.8, 21.78) * mm, "end": v(-37.8, 17.8) * mm});
            skLineSegment(sketch, "E1704", {"start": v(-37.8, 17.8) * mm, "end": v(-41.78, 17.8) * mm});
            skLineSegment(sketch, "E1705", {"start": v(-41.78, 17.8) * mm, "end": v(-37.8, 21.78) * mm});
            skLineSegment(sketch, "E1706", {"start": v(-42.8, 16.78) * mm, "end": v(-42.8, 12.8) * mm});
            skLineSegment(sketch, "E1707", {"start": v(-42.8, 12.8) * mm, "end": v(-46.78, 12.8) * mm});
            skLineSegment(sketch, "E1708", {"start": v(-46.78, 12.8) * mm, "end": v(-42.8, 16.78) * mm});
            skLineSegment(sketch, "E1709", {"start": v(-47.8, 11.78) * mm, "end": v(-47.8, 7.8) * mm});
            skLineSegment(sketch, "E1710", {"start": v(-47.8, 7.8) * mm, "end": v(-51.78, 7.8) * mm});
            skLineSegment(sketch, "E1711", {"start": v(-51.78, 7.8) * mm, "end": v(-47.8, 11.78) * mm});
            skLineSegment(sketch, "E1712", {"start": v(-57.8, -2.2) * mm, "end": v(-61.78, -2.2) * mm});
            skLineSegment(sketch, "E1713", {"start": v(-61.78, -2.2) * mm, "end": v(-57.8, 1.78) * mm});
            skLineSegment(sketch, "E1714", {"start": v(-57.8, 1.78) * mm, "end": v(-57.8, -2.2) * mm});
            skLineSegment(sketch, "E1715", {"start": v(-62.8, -3.22) * mm, "end": v(-62.8, -7.2) * mm});
            skLineSegment(sketch, "E1716", {"start": v(-62.8, -7.2) * mm, "end": v(-66.78, -7.2) * mm});
            skLineSegment(sketch, "E1717", {"start": v(-66.78, -7.2) * mm, "end": v(-62.8, -3.22) * mm});
            skLineSegment(sketch, "E1718", {"start": v(-67.8, -12.2) * mm, "end": v(-71.78, -12.2) * mm});
            skLineSegment(sketch, "E1719", {"start": v(-71.78, -12.2) * mm, "end": v(-67.8, -8.22) * mm});
            skLineSegment(sketch, "E1720", {"start": v(-67.8, -8.22) * mm, "end": v(-67.8, -12.2) * mm});
            skLineSegment(sketch, "E1721", {"start": v(-72.8, -13.22) * mm, "end": v(-72.8, -17.2) * mm});
            skLineSegment(sketch, "E1722", {"start": v(-72.8, -17.2) * mm, "end": v(-76.78, -17.2) * mm});
            skLineSegment(sketch, "E1723", {"start": v(-76.78, -17.2) * mm, "end": v(-72.8, -13.22) * mm});
            skLineSegment(sketch, "E1724", {"start": v(-77.8, -22.2) * mm, "end": v(-81.78, -22.2) * mm});
            skLineSegment(sketch, "E1725", {"start": v(-81.78, -22.2) * mm, "end": v(-77.8, -18.22) * mm});
            skLineSegment(sketch, "E1726", {"start": v(-77.8, -18.22) * mm, "end": v(-77.8, -22.2) * mm});
            skLineSegment(sketch, "E1727", {"start": v(-82.8, -23.22) * mm, "end": v(-82.8, -27.2) * mm});
            skLineSegment(sketch, "E1728", {"start": v(-82.8, -27.2) * mm, "end": v(-86.78, -27.2) * mm});
            skLineSegment(sketch, "E1729", {"start": v(-86.78, -27.2) * mm, "end": v(-82.8, -23.22) * mm});
            skLineSegment(sketch, "E1730", {"start": v(-87.8, -32.2) * mm, "end": v(-91.78, -32.2) * mm});
            skLineSegment(sketch, "E1731", {"start": v(-91.78, -32.2) * mm, "end": v(-87.8, -28.22) * mm});
            skLineSegment(sketch, "E1732", {"start": v(-87.8, -28.22) * mm, "end": v(-87.8, -32.2) * mm});
            skLineSegment(sketch, "E1733", {"start": v(-92.2, -38.22) * mm, "end": v(-88.22, -42.2) * mm});
            skLineSegment(sketch, "E1734", {"start": v(-88.22, -42.2) * mm, "end": v(-92.2, -42.2) * mm});
            skLineSegment(sketch, "E1735", {"start": v(-92.2, -42.2) * mm, "end": v(-92.2, -38.22) * mm});
            skLineSegment(sketch, "E1736", {"start": v(-87.2, -38.22) * mm, "end": v(-83.22, -42.2) * mm});
            skLineSegment(sketch, "E1737", {"start": v(-83.22, -42.2) * mm, "end": v(-87.2, -42.2) * mm});
            skLineSegment(sketch, "E1738", {"start": v(-87.2, -42.2) * mm, "end": v(-87.2, -38.22) * mm});
            skLineSegment(sketch, "E1739", {"start": v(-82.2, -38.22) * mm, "end": v(-78.22, -42.2) * mm});
            skLineSegment(sketch, "E1740", {"start": v(-78.22, -42.2) * mm, "end": v(-82.2, -42.2) * mm});
            skLineSegment(sketch, "E1741", {"start": v(-82.2, -42.2) * mm, "end": v(-82.2, -38.22) * mm});
            skLineSegment(sketch, "E1742", {"start": v(-77.2, -37.8) * mm, "end": v(-73.22, -37.8) * mm});
            skLineSegment(sketch, "E1743", {"start": v(-73.22, -37.8) * mm, "end": v(-77.2, -41.78) * mm});
            skLineSegment(sketch, "E1744", {"start": v(-77.2, -41.78) * mm, "end": v(-77.2, -37.8) * mm});
            skLineSegment(sketch, "E1745", {"start": v(-72.2, -32.8) * mm, "end": v(-68.22, -32.8) * mm});
            skLineSegment(sketch, "E1746", {"start": v(-68.22, -32.8) * mm, "end": v(-72.2, -36.78) * mm});
            skLineSegment(sketch, "E1747", {"start": v(-72.2, -36.78) * mm, "end": v(-72.2, -32.8) * mm});
            skLineSegment(sketch, "E1748", {"start": v(-67.2, -27.8) * mm, "end": v(-63.22, -27.8) * mm});
            skLineSegment(sketch, "E1749", {"start": v(-63.22, -27.8) * mm, "end": v(-67.2, -31.78) * mm});
            skLineSegment(sketch, "E1750", {"start": v(-67.2, -31.78) * mm, "end": v(-67.2, -27.8) * mm});
            skLineSegment(sketch, "E1751", {"start": v(-62.2, -22.8) * mm, "end": v(-58.22, -22.8) * mm});
            skLineSegment(sketch, "E1752", {"start": v(-58.22, -22.8) * mm, "end": v(-62.2, -26.78) * mm});
            skLineSegment(sketch, "E1753", {"start": v(-62.2, -26.78) * mm, "end": v(-62.2, -22.8) * mm});
            skLineSegment(sketch, "E1754", {"start": v(-57.2, -21.78) * mm, "end": v(-57.2, -17.8) * mm});
            skLineSegment(sketch, "E1755", {"start": v(-57.2, -17.8) * mm, "end": v(-53.22, -17.8) * mm});
            skLineSegment(sketch, "E1756", {"start": v(-53.22, -17.8) * mm, "end": v(-57.2, -21.78) * mm});
            skLineSegment(sketch, "E1757", {"start": v(-52.2, -16.78) * mm, "end": v(-52.2, -12.8) * mm});
            skLineSegment(sketch, "E1758", {"start": v(-52.2, -12.8) * mm, "end": v(-48.22, -12.8) * mm});
            skLineSegment(sketch, "E1759", {"start": v(-48.22, -12.8) * mm, "end": v(-52.2, -16.78) * mm});
            skLineSegment(sketch, "E1760", {"start": v(-47.2, -7.8) * mm, "end": v(-43.22, -7.8) * mm});
            skLineSegment(sketch, "E1761", {"start": v(-43.22, -7.8) * mm, "end": v(-47.2, -11.78) * mm});
            skLineSegment(sketch, "E1762", {"start": v(-47.2, -11.78) * mm, "end": v(-47.2, -7.8) * mm});
            skLineSegment(sketch, "E1763", {"start": v(-42.2, -2.8) * mm, "end": v(-38.22, -2.8) * mm});
            skLineSegment(sketch, "E1764", {"start": v(-38.22, -2.8) * mm, "end": v(-42.2, -6.78) * mm});
            skLineSegment(sketch, "E1765", {"start": v(-42.2, -6.78) * mm, "end": v(-42.2, -2.8) * mm});
            skLineSegment(sketch, "E1766", {"start": v(-37.2, -1.78) * mm, "end": v(-37.2, 2.2) * mm});
            skLineSegment(sketch, "E1767", {"start": v(-37.2, 2.2) * mm, "end": v(-33.22, 2.2) * mm});
            skLineSegment(sketch, "E1768", {"start": v(-33.22, 2.2) * mm, "end": v(-37.2, -1.78) * mm});
            skLineSegment(sketch, "E1769", {"start": v(-32.2, 6.78) * mm, "end": v(-28.22, 2.8) * mm});
            skLineSegment(sketch, "E1770", {"start": v(-28.22, 2.8) * mm, "end": v(-32.2, 2.8) * mm});
            skLineSegment(sketch, "E1771", {"start": v(-32.2, 2.8) * mm, "end": v(-32.2, 6.78) * mm});
            skLineSegment(sketch, "E1772", {"start": v(-17.2, 6.78) * mm, "end": v(-13.22, 2.8) * mm});
            skLineSegment(sketch, "E1773", {"start": v(-13.22, 2.8) * mm, "end": v(-17.2, 2.8) * mm});
            skLineSegment(sketch, "E1774", {"start": v(-17.2, 2.8) * mm, "end": v(-17.2, 6.78) * mm});
            skLineSegment(sketch, "E1775", {"start": v(-2.2, 6.78) * mm, "end": v(1.78, 2.8) * mm});
            skLineSegment(sketch, "E1776", {"start": v(1.78, 2.8) * mm, "end": v(-2.2, 2.8) * mm});
            skLineSegment(sketch, "E1777", {"start": v(-2.2, 2.8) * mm, "end": v(-2.2, 6.78) * mm});
            skLineSegment(sketch, "E1778", {"start": v(2.2, -33.22) * mm, "end": v(2.2, -37.2) * mm});
            skLineSegment(sketch, "E1779", {"start": v(2.2, -37.2) * mm, "end": v(-1.78, -37.2) * mm});
            skLineSegment(sketch, "E1780", {"start": v(-1.78, -37.2) * mm, "end": v(2.2, -33.22) * mm});
            skLineSegment(sketch, "E1781", {"start": v(-2.8, -38.22) * mm, "end": v(-2.8, -42.2) * mm});
            skLineSegment(sketch, "E1782", {"start": v(-2.8, -42.2) * mm, "end": v(-6.78, -42.2) * mm});
            skLineSegment(sketch, "E1783", {"start": v(-6.78, -42.2) * mm, "end": v(-2.8, -38.22) * mm});
            skLineSegment(sketch, "E1784", {"start": v(-7.8, -43.22) * mm, "end": v(-7.8, -47.2) * mm});
            skLineSegment(sketch, "E1785", {"start": v(-7.8, -47.2) * mm, "end": v(-11.78, -47.2) * mm});
            skLineSegment(sketch, "E1786", {"start": v(-11.78, -47.2) * mm, "end": v(-7.8, -43.22) * mm});
            skLineSegment(sketch, "E1787", {"start": v(-17.8, -53.22) * mm, "end": v(-17.8, -57.2) * mm});
            skLineSegment(sketch, "E1788", {"start": v(-17.8, -57.2) * mm, "end": v(-21.78, -57.2) * mm});
            skLineSegment(sketch, "E1789", {"start": v(-21.78, -57.2) * mm, "end": v(-17.8, -53.22) * mm});
            skLineSegment(sketch, "E1790", {"start": v(-22.8, -58.22) * mm, "end": v(-22.8, -62.2) * mm});
            skLineSegment(sketch, "E1791", {"start": v(-22.8, -62.2) * mm, "end": v(-26.78, -62.2) * mm});
            skLineSegment(sketch, "E1792", {"start": v(-26.78, -62.2) * mm, "end": v(-22.8, -58.22) * mm});
            skLineSegment(sketch, "E1793", {"start": v(-27.8, -63.22) * mm, "end": v(-27.8, -67.2) * mm});
            skLineSegment(sketch, "E1794", {"start": v(-27.8, -67.2) * mm, "end": v(-31.78, -67.2) * mm});
            skLineSegment(sketch, "E1795", {"start": v(-31.78, -67.2) * mm, "end": v(-27.8, -63.22) * mm});
            skLineSegment(sketch, "E1796", {"start": v(-37.8, -73.22) * mm, "end": v(-37.8, -77.2) * mm});
            skLineSegment(sketch, "E1797", {"start": v(-37.8, -77.2) * mm, "end": v(-41.78, -77.2) * mm});
            skLineSegment(sketch, "E1798", {"start": v(-41.78, -77.2) * mm, "end": v(-37.8, -73.22) * mm});
            skLineSegment(sketch, "E1799", {"start": v(-42.2, -88.22) * mm, "end": v(-38.22, -92.2) * mm});
            skLineSegment(sketch, "E1800", {"start": v(-38.22, -92.2) * mm, "end": v(-42.2, -92.2) * mm});
            skLineSegment(sketch, "E1801", {"start": v(-42.2, -92.2) * mm, "end": v(-42.2, -88.22) * mm});
            skLineSegment(sketch, "E1802", {"start": v(-37.2, -88.22) * mm, "end": v(-33.22, -92.2) * mm});
            skLineSegment(sketch, "E1803", {"start": v(-33.22, -92.2) * mm, "end": v(-37.2, -92.2) * mm});
            skLineSegment(sketch, "E1804", {"start": v(-37.2, -92.2) * mm, "end": v(-37.2, -88.22) * mm});
            skLineSegment(sketch, "E1805", {"start": v(-32.2, -91.78) * mm, "end": v(-32.2, -87.8) * mm});
            skLineSegment(sketch, "E1806", {"start": v(-32.2, -87.8) * mm, "end": v(-28.22, -87.8) * mm});
            skLineSegment(sketch, "E1807", {"start": v(-28.22, -87.8) * mm, "end": v(-32.2, -91.78) * mm});
            skLineSegment(sketch, "E1808", {"start": v(-27.2, -86.78) * mm, "end": v(-27.2, -82.8) * mm});
            skLineSegment(sketch, "E1809", {"start": v(-27.2, -82.8) * mm, "end": v(-23.22, -82.8) * mm});
            skLineSegment(sketch, "E1810", {"start": v(-23.22, -82.8) * mm, "end": v(-27.2, -86.78) * mm});
            skLineSegment(sketch, "E1811", {"start": v(-22.2, -81.78) * mm, "end": v(-22.2, -77.8) * mm});
            skLineSegment(sketch, "E1812", {"start": v(-22.2, -77.8) * mm, "end": v(-18.22, -77.8) * mm});
            skLineSegment(sketch, "E1813", {"start": v(-18.22, -77.8) * mm, "end": v(-22.2, -81.78) * mm});
            skLineSegment(sketch, "E1814", {"start": v(-17.2, -76.78) * mm, "end": v(-17.2, -72.8) * mm});
            skLineSegment(sketch, "E1815", {"start": v(-17.2, -72.8) * mm, "end": v(-13.22, -72.8) * mm});
            skLineSegment(sketch, "E1816", {"start": v(-13.22, -72.8) * mm, "end": v(-17.2, -76.78) * mm});
            skLineSegment(sketch, "E1817", {"start": v(-12.2, -71.78) * mm, "end": v(-12.2, -67.8) * mm});
            skLineSegment(sketch, "E1818", {"start": v(-12.2, -67.8) * mm, "end": v(-8.22, -67.8) * mm});
            skLineSegment(sketch, "E1819", {"start": v(-8.22, -67.8) * mm, "end": v(-12.2, -71.78) * mm});
            skLineSegment(sketch, "E1820", {"start": v(-7.2, -66.78) * mm, "end": v(-7.2, -62.8) * mm});
            skLineSegment(sketch, "E1821", {"start": v(-7.2, -62.8) * mm, "end": v(-3.22, -62.8) * mm});
            skLineSegment(sketch, "E1822", {"start": v(-3.22, -62.8) * mm, "end": v(-7.2, -66.78) * mm});
            skLineSegment(sketch, "E1823", {"start": v(-2.2, -61.78) * mm, "end": v(-2.2, -57.8) * mm});
            skLineSegment(sketch, "E1824", {"start": v(-2.2, -57.8) * mm, "end": v(1.78, -57.8) * mm});
            skLineSegment(sketch, "E1825", {"start": v(1.78, -57.8) * mm, "end": v(-2.2, -61.78) * mm});
            skLineSegment(sketch, "E1826", {"start": v(7.8, -51.78) * mm, "end": v(7.8, -47.8) * mm});
            skLineSegment(sketch, "E1827", {"start": v(7.8, -47.8) * mm, "end": v(11.78, -47.8) * mm});
            skLineSegment(sketch, "E1828", {"start": v(11.78, -47.8) * mm, "end": v(7.8, -51.78) * mm});
            skLineSegment(sketch, "E1829", {"start": v(12.8, -46.78) * mm, "end": v(12.8, -42.8) * mm});
            skLineSegment(sketch, "E1830", {"start": v(12.8, -42.8) * mm, "end": v(16.78, -42.8) * mm});
            skLineSegment(sketch, "E1831", {"start": v(16.78, -42.8) * mm, "end": v(12.8, -46.78) * mm});
            skLineSegment(sketch, "E1832", {"start": v(17.8, -41.78) * mm, "end": v(17.8, -37.8) * mm});
            skLineSegment(sketch, "E1833", {"start": v(17.8, -37.8) * mm, "end": v(21.78, -37.8) * mm});
            skLineSegment(sketch, "E1834", {"start": v(21.78, -37.8) * mm, "end": v(17.8, -41.78) * mm});
            skLineSegment(sketch, "E1835", {"start": v(22.8, -11.78) * mm, "end": v(22.8, -7.8) * mm});
            skLineSegment(sketch, "E1836", {"start": v(22.8, -7.8) * mm, "end": v(26.78, -7.8) * mm});
            skLineSegment(sketch, "E1837", {"start": v(26.78, -7.8) * mm, "end": v(22.8, -11.78) * mm});
            skLineSegment(sketch, "E1838", {"start": v(37.8, 3.22) * mm, "end": v(37.8, 7.2) * mm});
            skLineSegment(sketch, "E1839", {"start": v(37.8, 7.2) * mm, "end": v(41.78, 7.2) * mm});
            skLineSegment(sketch, "E1840", {"start": v(41.78, 7.2) * mm, "end": v(37.8, 3.22) * mm});
            skLineSegment(sketch, "E1841", {"start": v(42.8, 8.22) * mm, "end": v(42.8, 12.2) * mm});
            skLineSegment(sketch, "E1842", {"start": v(42.8, 12.2) * mm, "end": v(46.78, 12.2) * mm});
            skLineSegment(sketch, "E1843", {"start": v(46.78, 12.2) * mm, "end": v(42.8, 8.22) * mm});
            skLineSegment(sketch, "E1844", {"start": v(47.8, 13.22) * mm, "end": v(47.8, 17.2) * mm});
            skLineSegment(sketch, "E1845", {"start": v(47.8, 17.2) * mm, "end": v(51.78, 17.2) * mm});
            skLineSegment(sketch, "E1846", {"start": v(51.78, 17.2) * mm, "end": v(47.8, 13.22) * mm});
            skLineSegment(sketch, "E1847", {"start": v(52.8, 22.2) * mm, "end": v(56.78, 22.2) * mm});
            skLineSegment(sketch, "E1848", {"start": v(56.78, 22.2) * mm, "end": v(52.8, 18.22) * mm});
            skLineSegment(sketch, "E1849", {"start": v(52.8, 18.22) * mm, "end": v(52.8, 22.2) * mm});
            skLineSegment(sketch, "E1850", {"start": v(57.8, 23.22) * mm, "end": v(57.8, 27.2) * mm});
            skLineSegment(sketch, "E1851", {"start": v(57.8, 27.2) * mm, "end": v(61.78, 27.2) * mm});
            skLineSegment(sketch, "E1852", {"start": v(61.78, 27.2) * mm, "end": v(57.8, 23.22) * mm});
            skLineSegment(sketch, "E1853", {"start": v(62.8, 32.2) * mm, "end": v(66.78, 32.2) * mm});
            skLineSegment(sketch, "E1854", {"start": v(66.78, 32.2) * mm, "end": v(62.8, 28.22) * mm});
            skLineSegment(sketch, "E1855", {"start": v(62.8, 28.22) * mm, "end": v(62.8, 32.2) * mm});
            skLineSegment(sketch, "E1856", {"start": v(67.8, 33.22) * mm, "end": v(67.8, 37.2) * mm});
            skLineSegment(sketch, "E1857", {"start": v(67.8, 37.2) * mm, "end": v(71.78, 37.2) * mm});
            skLineSegment(sketch, "E1858", {"start": v(71.78, 37.2) * mm, "end": v(67.8, 33.22) * mm});
            skLineSegment(sketch, "E1859", {"start": v(72.8, 43.22) * mm, "end": v(72.8, 47.2) * mm});
            skLineSegment(sketch, "E1860", {"start": v(72.8, 47.2) * mm, "end": v(76.78, 47.2) * mm});
            skLineSegment(sketch, "E1861", {"start": v(76.78, 47.2) * mm, "end": v(72.8, 43.22) * mm});
            skLineSegment(sketch, "E1862", {"start": v(77.8, 48.22) * mm, "end": v(77.8, 52.2) * mm});
            skLineSegment(sketch, "E1863", {"start": v(77.8, 52.2) * mm, "end": v(81.78, 52.2) * mm});
            skLineSegment(sketch, "E1864", {"start": v(81.78, 52.2) * mm, "end": v(77.8, 48.22) * mm});
            skLineSegment(sketch, "E1865", {"start": v(82.8, 57.2) * mm, "end": v(86.78, 57.2) * mm});
            skLineSegment(sketch, "E1866", {"start": v(86.78, 57.2) * mm, "end": v(82.8, 53.22) * mm});
            skLineSegment(sketch, "E1867", {"start": v(82.8, 53.22) * mm, "end": v(82.8, 57.2) * mm});
            skLineSegment(sketch, "E1868", {"start": v(87.8, 67.2) * mm, "end": v(91.78, 67.2) * mm});
            skLineSegment(sketch, "E1869", {"start": v(91.78, 67.2) * mm, "end": v(87.8, 63.22) * mm});
            skLineSegment(sketch, "E1870", {"start": v(87.8, 63.22) * mm, "end": v(87.8, 67.2) * mm});
            skLineSegment(sketch, "E1871", {"start": v(-42.5, -92.5) * mm, "end": v(-32.5, -92.5) * mm});
            skLineSegment(sketch, "E1872", {"start": v(-32.5, -92.5) * mm, "end": v(22.5, -37.5) * mm});
            skLineSegment(sketch, "E1873", {"start": v(22.5, -37.5) * mm, "end": v(22.5, -12.5) * mm});
            skLineSegment(sketch, "E1874", {"start": v(22.5, -12.5) * mm, "end": v(27.5, -7.5) * mm});
            skLineSegment(sketch, "E1875", {"start": v(27.5, -7.5) * mm, "end": v(27.5, 2.5) * mm});
            skLineSegment(sketch, "E1876", {"start": v(27.5, 2.5) * mm, "end": v(37.5, 2.5) * mm});
            skLineSegment(sketch, "E1877", {"start": v(37.5, 2.5) * mm, "end": v(72.5, 37.5) * mm});
            skLineSegment(sketch, "E1878", {"start": v(72.5, 37.5) * mm, "end": v(72.5, 42.5) * mm});
            skLineSegment(sketch, "E1879", {"start": v(72.5, 42.5) * mm, "end": v(87.5, 57.5) * mm});
            skLineSegment(sketch, "E1880", {"start": v(87.5, 57.5) * mm, "end": v(87.5, 62.5) * mm});
            skLineSegment(sketch, "E1881", {"start": v(87.5, 62.5) * mm, "end": v(92.5, 67.5) * mm});
            skLineSegment(sketch, "E1882", {"start": v(92.5, 67.5) * mm, "end": v(92.5, 77.5) * mm});
            skLineSegment(sketch, "E1883", {"start": v(92.5, 77.5) * mm, "end": v(87.5, 77.5) * mm});
            skLineSegment(sketch, "E1884", {"start": v(87.5, 77.5) * mm, "end": v(37.5, 27.5) * mm});
            skLineSegment(sketch, "E1885", {"start": v(37.5, 27.5) * mm, "end": v(27.5, 27.5) * mm});
            skLineSegment(sketch, "E1886", {"start": v(27.5, 27.5) * mm, "end": v(27.5, 37.5) * mm});
            skLineSegment(sketch, "E1887", {"start": v(27.5, 37.5) * mm, "end": v(77.5, 87.5) * mm});
            skLineSegment(sketch, "E1888", {"start": v(77.5, 87.5) * mm, "end": v(77.5, 92.5) * mm});
            skLineSegment(sketch, "E1889", {"start": v(77.5, 92.5) * mm, "end": v(67.5, 92.5) * mm});
            skLineSegment(sketch, "E1890", {"start": v(67.5, 92.5) * mm, "end": v(62.5, 87.5) * mm});
            skLineSegment(sketch, "E1891", {"start": v(62.5, 87.5) * mm, "end": v(57.5, 87.5) * mm});
            skLineSegment(sketch, "E1892", {"start": v(57.5, 87.5) * mm, "end": v(42.5, 72.5) * mm});
            skLineSegment(sketch, "E1893", {"start": v(42.5, 72.5) * mm, "end": v(37.5, 72.5) * mm});
            skLineSegment(sketch, "E1894", {"start": v(37.5, 72.5) * mm, "end": v(2.5, 37.5) * mm});
            skLineSegment(sketch, "E1895", {"start": v(2.5, 37.5) * mm, "end": v(2.5, 27.5) * mm});
            skLineSegment(sketch, "E1896", {"start": v(2.5, 27.5) * mm, "end": v(-7.5, 27.5) * mm});
            skLineSegment(sketch, "E1897", {"start": v(-7.5, 27.5) * mm, "end": v(-12.5, 22.5) * mm});
            skLineSegment(sketch, "E1898", {"start": v(-12.5, 22.5) * mm, "end": v(-37.5, 22.5) * mm});
            skLineSegment(sketch, "E1899", {"start": v(-37.5, 22.5) * mm, "end": v(-92.5, -32.5) * mm});
            skLineSegment(sketch, "E1900", {"start": v(-92.5, -32.5) * mm, "end": v(-92.5, -42.5) * mm});
            skLineSegment(sketch, "E1901", {"start": v(-92.5, -42.5) * mm, "end": v(-77.5, -42.5) * mm});
            skLineSegment(sketch, "E1902", {"start": v(-77.5, -42.5) * mm, "end": v(-32.5, 2.5) * mm});
            skLineSegment(sketch, "E1903", {"start": v(-32.5, 2.5) * mm, "end": v(2.5, 2.5) * mm});
            skLineSegment(sketch, "E1904", {"start": v(2.5, 2.5) * mm, "end": v(2.5, -32.5) * mm});
            skLineSegment(sketch, "E1905", {"start": v(2.5, -32.5) * mm, "end": v(-42.5, -77.5) * mm});
            skLineSegment(sketch, "E1906", {"start": v(-42.5, -77.5) * mm, "end": v(-42.5, -92.5) * mm});
            skSolve(sketch);
        }
        {
            var Q0;
            Q0=makeQuery(id+"F0.imprint","IMPRINT",FACE,{"disambiguationData":[TD([[makeQuery(id+"F0.imprint","IMPRINT",EDGE,{"derivedFrom":sQuery(id+"F0.wireOp",EDGE,"E0")}),1.0]])]});
            extrude(context, id + "F1", {"entities" : qUnion([Q0]), "endBound" : BoundingType.SYMMETRIC, "depth" : 10 * mm});
        }
    });
